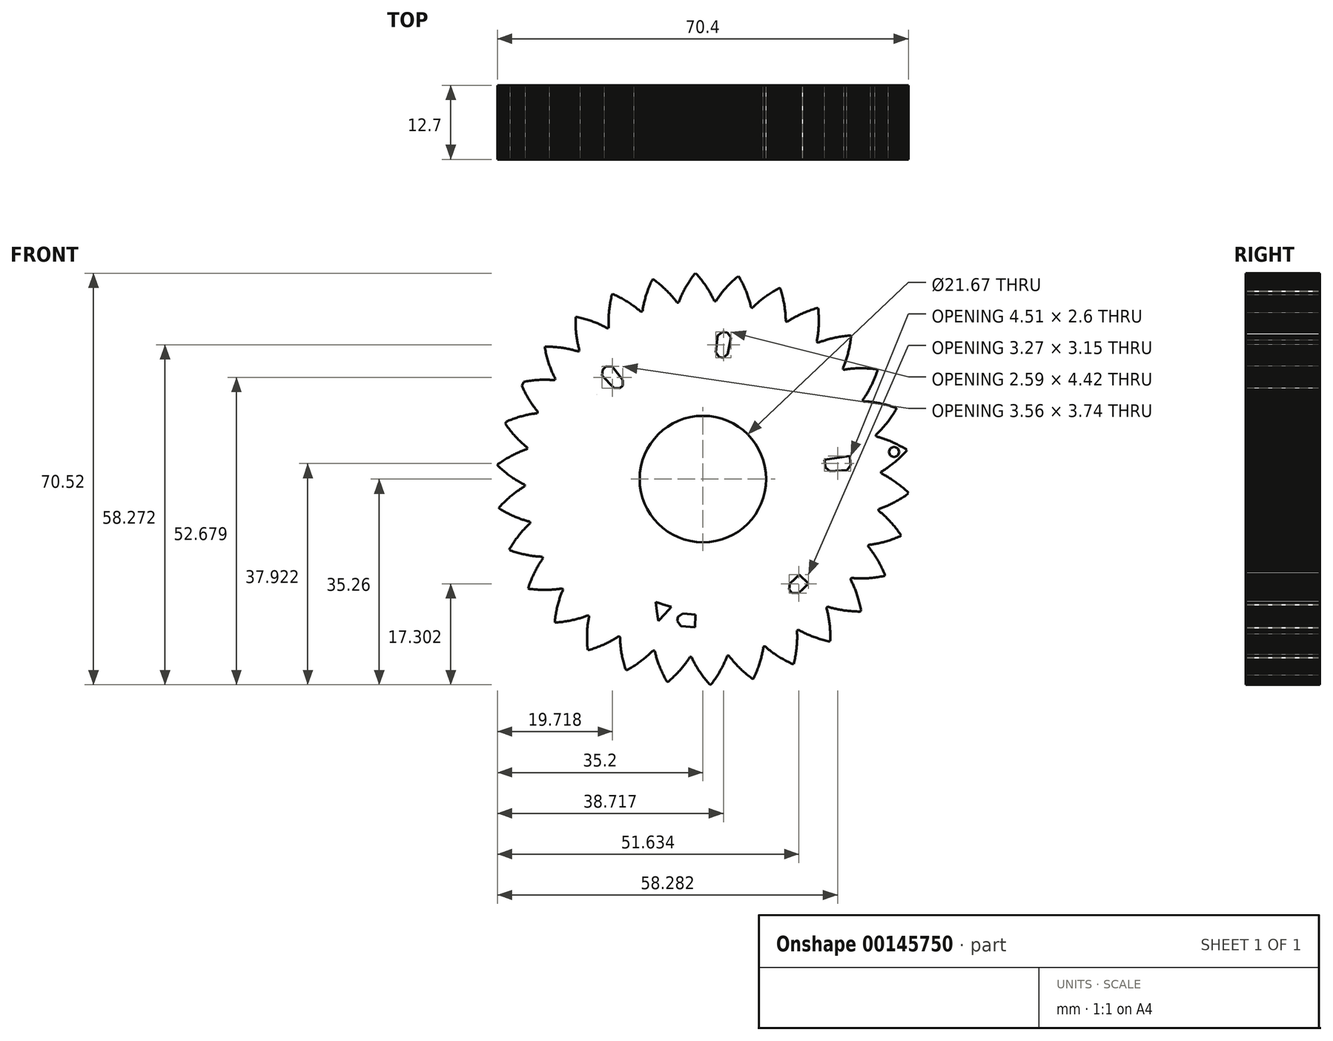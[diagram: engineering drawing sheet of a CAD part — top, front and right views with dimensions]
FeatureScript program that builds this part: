
annotation { "Feature Type Name" : "Feature", "Feature Type Description" : "" }
export const myFeature = defineFeature(function(context is Context, id is Id, definition is map)
    precondition{}
    {
        {
            var Q0;
            Q0=qCreatedBy(makeId("Front.planeOp"),FACE);
            var sketch = newSketch(context, id + "F0", { "sketchPlane" : qUnion([Q0])});
            skLineSegment(sketch, "E0", {"start": v(30.52, 1.1) * mm, "end": v(30.55, 1.26) * mm});
            skLineSegment(sketch, "E1", {"start": v(30.55, 1.26) * mm, "end": v(30.7, 1.34) * mm});
            skLineSegment(sketch, "E2", {"start": v(30.7, 1.34) * mm, "end": v(30.84, 1.43) * mm});
            skLineSegment(sketch, "E3", {"start": v(30.84, 1.43) * mm, "end": v(31, 1.52) * mm});
            skLineSegment(sketch, "E4", {"start": v(31, 1.52) * mm, "end": v(31.14, 1.62) * mm});
            skLineSegment(sketch, "E5", {"start": v(31.14, 1.62) * mm, "end": v(31.3, 1.72) * mm});
            skLineSegment(sketch, "E6", {"start": v(31.3, 1.72) * mm, "end": v(31.45, 1.82) * mm});
            skLineSegment(sketch, "E7", {"start": v(31.45, 1.82) * mm, "end": v(31.6, 1.93) * mm});
            skLineSegment(sketch, "E8", {"start": v(31.6, 1.93) * mm, "end": v(31.76, 2.04) * mm});
            skLineSegment(sketch, "E9", {"start": v(31.76, 2.04) * mm, "end": v(31.92, 2.15) * mm});
            skLineSegment(sketch, "E10", {"start": v(31.92, 2.15) * mm, "end": v(32.08, 2.27) * mm});
            skLineSegment(sketch, "E11", {"start": v(32.08, 2.27) * mm, "end": v(32.25, 2.4) * mm});
            skLineSegment(sketch, "E12", {"start": v(32.25, 2.4) * mm, "end": v(32.4, 2.52) * mm});
            skLineSegment(sketch, "E13", {"start": v(32.4, 2.52) * mm, "end": v(32.58, 2.65) * mm});
            skLineSegment(sketch, "E14", {"start": v(32.58, 2.65) * mm, "end": v(32.74, 2.79) * mm});
            skLineSegment(sketch, "E15", {"start": v(32.74, 2.79) * mm, "end": v(32.91, 2.93) * mm});
            skLineSegment(sketch, "E16", {"start": v(32.91, 2.93) * mm, "end": v(33.08, 3.07) * mm});
            skLineSegment(sketch, "E17", {"start": v(33.08, 3.07) * mm, "end": v(33.25, 3.22) * mm});
            skLineSegment(sketch, "E18", {"start": v(33.25, 3.22) * mm, "end": v(33.42, 3.37) * mm});
            skLineSegment(sketch, "E19", {"start": v(33.42, 3.37) * mm, "end": v(33.6, 3.53) * mm});
            skLineSegment(sketch, "E20", {"start": v(33.6, 3.53) * mm, "end": v(33.77, 3.69) * mm});
            skLineSegment(sketch, "E21", {"start": v(33.77, 3.69) * mm, "end": v(33.94, 3.85) * mm});
            skLineSegment(sketch, "E22", {"start": v(33.94, 3.85) * mm, "end": v(34.11, 4.02) * mm});
            skLineSegment(sketch, "E23", {"start": v(34.11, 4.02) * mm, "end": v(34.29, 4.2) * mm});
            skLineSegment(sketch, "E24", {"start": v(34.29, 4.2) * mm, "end": v(34.47, 4.38) * mm});
            skLineSegment(sketch, "E25", {"start": v(34.47, 4.38) * mm, "end": v(34.64, 4.56) * mm});
            skLineSegment(sketch, "E26", {"start": v(34.64, 4.56) * mm, "end": v(34.82, 4.75) * mm});
            skLineSegment(sketch, "E27", {"start": v(34.82, 4.75) * mm, "end": v(34.93, 4.94) * mm});
            skLineSegment(sketch, "E28", {"start": v(34.93, 4.94) * mm, "end": v(34.92, 4.98) * mm});
            skLineSegment(sketch, "E29", {"start": v(34.92, 4.98) * mm, "end": v(34.77, 5.13) * mm});
            skLineSegment(sketch, "E30", {"start": v(34.77, 5.13) * mm, "end": v(34.54, 5.26) * mm});
            skLineSegment(sketch, "E31", {"start": v(34.54, 5.26) * mm, "end": v(34.32, 5.39) * mm});
            skLineSegment(sketch, "E32", {"start": v(34.32, 5.39) * mm, "end": v(34.1, 5.51) * mm});
            skLineSegment(sketch, "E33", {"start": v(34.1, 5.51) * mm, "end": v(33.89, 5.63) * mm});
            skLineSegment(sketch, "E34", {"start": v(33.89, 5.63) * mm, "end": v(33.67, 5.74) * mm});
            skLineSegment(sketch, "E35", {"start": v(33.67, 5.74) * mm, "end": v(33.46, 5.86) * mm});
            skLineSegment(sketch, "E36", {"start": v(33.46, 5.86) * mm, "end": v(33.25, 5.96) * mm});
            skLineSegment(sketch, "E37", {"start": v(33.25, 5.96) * mm, "end": v(33.04, 6.06) * mm});
            skLineSegment(sketch, "E38", {"start": v(33.04, 6.06) * mm, "end": v(32.83, 6.16) * mm});
            skLineSegment(sketch, "E39", {"start": v(32.83, 6.16) * mm, "end": v(32.63, 6.26) * mm});
            skLineSegment(sketch, "E40", {"start": v(32.63, 6.26) * mm, "end": v(32.43, 6.35) * mm});
            skLineSegment(sketch, "E41", {"start": v(32.43, 6.35) * mm, "end": v(32.22, 6.44) * mm});
            skLineSegment(sketch, "E42", {"start": v(32.22, 6.44) * mm, "end": v(32.03, 6.52) * mm});
            skLineSegment(sketch, "E43", {"start": v(32.03, 6.52) * mm, "end": v(31.83, 6.6) * mm});
            skLineSegment(sketch, "E44", {"start": v(31.83, 6.6) * mm, "end": v(31.64, 6.68) * mm});
            skLineSegment(sketch, "E45", {"start": v(31.64, 6.68) * mm, "end": v(31.45, 6.75) * mm});
            skLineSegment(sketch, "E46", {"start": v(31.45, 6.75) * mm, "end": v(31.26, 6.82) * mm});
            skLineSegment(sketch, "E47", {"start": v(31.26, 6.82) * mm, "end": v(31.08, 6.88) * mm});
            skLineSegment(sketch, "E48", {"start": v(31.08, 6.88) * mm, "end": v(30.9, 6.95) * mm});
            skLineSegment(sketch, "E49", {"start": v(30.9, 6.95) * mm, "end": v(30.71, 7) * mm});
            skLineSegment(sketch, "E50", {"start": v(30.71, 7) * mm, "end": v(30.54, 7.06) * mm});
            skLineSegment(sketch, "E51", {"start": v(30.54, 7.06) * mm, "end": v(30.36, 7.11) * mm});
            skLineSegment(sketch, "E52", {"start": v(30.36, 7.11) * mm, "end": v(30.2, 7.16) * mm});
            skLineSegment(sketch, "E53", {"start": v(30.2, 7.16) * mm, "end": v(30.02, 7.2) * mm});
            skLineSegment(sketch, "E54", {"start": v(30.02, 7.2) * mm, "end": v(29.86, 7.25) * mm});
            skLineSegment(sketch, "E55", {"start": v(29.86, 7.25) * mm, "end": v(29.7, 7.3) * mm});
            skLineSegment(sketch, "E56", {"start": v(29.7, 7.3) * mm, "end": v(29.62, 7.43) * mm});
            skLineSegment(sketch, "E57", {"start": v(29.62, 7.43) * mm, "end": v(29.63, 7.59) * mm});
            skLineSegment(sketch, "E58", {"start": v(29.63, 7.59) * mm, "end": v(29.75, 7.7) * mm});
            skLineSegment(sketch, "E59", {"start": v(29.75, 7.7) * mm, "end": v(29.87, 7.81) * mm});
            skLineSegment(sketch, "E60", {"start": v(29.87, 7.81) * mm, "end": v(30, 7.93) * mm});
            skLineSegment(sketch, "E61", {"start": v(30, 7.93) * mm, "end": v(30.13, 8.06) * mm});
            skLineSegment(sketch, "E62", {"start": v(30.13, 8.06) * mm, "end": v(30.25, 8.19) * mm});
            skLineSegment(sketch, "E63", {"start": v(30.25, 8.19) * mm, "end": v(30.38, 8.32) * mm});
            skLineSegment(sketch, "E64", {"start": v(30.38, 8.32) * mm, "end": v(30.51, 8.46) * mm});
            skLineSegment(sketch, "E65", {"start": v(30.51, 8.46) * mm, "end": v(30.65, 8.6) * mm});
            skLineSegment(sketch, "E66", {"start": v(30.65, 8.6) * mm, "end": v(30.78, 8.74) * mm});
            skLineSegment(sketch, "E67", {"start": v(30.78, 8.74) * mm, "end": v(30.91, 8.9) * mm});
            skLineSegment(sketch, "E68", {"start": v(30.91, 8.9) * mm, "end": v(31.04, 9.05) * mm});
            skLineSegment(sketch, "E69", {"start": v(31.04, 9.05) * mm, "end": v(31.18, 9.2) * mm});
            skLineSegment(sketch, "E70", {"start": v(31.18, 9.2) * mm, "end": v(31.31, 9.37) * mm});
            skLineSegment(sketch, "E71", {"start": v(31.31, 9.37) * mm, "end": v(31.45, 9.53) * mm});
            skLineSegment(sketch, "E72", {"start": v(31.45, 9.53) * mm, "end": v(31.58, 9.7) * mm});
            skLineSegment(sketch, "E73", {"start": v(31.58, 9.7) * mm, "end": v(31.72, 9.88) * mm});
            skLineSegment(sketch, "E74", {"start": v(31.72, 9.88) * mm, "end": v(31.85, 10.06) * mm});
            skLineSegment(sketch, "E75", {"start": v(31.85, 10.06) * mm, "end": v(32, 10.24) * mm});
            skLineSegment(sketch, "E76", {"start": v(32, 10.24) * mm, "end": v(32.13, 10.43) * mm});
            skLineSegment(sketch, "E77", {"start": v(32.13, 10.43) * mm, "end": v(32.26, 10.63) * mm});
            skLineSegment(sketch, "E78", {"start": v(32.26, 10.63) * mm, "end": v(32.4, 10.83) * mm});
            skLineSegment(sketch, "E79", {"start": v(32.4, 10.83) * mm, "end": v(32.53, 11.03) * mm});
            skLineSegment(sketch, "E80", {"start": v(32.53, 11.03) * mm, "end": v(32.67, 11.24) * mm});
            skLineSegment(sketch, "E81", {"start": v(32.67, 11.24) * mm, "end": v(32.8, 11.45) * mm});
            skLineSegment(sketch, "E82", {"start": v(32.8, 11.45) * mm, "end": v(32.94, 11.67) * mm});
            skLineSegment(sketch, "E83", {"start": v(32.94, 11.67) * mm, "end": v(33.07, 11.89) * mm});
            skLineSegment(sketch, "E84", {"start": v(33.07, 11.89) * mm, "end": v(33.14, 12.1) * mm});
            skLineSegment(sketch, "E85", {"start": v(33.14, 12.1) * mm, "end": v(33.13, 12.13) * mm});
            skLineSegment(sketch, "E86", {"start": v(33.13, 12.13) * mm, "end": v(32.94, 12.24) * mm});
            skLineSegment(sketch, "E87", {"start": v(32.94, 12.24) * mm, "end": v(32.7, 12.33) * mm});
            skLineSegment(sketch, "E88", {"start": v(32.7, 12.33) * mm, "end": v(32.45, 12.4) * mm});
            skLineSegment(sketch, "E89", {"start": v(32.45, 12.4) * mm, "end": v(32.21, 12.48) * mm});
            skLineSegment(sketch, "E90", {"start": v(32.21, 12.48) * mm, "end": v(31.98, 12.55) * mm});
            skLineSegment(sketch, "E91", {"start": v(31.98, 12.55) * mm, "end": v(31.74, 12.62) * mm});
            skLineSegment(sketch, "E92", {"start": v(31.74, 12.62) * mm, "end": v(31.51, 12.68) * mm});
            skLineSegment(sketch, "E93", {"start": v(31.51, 12.68) * mm, "end": v(31.28, 12.75) * mm});
            skLineSegment(sketch, "E94", {"start": v(31.28, 12.75) * mm, "end": v(31.06, 12.8) * mm});
            skLineSegment(sketch, "E95", {"start": v(31.06, 12.8) * mm, "end": v(30.83, 12.86) * mm});
            skLineSegment(sketch, "E96", {"start": v(30.83, 12.86) * mm, "end": v(30.61, 12.9) * mm});
            skLineSegment(sketch, "E97", {"start": v(30.61, 12.9) * mm, "end": v(30.4, 12.95) * mm});
            skLineSegment(sketch, "E98", {"start": v(30.4, 12.95) * mm, "end": v(30.18, 13) * mm});
            skLineSegment(sketch, "E99", {"start": v(30.18, 13) * mm, "end": v(29.97, 13.04) * mm});
            skLineSegment(sketch, "E100", {"start": v(29.97, 13.04) * mm, "end": v(29.76, 13.07) * mm});
            skLineSegment(sketch, "E101", {"start": v(29.76, 13.07) * mm, "end": v(29.56, 13.1) * mm});
            skLineSegment(sketch, "E102", {"start": v(29.56, 13.1) * mm, "end": v(29.36, 13.14) * mm});
            skLineSegment(sketch, "E103", {"start": v(29.36, 13.14) * mm, "end": v(29.16, 13.17) * mm});
            skLineSegment(sketch, "E104", {"start": v(29.16, 13.17) * mm, "end": v(28.97, 13.2) * mm});
            skLineSegment(sketch, "E105", {"start": v(28.97, 13.2) * mm, "end": v(28.77, 13.22) * mm});
            skLineSegment(sketch, "E106", {"start": v(28.77, 13.22) * mm, "end": v(28.59, 13.24) * mm});
            skLineSegment(sketch, "E107", {"start": v(28.59, 13.24) * mm, "end": v(28.4, 13.25) * mm});
            skLineSegment(sketch, "E108", {"start": v(28.4, 13.25) * mm, "end": v(28.22, 13.27) * mm});
            skLineSegment(sketch, "E109", {"start": v(28.22, 13.27) * mm, "end": v(28.04, 13.28) * mm});
            skLineSegment(sketch, "E110", {"start": v(28.04, 13.28) * mm, "end": v(27.87, 13.3) * mm});
            skLineSegment(sketch, "E111", {"start": v(27.87, 13.3) * mm, "end": v(27.7, 13.3) * mm});
            skLineSegment(sketch, "E112", {"start": v(27.7, 13.3) * mm, "end": v(27.53, 13.3) * mm});
            skLineSegment(sketch, "E113", {"start": v(27.53, 13.3) * mm, "end": v(27.43, 13.42) * mm});
            skLineSegment(sketch, "E114", {"start": v(27.43, 13.42) * mm, "end": v(27.4, 13.58) * mm});
            skLineSegment(sketch, "E115", {"start": v(27.4, 13.58) * mm, "end": v(27.5, 13.72) * mm});
            skLineSegment(sketch, "E116", {"start": v(27.5, 13.72) * mm, "end": v(27.6, 13.85) * mm});
            skLineSegment(sketch, "E117", {"start": v(27.6, 13.85) * mm, "end": v(27.7, 14) * mm});
            skLineSegment(sketch, "E118", {"start": v(27.7, 14) * mm, "end": v(27.8, 14.15) * mm});
            skLineSegment(sketch, "E119", {"start": v(27.8, 14.15) * mm, "end": v(27.9, 14.3) * mm});
            skLineSegment(sketch, "E120", {"start": v(27.9, 14.3) * mm, "end": v(28, 14.46) * mm});
            skLineSegment(sketch, "E121", {"start": v(28, 14.46) * mm, "end": v(28.09, 14.62) * mm});
            skLineSegment(sketch, "E122", {"start": v(28.09, 14.62) * mm, "end": v(28.19, 14.78) * mm});
            skLineSegment(sketch, "E123", {"start": v(28.19, 14.78) * mm, "end": v(28.29, 14.95) * mm});
            skLineSegment(sketch, "E124", {"start": v(28.29, 14.95) * mm, "end": v(28.39, 15.13) * mm});
            skLineSegment(sketch, "E125", {"start": v(28.39, 15.13) * mm, "end": v(28.49, 15.3) * mm});
            skLineSegment(sketch, "E126", {"start": v(28.49, 15.3) * mm, "end": v(28.58, 15.49) * mm});
            skLineSegment(sketch, "E127", {"start": v(28.58, 15.49) * mm, "end": v(28.68, 15.67) * mm});
            skLineSegment(sketch, "E128", {"start": v(28.68, 15.67) * mm, "end": v(28.78, 15.86) * mm});
            skLineSegment(sketch, "E129", {"start": v(28.78, 15.86) * mm, "end": v(28.88, 16.06) * mm});
            skLineSegment(sketch, "E130", {"start": v(28.88, 16.06) * mm, "end": v(28.97, 16.26) * mm});
            skLineSegment(sketch, "E131", {"start": v(28.97, 16.26) * mm, "end": v(29.07, 16.46) * mm});
            skLineSegment(sketch, "E132", {"start": v(29.07, 16.46) * mm, "end": v(29.16, 16.67) * mm});
            skLineSegment(sketch, "E133", {"start": v(29.16, 16.67) * mm, "end": v(29.25, 16.89) * mm});
            skLineSegment(sketch, "E134", {"start": v(29.25, 16.89) * mm, "end": v(29.35, 17.1) * mm});
            skLineSegment(sketch, "E135", {"start": v(29.35, 17.1) * mm, "end": v(29.44, 17.32) * mm});
            skLineSegment(sketch, "E136", {"start": v(29.44, 17.32) * mm, "end": v(29.53, 17.55) * mm});
            skLineSegment(sketch, "E137", {"start": v(29.53, 17.55) * mm, "end": v(29.62, 17.78) * mm});
            skLineSegment(sketch, "E138", {"start": v(29.62, 17.78) * mm, "end": v(29.7, 18.02) * mm});
            skLineSegment(sketch, "E139", {"start": v(29.7, 18.02) * mm, "end": v(29.8, 18.26) * mm});
            skLineSegment(sketch, "E140", {"start": v(29.8, 18.26) * mm, "end": v(29.87, 18.5) * mm});
            skLineSegment(sketch, "E141", {"start": v(29.87, 18.5) * mm, "end": v(29.9, 18.72) * mm});
            skLineSegment(sketch, "E142", {"start": v(29.9, 18.72) * mm, "end": v(29.88, 18.75) * mm});
            skLineSegment(sketch, "E143", {"start": v(29.88, 18.75) * mm, "end": v(29.67, 18.82) * mm});
            skLineSegment(sketch, "E144", {"start": v(29.67, 18.82) * mm, "end": v(29.42, 18.85) * mm});
            skLineSegment(sketch, "E145", {"start": v(29.42, 18.85) * mm, "end": v(29.16, 18.88) * mm});
            skLineSegment(sketch, "E146", {"start": v(29.16, 18.88) * mm, "end": v(28.91, 18.9) * mm});
            skLineSegment(sketch, "E147", {"start": v(28.91, 18.9) * mm, "end": v(28.67, 18.93) * mm});
            skLineSegment(sketch, "E148", {"start": v(28.67, 18.93) * mm, "end": v(28.42, 18.94) * mm});
            skLineSegment(sketch, "E149", {"start": v(28.42, 18.94) * mm, "end": v(28.19, 18.96) * mm});
            skLineSegment(sketch, "E150", {"start": v(28.19, 18.96) * mm, "end": v(27.95, 18.97) * mm});
            skLineSegment(sketch, "E151", {"start": v(27.95, 18.97) * mm, "end": v(27.71, 18.98) * mm});
            skLineSegment(sketch, "E152", {"start": v(27.71, 18.98) * mm, "end": v(27.49, 18.99) * mm});
            skLineSegment(sketch, "E153", {"start": v(27.49, 18.99) * mm, "end": v(27.26, 18.99) * mm});
            skLineSegment(sketch, "E154", {"start": v(27.26, 18.99) * mm, "end": v(27.04, 18.99) * mm});
            skLineSegment(sketch, "E155", {"start": v(27.04, 18.99) * mm, "end": v(26.82, 18.99) * mm});
            skLineSegment(sketch, "E156", {"start": v(26.82, 18.99) * mm, "end": v(26.6, 18.98) * mm});
            skLineSegment(sketch, "E157", {"start": v(26.6, 18.98) * mm, "end": v(26.4, 18.98) * mm});
            skLineSegment(sketch, "E158", {"start": v(26.4, 18.98) * mm, "end": v(26.19, 18.97) * mm});
            skLineSegment(sketch, "E159", {"start": v(26.19, 18.97) * mm, "end": v(25.99, 18.96) * mm});
            skLineSegment(sketch, "E160", {"start": v(25.99, 18.96) * mm, "end": v(25.79, 18.94) * mm});
            skLineSegment(sketch, "E161", {"start": v(25.79, 18.94) * mm, "end": v(25.6, 18.93) * mm});
            skLineSegment(sketch, "E162", {"start": v(25.6, 18.93) * mm, "end": v(25.4, 18.9) * mm});
            skLineSegment(sketch, "E163", {"start": v(25.4, 18.9) * mm, "end": v(25.2, 18.9) * mm});
            skLineSegment(sketch, "E164", {"start": v(25.2, 18.9) * mm, "end": v(25.03, 18.87) * mm});
            skLineSegment(sketch, "E165", {"start": v(25.03, 18.87) * mm, "end": v(24.85, 18.85) * mm});
            skLineSegment(sketch, "E166", {"start": v(24.85, 18.85) * mm, "end": v(24.67, 18.82) * mm});
            skLineSegment(sketch, "E167", {"start": v(24.67, 18.82) * mm, "end": v(24.5, 18.8) * mm});
            skLineSegment(sketch, "E168", {"start": v(24.5, 18.8) * mm, "end": v(24.33, 18.77) * mm});
            skLineSegment(sketch, "E169", {"start": v(24.33, 18.77) * mm, "end": v(24.17, 18.74) * mm});
            skLineSegment(sketch, "E170", {"start": v(24.17, 18.74) * mm, "end": v(24.04, 18.83) * mm});
            skLineSegment(sketch, "E171", {"start": v(24.04, 18.83) * mm, "end": v(23.98, 18.98) * mm});
            skLineSegment(sketch, "E172", {"start": v(23.98, 18.98) * mm, "end": v(24.05, 19.13) * mm});
            skLineSegment(sketch, "E173", {"start": v(24.05, 19.13) * mm, "end": v(24.11, 19.29) * mm});
            skLineSegment(sketch, "E174", {"start": v(24.11, 19.29) * mm, "end": v(24.18, 19.45) * mm});
            skLineSegment(sketch, "E175", {"start": v(24.18, 19.45) * mm, "end": v(24.24, 19.62) * mm});
            skLineSegment(sketch, "E176", {"start": v(24.24, 19.62) * mm, "end": v(24.3, 19.79) * mm});
            skLineSegment(sketch, "E177", {"start": v(24.3, 19.79) * mm, "end": v(24.37, 19.96) * mm});
            skLineSegment(sketch, "E178", {"start": v(24.37, 19.96) * mm, "end": v(24.44, 20.14) * mm});
            skLineSegment(sketch, "E179", {"start": v(24.44, 20.14) * mm, "end": v(24.5, 20.32) * mm});
            skLineSegment(sketch, "E180", {"start": v(24.5, 20.32) * mm, "end": v(24.56, 20.5) * mm});
            skLineSegment(sketch, "E181", {"start": v(24.56, 20.5) * mm, "end": v(24.62, 20.7) * mm});
            skLineSegment(sketch, "E182", {"start": v(24.62, 20.7) * mm, "end": v(24.68, 20.9) * mm});
            skLineSegment(sketch, "E183", {"start": v(24.68, 20.9) * mm, "end": v(24.74, 21.09) * mm});
            skLineSegment(sketch, "E184", {"start": v(24.74, 21.09) * mm, "end": v(24.8, 21.3) * mm});
            skLineSegment(sketch, "E185", {"start": v(24.8, 21.3) * mm, "end": v(24.85, 21.5) * mm});
            skLineSegment(sketch, "E186", {"start": v(24.85, 21.5) * mm, "end": v(24.9, 21.71) * mm});
            skLineSegment(sketch, "E187", {"start": v(24.9, 21.71) * mm, "end": v(24.96, 21.93) * mm});
            skLineSegment(sketch, "E188", {"start": v(24.96, 21.93) * mm, "end": v(25, 22.15) * mm});
            skLineSegment(sketch, "E189", {"start": v(25, 22.15) * mm, "end": v(25.06, 22.37) * mm});
            skLineSegment(sketch, "E190", {"start": v(25.06, 22.37) * mm, "end": v(25.1, 22.6) * mm});
            skLineSegment(sketch, "E191", {"start": v(25.1, 22.6) * mm, "end": v(25.15, 22.83) * mm});
            skLineSegment(sketch, "E192", {"start": v(25.15, 22.83) * mm, "end": v(25.2, 23.07) * mm});
            skLineSegment(sketch, "E193", {"start": v(25.2, 23.07) * mm, "end": v(25.23, 23.3) * mm});
            skLineSegment(sketch, "E194", {"start": v(25.23, 23.3) * mm, "end": v(25.27, 23.55) * mm});
            skLineSegment(sketch, "E195", {"start": v(25.27, 23.55) * mm, "end": v(25.3, 23.8) * mm});
            skLineSegment(sketch, "E196", {"start": v(25.3, 23.8) * mm, "end": v(25.34, 24.05) * mm});
            skLineSegment(sketch, "E197", {"start": v(25.34, 24.05) * mm, "end": v(25.38, 24.3) * mm});
            skLineSegment(sketch, "E198", {"start": v(25.38, 24.3) * mm, "end": v(25.36, 24.53) * mm});
            skLineSegment(sketch, "E199", {"start": v(25.36, 24.53) * mm, "end": v(25.33, 24.56) * mm});
            skLineSegment(sketch, "E200", {"start": v(25.33, 24.56) * mm, "end": v(25.11, 24.58) * mm});
            skLineSegment(sketch, "E201", {"start": v(25.11, 24.58) * mm, "end": v(24.86, 24.56) * mm});
            skLineSegment(sketch, "E202", {"start": v(24.86, 24.56) * mm, "end": v(24.6, 24.53) * mm});
            skLineSegment(sketch, "E203", {"start": v(24.6, 24.53) * mm, "end": v(24.35, 24.5) * mm});
            skLineSegment(sketch, "E204", {"start": v(24.35, 24.5) * mm, "end": v(24.1, 24.47) * mm});
            skLineSegment(sketch, "E205", {"start": v(24.1, 24.47) * mm, "end": v(23.86, 24.44) * mm});
            skLineSegment(sketch, "E206", {"start": v(23.86, 24.44) * mm, "end": v(23.63, 24.4) * mm});
            skLineSegment(sketch, "E207", {"start": v(23.63, 24.4) * mm, "end": v(23.4, 24.37) * mm});
            skLineSegment(sketch, "E208", {"start": v(23.4, 24.37) * mm, "end": v(23.16, 24.33) * mm});
            skLineSegment(sketch, "E209", {"start": v(23.16, 24.33) * mm, "end": v(22.94, 24.29) * mm});
            skLineSegment(sketch, "E210", {"start": v(22.94, 24.29) * mm, "end": v(22.72, 24.24) * mm});
            skLineSegment(sketch, "E211", {"start": v(22.72, 24.24) * mm, "end": v(22.5, 24.2) * mm});
            skLineSegment(sketch, "E212", {"start": v(22.5, 24.2) * mm, "end": v(22.29, 24.15) * mm});
            skLineSegment(sketch, "E213", {"start": v(22.29, 24.15) * mm, "end": v(22.08, 24.1) * mm});
            skLineSegment(sketch, "E214", {"start": v(22.08, 24.1) * mm, "end": v(21.87, 24.05) * mm});
            skLineSegment(sketch, "E215", {"start": v(21.87, 24.05) * mm, "end": v(21.67, 24) * mm});
            skLineSegment(sketch, "E216", {"start": v(21.67, 24) * mm, "end": v(21.48, 23.94) * mm});
            skLineSegment(sketch, "E217", {"start": v(21.48, 23.94) * mm, "end": v(21.28, 23.89) * mm});
            skLineSegment(sketch, "E218", {"start": v(21.28, 23.89) * mm, "end": v(21.1, 23.83) * mm});
            skLineSegment(sketch, "E219", {"start": v(21.1, 23.83) * mm, "end": v(20.91, 23.78) * mm});
            skLineSegment(sketch, "E220", {"start": v(20.91, 23.78) * mm, "end": v(20.73, 23.72) * mm});
            skLineSegment(sketch, "E221", {"start": v(20.73, 23.72) * mm, "end": v(20.56, 23.66) * mm});
            skLineSegment(sketch, "E222", {"start": v(20.56, 23.66) * mm, "end": v(20.39, 23.6) * mm});
            skLineSegment(sketch, "E223", {"start": v(20.39, 23.6) * mm, "end": v(20.22, 23.54) * mm});
            skLineSegment(sketch, "E224", {"start": v(20.22, 23.54) * mm, "end": v(20.05, 23.48) * mm});
            skLineSegment(sketch, "E225", {"start": v(20.05, 23.48) * mm, "end": v(19.9, 23.42) * mm});
            skLineSegment(sketch, "E226", {"start": v(19.9, 23.42) * mm, "end": v(19.74, 23.36) * mm});
            skLineSegment(sketch, "E227", {"start": v(19.74, 23.36) * mm, "end": v(19.6, 23.42) * mm});
            skLineSegment(sketch, "E228", {"start": v(19.6, 23.42) * mm, "end": v(19.5, 23.55) * mm});
            skLineSegment(sketch, "E229", {"start": v(19.5, 23.55) * mm, "end": v(19.54, 23.71) * mm});
            skLineSegment(sketch, "E230", {"start": v(19.54, 23.71) * mm, "end": v(19.57, 23.88) * mm});
            skLineSegment(sketch, "E231", {"start": v(19.57, 23.88) * mm, "end": v(19.6, 24.05) * mm});
            skLineSegment(sketch, "E232", {"start": v(19.6, 24.05) * mm, "end": v(19.64, 24.23) * mm});
            skLineSegment(sketch, "E233", {"start": v(19.64, 24.23) * mm, "end": v(19.66, 24.4) * mm});
            skLineSegment(sketch, "E234", {"start": v(19.66, 24.4) * mm, "end": v(19.7, 24.6) * mm});
            skLineSegment(sketch, "E235", {"start": v(19.7, 24.6) * mm, "end": v(19.72, 24.78) * mm});
            skLineSegment(sketch, "E236", {"start": v(19.72, 24.78) * mm, "end": v(19.74, 24.97) * mm});
            skLineSegment(sketch, "E237", {"start": v(19.74, 24.97) * mm, "end": v(19.76, 25.16) * mm});
            skLineSegment(sketch, "E238", {"start": v(19.76, 25.16) * mm, "end": v(19.78, 25.36) * mm});
            skLineSegment(sketch, "E239", {"start": v(19.78, 25.36) * mm, "end": v(19.8, 25.57) * mm});
            skLineSegment(sketch, "E240", {"start": v(19.8, 25.57) * mm, "end": v(19.81, 25.77) * mm});
            skLineSegment(sketch, "E241", {"start": v(19.81, 25.77) * mm, "end": v(19.83, 25.98) * mm});
            skLineSegment(sketch, "E242", {"start": v(19.83, 25.98) * mm, "end": v(19.84, 26.2) * mm});
            skLineSegment(sketch, "E243", {"start": v(19.84, 26.2) * mm, "end": v(19.85, 26.42) * mm});
            skLineSegment(sketch, "E244", {"start": v(19.85, 26.42) * mm, "end": v(19.85, 26.64) * mm});
            skLineSegment(sketch, "E245", {"start": v(19.85, 26.64) * mm, "end": v(19.86, 26.86) * mm});
            skLineSegment(sketch, "E246", {"start": v(19.86, 26.86) * mm, "end": v(19.86, 27.1) * mm});
            skLineSegment(sketch, "E247", {"start": v(19.86, 27.1) * mm, "end": v(19.86, 27.33) * mm});
            skLineSegment(sketch, "E248", {"start": v(19.86, 27.33) * mm, "end": v(19.85, 27.56) * mm});
            skLineSegment(sketch, "E249", {"start": v(19.85, 27.56) * mm, "end": v(19.85, 27.8) * mm});
            skLineSegment(sketch, "E250", {"start": v(19.85, 27.8) * mm, "end": v(19.84, 28.04) * mm});
            skLineSegment(sketch, "E251", {"start": v(19.84, 28.04) * mm, "end": v(19.82, 28.3) * mm});
            skLineSegment(sketch, "E252", {"start": v(19.82, 28.3) * mm, "end": v(19.8, 28.54) * mm});
            skLineSegment(sketch, "E253", {"start": v(19.8, 28.54) * mm, "end": v(19.79, 28.8) * mm});
            skLineSegment(sketch, "E254", {"start": v(19.79, 28.8) * mm, "end": v(19.77, 29.05) * mm});
            skLineSegment(sketch, "E255", {"start": v(19.77, 29.05) * mm, "end": v(19.7, 29.26) * mm});
            skLineSegment(sketch, "E256", {"start": v(19.7, 29.26) * mm, "end": v(19.67, 29.29) * mm});
            skLineSegment(sketch, "E257", {"start": v(19.67, 29.29) * mm, "end": v(19.45, 29.27) * mm});
            skLineSegment(sketch, "E258", {"start": v(19.45, 29.27) * mm, "end": v(19.2, 29.19) * mm});
            skLineSegment(sketch, "E259", {"start": v(19.2, 29.19) * mm, "end": v(18.96, 29.11) * mm});
            skLineSegment(sketch, "E260", {"start": v(18.96, 29.11) * mm, "end": v(18.72, 29.03) * mm});
            skLineSegment(sketch, "E261", {"start": v(18.72, 29.03) * mm, "end": v(18.5, 28.95) * mm});
            skLineSegment(sketch, "E262", {"start": v(18.5, 28.95) * mm, "end": v(18.26, 28.87) * mm});
            skLineSegment(sketch, "E263", {"start": v(18.26, 28.87) * mm, "end": v(18.04, 28.78) * mm});
            skLineSegment(sketch, "E264", {"start": v(18.04, 28.78) * mm, "end": v(17.82, 28.7) * mm});
            skLineSegment(sketch, "E265", {"start": v(17.82, 28.7) * mm, "end": v(17.6, 28.61) * mm});
            skLineSegment(sketch, "E266", {"start": v(17.6, 28.61) * mm, "end": v(17.39, 28.52) * mm});
            skLineSegment(sketch, "E267", {"start": v(17.39, 28.52) * mm, "end": v(17.18, 28.43) * mm});
            skLineSegment(sketch, "E268", {"start": v(17.18, 28.43) * mm, "end": v(16.98, 28.34) * mm});
            skLineSegment(sketch, "E269", {"start": v(16.98, 28.34) * mm, "end": v(16.78, 28.26) * mm});
            skLineSegment(sketch, "E270", {"start": v(16.78, 28.26) * mm, "end": v(16.58, 28.16) * mm});
            skLineSegment(sketch, "E271", {"start": v(16.58, 28.16) * mm, "end": v(16.4, 28.07) * mm});
            skLineSegment(sketch, "E272", {"start": v(16.4, 28.07) * mm, "end": v(16.2, 27.98) * mm});
            skLineSegment(sketch, "E273", {"start": v(16.2, 27.98) * mm, "end": v(16.03, 27.89) * mm});
            skLineSegment(sketch, "E274", {"start": v(16.03, 27.89) * mm, "end": v(15.85, 27.8) * mm});
            skLineSegment(sketch, "E275", {"start": v(15.85, 27.8) * mm, "end": v(15.68, 27.7) * mm});
            skLineSegment(sketch, "E276", {"start": v(15.68, 27.7) * mm, "end": v(15.51, 27.6) * mm});
            skLineSegment(sketch, "E277", {"start": v(15.51, 27.6) * mm, "end": v(15.35, 27.51) * mm});
            skLineSegment(sketch, "E278", {"start": v(15.35, 27.51) * mm, "end": v(15.19, 27.42) * mm});
            skLineSegment(sketch, "E279", {"start": v(15.19, 27.42) * mm, "end": v(15.03, 27.32) * mm});
            skLineSegment(sketch, "E280", {"start": v(15.03, 27.32) * mm, "end": v(14.88, 27.23) * mm});
            skLineSegment(sketch, "E281", {"start": v(14.88, 27.23) * mm, "end": v(14.73, 27.14) * mm});
            skLineSegment(sketch, "E282", {"start": v(14.73, 27.14) * mm, "end": v(14.6, 27.04) * mm});
            skLineSegment(sketch, "E283", {"start": v(14.6, 27.04) * mm, "end": v(14.45, 26.95) * mm});
            skLineSegment(sketch, "E284", {"start": v(14.45, 26.95) * mm, "end": v(14.3, 26.98) * mm});
            skLineSegment(sketch, "E285", {"start": v(14.3, 26.98) * mm, "end": v(14.19, 27.1) * mm});
            skLineSegment(sketch, "E286", {"start": v(14.19, 27.1) * mm, "end": v(14.18, 27.26) * mm});
            skLineSegment(sketch, "E287", {"start": v(14.18, 27.26) * mm, "end": v(14.18, 27.43) * mm});
            skLineSegment(sketch, "E288", {"start": v(14.18, 27.43) * mm, "end": v(14.18, 27.6) * mm});
            skLineSegment(sketch, "E289", {"start": v(14.18, 27.6) * mm, "end": v(14.17, 27.78) * mm});
            skLineSegment(sketch, "E290", {"start": v(14.17, 27.78) * mm, "end": v(14.16, 27.96) * mm});
            skLineSegment(sketch, "E291", {"start": v(14.16, 27.96) * mm, "end": v(14.15, 28.15) * mm});
            skLineSegment(sketch, "E292", {"start": v(14.15, 28.15) * mm, "end": v(14.13, 28.34) * mm});
            skLineSegment(sketch, "E293", {"start": v(14.13, 28.34) * mm, "end": v(14.12, 28.53) * mm});
            skLineSegment(sketch, "E294", {"start": v(14.12, 28.53) * mm, "end": v(14.1, 28.72) * mm});
            skLineSegment(sketch, "E295", {"start": v(14.1, 28.72) * mm, "end": v(14.07, 28.92) * mm});
            skLineSegment(sketch, "E296", {"start": v(14.07, 28.92) * mm, "end": v(14.05, 29.12) * mm});
            skLineSegment(sketch, "E297", {"start": v(14.05, 29.12) * mm, "end": v(14.02, 29.33) * mm});
            skLineSegment(sketch, "E298", {"start": v(14.02, 29.33) * mm, "end": v(14, 29.54) * mm});
            skLineSegment(sketch, "E299", {"start": v(14, 29.54) * mm, "end": v(13.96, 29.75) * mm});
            skLineSegment(sketch, "E300", {"start": v(13.96, 29.75) * mm, "end": v(13.92, 29.96) * mm});
            skLineSegment(sketch, "E301", {"start": v(13.92, 29.96) * mm, "end": v(13.88, 30.18) * mm});
            skLineSegment(sketch, "E302", {"start": v(13.88, 30.18) * mm, "end": v(13.84, 30.4) * mm});
            skLineSegment(sketch, "E303", {"start": v(13.84, 30.4) * mm, "end": v(13.8, 30.63) * mm});
            skLineSegment(sketch, "E304", {"start": v(13.8, 30.63) * mm, "end": v(13.74, 30.86) * mm});
            skLineSegment(sketch, "E305", {"start": v(13.74, 30.86) * mm, "end": v(13.69, 31.09) * mm});
            skLineSegment(sketch, "E306", {"start": v(13.69, 31.09) * mm, "end": v(13.63, 31.32) * mm});
            skLineSegment(sketch, "E307", {"start": v(13.63, 31.32) * mm, "end": v(13.57, 31.56) * mm});
            skLineSegment(sketch, "E308", {"start": v(13.57, 31.56) * mm, "end": v(13.5, 31.8) * mm});
            skLineSegment(sketch, "E309", {"start": v(13.5, 31.8) * mm, "end": v(13.44, 32.04) * mm});
            skLineSegment(sketch, "E310", {"start": v(13.44, 32.04) * mm, "end": v(13.37, 32.28) * mm});
            skLineSegment(sketch, "E311", {"start": v(13.37, 32.28) * mm, "end": v(13.3, 32.53) * mm});
            skLineSegment(sketch, "E312", {"start": v(13.3, 32.53) * mm, "end": v(13.19, 32.72) * mm});
            skLineSegment(sketch, "E313", {"start": v(13.19, 32.72) * mm, "end": v(13.15, 32.74) * mm});
            skLineSegment(sketch, "E314", {"start": v(13.15, 32.74) * mm, "end": v(12.94, 32.67) * mm});
            skLineSegment(sketch, "E315", {"start": v(12.94, 32.67) * mm, "end": v(12.72, 32.54) * mm});
            skLineSegment(sketch, "E316", {"start": v(12.72, 32.54) * mm, "end": v(12.5, 32.42) * mm});
            skLineSegment(sketch, "E317", {"start": v(12.5, 32.42) * mm, "end": v(12.28, 32.3) * mm});
            skLineSegment(sketch, "E318", {"start": v(12.28, 32.3) * mm, "end": v(12.07, 32.16) * mm});
            skLineSegment(sketch, "E319", {"start": v(12.07, 32.16) * mm, "end": v(11.86, 32.03) * mm});
            skLineSegment(sketch, "E320", {"start": v(11.86, 32.03) * mm, "end": v(11.66, 31.9) * mm});
            skLineSegment(sketch, "E321", {"start": v(11.66, 31.9) * mm, "end": v(11.46, 31.77) * mm});
            skLineSegment(sketch, "E322", {"start": v(11.46, 31.77) * mm, "end": v(11.27, 31.65) * mm});
            skLineSegment(sketch, "E323", {"start": v(11.27, 31.65) * mm, "end": v(11.08, 31.52) * mm});
            skLineSegment(sketch, "E324", {"start": v(11.08, 31.52) * mm, "end": v(10.9, 31.38) * mm});
            skLineSegment(sketch, "E325", {"start": v(10.9, 31.38) * mm, "end": v(10.71, 31.26) * mm});
            skLineSegment(sketch, "E326", {"start": v(10.71, 31.26) * mm, "end": v(10.54, 31.13) * mm});
            skLineSegment(sketch, "E327", {"start": v(10.54, 31.13) * mm, "end": v(10.37, 31) * mm});
            skLineSegment(sketch, "E328", {"start": v(10.37, 31) * mm, "end": v(10.2, 30.87) * mm});
            skLineSegment(sketch, "E329", {"start": v(10.2, 30.87) * mm, "end": v(10.04, 30.74) * mm});
            skLineSegment(sketch, "E330", {"start": v(10.04, 30.74) * mm, "end": v(9.88, 30.6) * mm});
            skLineSegment(sketch, "E331", {"start": v(9.88, 30.6) * mm, "end": v(9.73, 30.48) * mm});
            skLineSegment(sketch, "E332", {"start": v(9.73, 30.48) * mm, "end": v(9.58, 30.35) * mm});
            skLineSegment(sketch, "E333", {"start": v(9.58, 30.35) * mm, "end": v(9.43, 30.23) * mm});
            skLineSegment(sketch, "E334", {"start": v(9.43, 30.23) * mm, "end": v(9.3, 30.1) * mm});
            skLineSegment(sketch, "E335", {"start": v(9.3, 30.1) * mm, "end": v(9.16, 29.98) * mm});
            skLineSegment(sketch, "E336", {"start": v(9.16, 29.98) * mm, "end": v(9.02, 29.85) * mm});
            skLineSegment(sketch, "E337", {"start": v(9.02, 29.85) * mm, "end": v(8.9, 29.73) * mm});
            skLineSegment(sketch, "E338", {"start": v(8.9, 29.73) * mm, "end": v(8.77, 29.6) * mm});
            skLineSegment(sketch, "E339", {"start": v(8.77, 29.6) * mm, "end": v(8.65, 29.49) * mm});
            skLineSegment(sketch, "E340", {"start": v(8.65, 29.49) * mm, "end": v(8.53, 29.37) * mm});
            skLineSegment(sketch, "E341", {"start": v(8.53, 29.37) * mm, "end": v(8.38, 29.37) * mm});
            skLineSegment(sketch, "E342", {"start": v(8.38, 29.37) * mm, "end": v(8.24, 29.45) * mm});
            skLineSegment(sketch, "E343", {"start": v(8.24, 29.45) * mm, "end": v(8.2, 29.61) * mm});
            skLineSegment(sketch, "E344", {"start": v(8.2, 29.61) * mm, "end": v(8.17, 29.78) * mm});
            skLineSegment(sketch, "E345", {"start": v(8.17, 29.78) * mm, "end": v(8.13, 29.95) * mm});
            skLineSegment(sketch, "E346", {"start": v(8.13, 29.95) * mm, "end": v(8.08, 30.12) * mm});
            skLineSegment(sketch, "E347", {"start": v(8.08, 30.12) * mm, "end": v(8.04, 30.3) * mm});
            skLineSegment(sketch, "E348", {"start": v(8.04, 30.3) * mm, "end": v(7.99, 30.47) * mm});
            skLineSegment(sketch, "E349", {"start": v(7.99, 30.47) * mm, "end": v(7.93, 30.65) * mm});
            skLineSegment(sketch, "E350", {"start": v(7.93, 30.65) * mm, "end": v(7.88, 30.84) * mm});
            skLineSegment(sketch, "E351", {"start": v(7.88, 30.84) * mm, "end": v(7.82, 31.03) * mm});
            skLineSegment(sketch, "E352", {"start": v(7.82, 31.03) * mm, "end": v(7.75, 31.22) * mm});
            skLineSegment(sketch, "E353", {"start": v(7.75, 31.22) * mm, "end": v(7.69, 31.4) * mm});
            skLineSegment(sketch, "E354", {"start": v(7.69, 31.4) * mm, "end": v(7.62, 31.6) * mm});
            skLineSegment(sketch, "E355", {"start": v(7.62, 31.6) * mm, "end": v(7.54, 31.8) * mm});
            skLineSegment(sketch, "E356", {"start": v(7.54, 31.8) * mm, "end": v(7.47, 32) * mm});
            skLineSegment(sketch, "E357", {"start": v(7.47, 32) * mm, "end": v(7.39, 32.2) * mm});
            skLineSegment(sketch, "E358", {"start": v(7.39, 32.2) * mm, "end": v(7.3, 32.4) * mm});
            skLineSegment(sketch, "E359", {"start": v(7.3, 32.4) * mm, "end": v(7.22, 32.62) * mm});
            skLineSegment(sketch, "E360", {"start": v(7.22, 32.62) * mm, "end": v(7.12, 32.83) * mm});
            skLineSegment(sketch, "E361", {"start": v(7.12, 32.83) * mm, "end": v(7.03, 33.04) * mm});
            skLineSegment(sketch, "E362", {"start": v(7.03, 33.04) * mm, "end": v(6.93, 33.25) * mm});
            skLineSegment(sketch, "E363", {"start": v(6.93, 33.25) * mm, "end": v(6.82, 33.47) * mm});
            skLineSegment(sketch, "E364", {"start": v(6.82, 33.47) * mm, "end": v(6.72, 33.69) * mm});
            skLineSegment(sketch, "E365", {"start": v(6.72, 33.69) * mm, "end": v(6.6, 33.9) * mm});
            skLineSegment(sketch, "E366", {"start": v(6.6, 33.9) * mm, "end": v(6.49, 34.13) * mm});
            skLineSegment(sketch, "E367", {"start": v(6.49, 34.13) * mm, "end": v(6.37, 34.36) * mm});
            skLineSegment(sketch, "E368", {"start": v(6.37, 34.36) * mm, "end": v(6.24, 34.58) * mm});
            skLineSegment(sketch, "E369", {"start": v(6.24, 34.58) * mm, "end": v(6.1, 34.75) * mm});
            skLineSegment(sketch, "E370", {"start": v(6.1, 34.75) * mm, "end": v(6.06, 34.75) * mm});
            skLineSegment(sketch, "E371", {"start": v(6.06, 34.75) * mm, "end": v(5.87, 34.65) * mm});
            skLineSegment(sketch, "E372", {"start": v(5.87, 34.65) * mm, "end": v(5.67, 34.48) * mm});
            skLineSegment(sketch, "E373", {"start": v(5.67, 34.48) * mm, "end": v(5.48, 34.3) * mm});
            skLineSegment(sketch, "E374", {"start": v(5.48, 34.3) * mm, "end": v(5.3, 34.14) * mm});
            skLineSegment(sketch, "E375", {"start": v(5.3, 34.14) * mm, "end": v(5.12, 33.97) * mm});
            skLineSegment(sketch, "E376", {"start": v(5.12, 33.97) * mm, "end": v(4.94, 33.8) * mm});
            skLineSegment(sketch, "E377", {"start": v(4.94, 33.8) * mm, "end": v(4.77, 33.63) * mm});
            skLineSegment(sketch, "E378", {"start": v(4.77, 33.63) * mm, "end": v(4.6, 33.46) * mm});
            skLineSegment(sketch, "E379", {"start": v(4.6, 33.46) * mm, "end": v(4.44, 33.3) * mm});
            skLineSegment(sketch, "E380", {"start": v(4.44, 33.3) * mm, "end": v(4.28, 33.13) * mm});
            skLineSegment(sketch, "E381", {"start": v(4.28, 33.13) * mm, "end": v(4.13, 32.96) * mm});
            skLineSegment(sketch, "E382", {"start": v(4.13, 32.96) * mm, "end": v(3.98, 32.8) * mm});
            skLineSegment(sketch, "E383", {"start": v(3.98, 32.8) * mm, "end": v(3.84, 32.64) * mm});
            skLineSegment(sketch, "E384", {"start": v(3.84, 32.64) * mm, "end": v(3.7, 32.47) * mm});
            skLineSegment(sketch, "E385", {"start": v(3.7, 32.47) * mm, "end": v(3.56, 32.31) * mm});
            skLineSegment(sketch, "E386", {"start": v(3.56, 32.31) * mm, "end": v(3.43, 32.15) * mm});
            skLineSegment(sketch, "E387", {"start": v(3.43, 32.15) * mm, "end": v(3.3, 32) * mm});
            skLineSegment(sketch, "E388", {"start": v(3.3, 32) * mm, "end": v(3.18, 31.84) * mm});
            skLineSegment(sketch, "E389", {"start": v(3.18, 31.84) * mm, "end": v(3.06, 31.68) * mm});
            skLineSegment(sketch, "E390", {"start": v(3.06, 31.68) * mm, "end": v(2.94, 31.53) * mm});
            skLineSegment(sketch, "E391", {"start": v(2.94, 31.53) * mm, "end": v(2.83, 31.38) * mm});
            skLineSegment(sketch, "E392", {"start": v(2.83, 31.38) * mm, "end": v(2.72, 31.23) * mm});
            skLineSegment(sketch, "E393", {"start": v(2.72, 31.23) * mm, "end": v(2.62, 31.08) * mm});
            skLineSegment(sketch, "E394", {"start": v(2.62, 31.08) * mm, "end": v(2.52, 30.93) * mm});
            skLineSegment(sketch, "E395", {"start": v(2.52, 30.93) * mm, "end": v(2.42, 30.78) * mm});
            skLineSegment(sketch, "E396", {"start": v(2.42, 30.78) * mm, "end": v(2.33, 30.64) * mm});
            skLineSegment(sketch, "E397", {"start": v(2.33, 30.64) * mm, "end": v(2.24, 30.5) * mm});
            skLineSegment(sketch, "E398", {"start": v(2.24, 30.5) * mm, "end": v(2.09, 30.47) * mm});
            skLineSegment(sketch, "E399", {"start": v(2.09, 30.47) * mm, "end": v(1.94, 30.52) * mm});
            skLineSegment(sketch, "E400", {"start": v(1.94, 30.52) * mm, "end": v(1.87, 30.67) * mm});
            skLineSegment(sketch, "E401", {"start": v(1.87, 30.67) * mm, "end": v(1.8, 30.83) * mm});
            skLineSegment(sketch, "E402", {"start": v(1.8, 30.83) * mm, "end": v(1.72, 30.98) * mm});
            skLineSegment(sketch, "E403", {"start": v(1.72, 30.98) * mm, "end": v(1.64, 31.14) * mm});
            skLineSegment(sketch, "E404", {"start": v(1.64, 31.14) * mm, "end": v(1.56, 31.3) * mm});
            skLineSegment(sketch, "E405", {"start": v(1.56, 31.3) * mm, "end": v(1.48, 31.47) * mm});
            skLineSegment(sketch, "E406", {"start": v(1.48, 31.47) * mm, "end": v(1.39, 31.63) * mm});
            skLineSegment(sketch, "E407", {"start": v(1.39, 31.63) * mm, "end": v(1.3, 31.8) * mm});
            skLineSegment(sketch, "E408", {"start": v(1.3, 31.8) * mm, "end": v(1.2, 31.97) * mm});
            skLineSegment(sketch, "E409", {"start": v(1.2, 31.97) * mm, "end": v(1.1, 32.15) * mm});
            skLineSegment(sketch, "E410", {"start": v(1.1, 32.15) * mm, "end": v(0.99, 32.32) * mm});
            skLineSegment(sketch, "E411", {"start": v(0.99, 32.32) * mm, "end": v(0.88, 32.5) * mm});
            skLineSegment(sketch, "E412", {"start": v(0.88, 32.5) * mm, "end": v(0.77, 32.67) * mm});
            skLineSegment(sketch, "E413", {"start": v(0.77, 32.67) * mm, "end": v(0.65, 32.86) * mm});
            skLineSegment(sketch, "E414", {"start": v(0.65, 32.86) * mm, "end": v(0.53, 33.04) * mm});
            skLineSegment(sketch, "E415", {"start": v(0.53, 33.04) * mm, "end": v(0.4, 33.22) * mm});
            skLineSegment(sketch, "E416", {"start": v(0.4, 33.22) * mm, "end": v(0.28, 33.4) * mm});
            skLineSegment(sketch, "E417", {"start": v(0.28, 33.4) * mm, "end": v(0.14, 33.6) * mm});
            skLineSegment(sketch, "E418", {"start": v(0.14, 33.6) * mm, "end": v(0, 33.78) * mm});
            skLineSegment(sketch, "E419", {"start": v(0, 33.78) * mm, "end": v(-0.14, 33.97) * mm});
            skLineSegment(sketch, "E420", {"start": v(-0.14, 33.97) * mm, "end": v(-0.29, 34.16) * mm});
            skLineSegment(sketch, "E421", {"start": v(-0.29, 34.16) * mm, "end": v(-0.44, 34.35) * mm});
            skLineSegment(sketch, "E422", {"start": v(-0.44, 34.35) * mm, "end": v(-0.6, 34.54) * mm});
            skLineSegment(sketch, "E423", {"start": v(-0.6, 34.54) * mm, "end": v(-0.75, 34.73) * mm});
            skLineSegment(sketch, "E424", {"start": v(-0.75, 34.73) * mm, "end": v(-0.92, 34.93) * mm});
            skLineSegment(sketch, "E425", {"start": v(-0.92, 34.93) * mm, "end": v(-1.09, 35.12) * mm});
            skLineSegment(sketch, "E426", {"start": v(-1.09, 35.12) * mm, "end": v(-1.26, 35.26) * mm});
            skLineSegment(sketch, "E427", {"start": v(-1.26, 35.26) * mm, "end": v(-1.3, 35.25) * mm});
            skLineSegment(sketch, "E428", {"start": v(-1.3, 35.25) * mm, "end": v(-1.46, 35.1) * mm});
            skLineSegment(sketch, "E429", {"start": v(-1.46, 35.1) * mm, "end": v(-1.62, 34.9) * mm});
            skLineSegment(sketch, "E430", {"start": v(-1.62, 34.9) * mm, "end": v(-1.77, 34.7) * mm});
            skLineSegment(sketch, "E431", {"start": v(-1.77, 34.7) * mm, "end": v(-1.92, 34.5) * mm});
            skLineSegment(sketch, "E432", {"start": v(-1.92, 34.5) * mm, "end": v(-2.06, 34.29) * mm});
            skLineSegment(sketch, "E433", {"start": v(-2.06, 34.29) * mm, "end": v(-2.2, 34.09) * mm});
            skLineSegment(sketch, "E434", {"start": v(-2.2, 34.09) * mm, "end": v(-2.33, 33.89) * mm});
            skLineSegment(sketch, "E435", {"start": v(-2.33, 33.89) * mm, "end": v(-2.45, 33.69) * mm});
            skLineSegment(sketch, "E436", {"start": v(-2.45, 33.69) * mm, "end": v(-2.58, 33.5) * mm});
            skLineSegment(sketch, "E437", {"start": v(-2.58, 33.5) * mm, "end": v(-2.7, 33.3) * mm});
            skLineSegment(sketch, "E438", {"start": v(-2.7, 33.3) * mm, "end": v(-2.81, 33.1) * mm});
            skLineSegment(sketch, "E439", {"start": v(-2.81, 33.1) * mm, "end": v(-2.93, 32.91) * mm});
            skLineSegment(sketch, "E440", {"start": v(-2.93, 32.91) * mm, "end": v(-3.03, 32.72) * mm});
            skLineSegment(sketch, "E441", {"start": v(-3.03, 32.72) * mm, "end": v(-3.14, 32.53) * mm});
            skLineSegment(sketch, "E442", {"start": v(-3.14, 32.53) * mm, "end": v(-3.24, 32.35) * mm});
            skLineSegment(sketch, "E443", {"start": v(-3.24, 32.35) * mm, "end": v(-3.33, 32.16) * mm});
            skLineSegment(sketch, "E444", {"start": v(-3.33, 32.16) * mm, "end": v(-3.42, 31.98) * mm});
            skLineSegment(sketch, "E445", {"start": v(-3.42, 31.98) * mm, "end": v(-3.51, 31.8) * mm});
            skLineSegment(sketch, "E446", {"start": v(-3.51, 31.8) * mm, "end": v(-3.6, 31.62) * mm});
            skLineSegment(sketch, "E447", {"start": v(-3.6, 31.62) * mm, "end": v(-3.68, 31.45) * mm});
            skLineSegment(sketch, "E448", {"start": v(-3.68, 31.45) * mm, "end": v(-3.76, 31.28) * mm});
            skLineSegment(sketch, "E449", {"start": v(-3.76, 31.28) * mm, "end": v(-3.83, 31.1) * mm});
            skLineSegment(sketch, "E450", {"start": v(-3.83, 31.1) * mm, "end": v(-3.9, 30.94) * mm});
            skLineSegment(sketch, "E451", {"start": v(-3.9, 30.94) * mm, "end": v(-3.97, 30.78) * mm});
            skLineSegment(sketch, "E452", {"start": v(-3.97, 30.78) * mm, "end": v(-4.03, 30.61) * mm});
            skLineSegment(sketch, "E453", {"start": v(-4.03, 30.61) * mm, "end": v(-4.1, 30.45) * mm});
            skLineSegment(sketch, "E454", {"start": v(-4.1, 30.45) * mm, "end": v(-4.15, 30.3) * mm});
            skLineSegment(sketch, "E455", {"start": v(-4.15, 30.3) * mm, "end": v(-4.3, 30.23) * mm});
            skLineSegment(sketch, "E456", {"start": v(-4.3, 30.23) * mm, "end": v(-4.45, 30.26) * mm});
            skLineSegment(sketch, "E457", {"start": v(-4.45, 30.26) * mm, "end": v(-4.55, 30.39) * mm});
            skLineSegment(sketch, "E458", {"start": v(-4.55, 30.39) * mm, "end": v(-4.65, 30.53) * mm});
            skLineSegment(sketch, "E459", {"start": v(-4.65, 30.53) * mm, "end": v(-4.76, 30.66) * mm});
            skLineSegment(sketch, "E460", {"start": v(-4.76, 30.66) * mm, "end": v(-4.87, 30.8) * mm});
            skLineSegment(sketch, "E461", {"start": v(-4.87, 30.8) * mm, "end": v(-4.98, 30.95) * mm});
            skLineSegment(sketch, "E462", {"start": v(-4.98, 30.95) * mm, "end": v(-5.1, 31.09) * mm});
            skLineSegment(sketch, "E463", {"start": v(-5.1, 31.09) * mm, "end": v(-5.22, 31.23) * mm});
            skLineSegment(sketch, "E464", {"start": v(-5.22, 31.23) * mm, "end": v(-5.35, 31.38) * mm});
            skLineSegment(sketch, "E465", {"start": v(-5.35, 31.38) * mm, "end": v(-5.48, 31.52) * mm});
            skLineSegment(sketch, "E466", {"start": v(-5.48, 31.52) * mm, "end": v(-5.61, 31.67) * mm});
            skLineSegment(sketch, "E467", {"start": v(-5.61, 31.67) * mm, "end": v(-5.75, 31.82) * mm});
            skLineSegment(sketch, "E468", {"start": v(-5.75, 31.82) * mm, "end": v(-5.9, 31.97) * mm});
            skLineSegment(sketch, "E469", {"start": v(-5.9, 31.97) * mm, "end": v(-6.04, 32.12) * mm});
            skLineSegment(sketch, "E470", {"start": v(-6.04, 32.12) * mm, "end": v(-6.2, 32.27) * mm});
            skLineSegment(sketch, "E471", {"start": v(-6.2, 32.27) * mm, "end": v(-6.35, 32.43) * mm});
            skLineSegment(sketch, "E472", {"start": v(-6.35, 32.43) * mm, "end": v(-6.5, 32.58) * mm});
            skLineSegment(sketch, "E473", {"start": v(-6.5, 32.58) * mm, "end": v(-6.68, 32.73) * mm});
            skLineSegment(sketch, "E474", {"start": v(-6.68, 32.73) * mm, "end": v(-6.84, 32.89) * mm});
            skLineSegment(sketch, "E475", {"start": v(-6.84, 32.89) * mm, "end": v(-7.02, 33.04) * mm});
            skLineSegment(sketch, "E476", {"start": v(-7.02, 33.04) * mm, "end": v(-7.2, 33.2) * mm});
            skLineSegment(sketch, "E477", {"start": v(-7.2, 33.2) * mm, "end": v(-7.38, 33.35) * mm});
            skLineSegment(sketch, "E478", {"start": v(-7.38, 33.35) * mm, "end": v(-7.57, 33.5) * mm});
            skLineSegment(sketch, "E479", {"start": v(-7.57, 33.5) * mm, "end": v(-7.76, 33.66) * mm});
            skLineSegment(sketch, "E480", {"start": v(-7.76, 33.66) * mm, "end": v(-7.96, 33.82) * mm});
            skLineSegment(sketch, "E481", {"start": v(-7.96, 33.82) * mm, "end": v(-8.16, 33.98) * mm});
            skLineSegment(sketch, "E482", {"start": v(-8.16, 33.98) * mm, "end": v(-8.37, 34.13) * mm});
            skLineSegment(sketch, "E483", {"start": v(-8.37, 34.13) * mm, "end": v(-8.56, 34.22) * mm});
            skLineSegment(sketch, "E484", {"start": v(-8.56, 34.22) * mm, "end": v(-8.6, 34.21) * mm});
            skLineSegment(sketch, "E485", {"start": v(-8.6, 34.21) * mm, "end": v(-8.73, 34.04) * mm});
            skLineSegment(sketch, "E486", {"start": v(-8.73, 34.04) * mm, "end": v(-8.84, 33.8) * mm});
            skLineSegment(sketch, "E487", {"start": v(-8.84, 33.8) * mm, "end": v(-8.95, 33.57) * mm});
            skLineSegment(sketch, "E488", {"start": v(-8.95, 33.57) * mm, "end": v(-9.05, 33.34) * mm});
            skLineSegment(sketch, "E489", {"start": v(-9.05, 33.34) * mm, "end": v(-9.14, 33.11) * mm});
            skLineSegment(sketch, "E490", {"start": v(-9.14, 33.11) * mm, "end": v(-9.23, 32.89) * mm});
            skLineSegment(sketch, "E491", {"start": v(-9.23, 32.89) * mm, "end": v(-9.32, 32.66) * mm});
            skLineSegment(sketch, "E492", {"start": v(-9.32, 32.66) * mm, "end": v(-9.4, 32.44) * mm});
            skLineSegment(sketch, "E493", {"start": v(-9.4, 32.44) * mm, "end": v(-9.49, 32.22) * mm});
            skLineSegment(sketch, "E494", {"start": v(-9.49, 32.22) * mm, "end": v(-9.56, 32) * mm});
            skLineSegment(sketch, "E495", {"start": v(-9.56, 32) * mm, "end": v(-9.64, 31.8) * mm});
            skLineSegment(sketch, "E496", {"start": v(-9.64, 31.8) * mm, "end": v(-9.7, 31.58) * mm});
            skLineSegment(sketch, "E497", {"start": v(-9.7, 31.58) * mm, "end": v(-9.77, 31.38) * mm});
            skLineSegment(sketch, "E498", {"start": v(-9.77, 31.38) * mm, "end": v(-9.83, 31.17) * mm});
            skLineSegment(sketch, "E499", {"start": v(-9.83, 31.17) * mm, "end": v(-9.9, 30.97) * mm});
            skLineSegment(sketch, "E500", {"start": v(-9.9, 30.97) * mm, "end": v(-9.95, 30.77) * mm});
            skLineSegment(sketch, "E501", {"start": v(-9.95, 30.77) * mm, "end": v(-10, 30.57) * mm});
            skLineSegment(sketch, "E502", {"start": v(-10, 30.57) * mm, "end": v(-10.05, 30.38) * mm});
            skLineSegment(sketch, "E503", {"start": v(-10.05, 30.38) * mm, "end": v(-10.1, 30.19) * mm});
            skLineSegment(sketch, "E504", {"start": v(-10.1, 30.19) * mm, "end": v(-10.14, 30) * mm});
            skLineSegment(sketch, "E505", {"start": v(-10.14, 30) * mm, "end": v(-10.18, 29.81) * mm});
            skLineSegment(sketch, "E506", {"start": v(-10.18, 29.81) * mm, "end": v(-10.21, 29.63) * mm});
            skLineSegment(sketch, "E507", {"start": v(-10.21, 29.63) * mm, "end": v(-10.25, 29.45) * mm});
            skLineSegment(sketch, "E508", {"start": v(-10.25, 29.45) * mm, "end": v(-10.28, 29.28) * mm});
            skLineSegment(sketch, "E509", {"start": v(-10.28, 29.28) * mm, "end": v(-10.3, 29.1) * mm});
            skLineSegment(sketch, "E510", {"start": v(-10.3, 29.1) * mm, "end": v(-10.33, 28.94) * mm});
            skLineSegment(sketch, "E511", {"start": v(-10.33, 28.94) * mm, "end": v(-10.36, 28.77) * mm});
            skLineSegment(sketch, "E512", {"start": v(-10.36, 28.77) * mm, "end": v(-10.48, 28.68) * mm});
            skLineSegment(sketch, "E513", {"start": v(-10.48, 28.68) * mm, "end": v(-10.64, 28.67) * mm});
            skLineSegment(sketch, "E514", {"start": v(-10.64, 28.67) * mm, "end": v(-10.77, 28.78) * mm});
            skLineSegment(sketch, "E515", {"start": v(-10.77, 28.78) * mm, "end": v(-10.9, 28.9) * mm});
            skLineSegment(sketch, "E516", {"start": v(-10.9, 28.9) * mm, "end": v(-11.03, 29) * mm});
            skLineSegment(sketch, "E517", {"start": v(-11.03, 29) * mm, "end": v(-11.16, 29.12) * mm});
            skLineSegment(sketch, "E518", {"start": v(-11.16, 29.12) * mm, "end": v(-11.3, 29.23) * mm});
            skLineSegment(sketch, "E519", {"start": v(-11.3, 29.23) * mm, "end": v(-11.45, 29.35) * mm});
            skLineSegment(sketch, "E520", {"start": v(-11.45, 29.35) * mm, "end": v(-11.6, 29.46) * mm});
            skLineSegment(sketch, "E521", {"start": v(-11.6, 29.46) * mm, "end": v(-11.75, 29.58) * mm});
            skLineSegment(sketch, "E522", {"start": v(-11.75, 29.58) * mm, "end": v(-11.91, 29.7) * mm});
            skLineSegment(sketch, "E523", {"start": v(-11.91, 29.7) * mm, "end": v(-12.07, 29.81) * mm});
            skLineSegment(sketch, "E524", {"start": v(-12.07, 29.81) * mm, "end": v(-12.24, 29.93) * mm});
            skLineSegment(sketch, "E525", {"start": v(-12.24, 29.93) * mm, "end": v(-12.41, 30.05) * mm});
            skLineSegment(sketch, "E526", {"start": v(-12.41, 30.05) * mm, "end": v(-12.59, 30.16) * mm});
            skLineSegment(sketch, "E527", {"start": v(-12.59, 30.16) * mm, "end": v(-12.77, 30.28) * mm});
            skLineSegment(sketch, "E528", {"start": v(-12.77, 30.28) * mm, "end": v(-12.95, 30.4) * mm});
            skLineSegment(sketch, "E529", {"start": v(-12.95, 30.4) * mm, "end": v(-13.14, 30.51) * mm});
            skLineSegment(sketch, "E530", {"start": v(-13.14, 30.51) * mm, "end": v(-13.34, 30.63) * mm});
            skLineSegment(sketch, "E531", {"start": v(-13.34, 30.63) * mm, "end": v(-13.53, 30.74) * mm});
            skLineSegment(sketch, "E532", {"start": v(-13.53, 30.74) * mm, "end": v(-13.74, 30.86) * mm});
            skLineSegment(sketch, "E533", {"start": v(-13.74, 30.86) * mm, "end": v(-13.94, 30.97) * mm});
            skLineSegment(sketch, "E534", {"start": v(-13.94, 30.97) * mm, "end": v(-14.15, 31.09) * mm});
            skLineSegment(sketch, "E535", {"start": v(-14.15, 31.09) * mm, "end": v(-14.37, 31.2) * mm});
            skLineSegment(sketch, "E536", {"start": v(-14.37, 31.2) * mm, "end": v(-14.59, 31.31) * mm});
            skLineSegment(sketch, "E537", {"start": v(-14.59, 31.31) * mm, "end": v(-14.82, 31.43) * mm});
            skLineSegment(sketch, "E538", {"start": v(-14.82, 31.43) * mm, "end": v(-15.05, 31.54) * mm});
            skLineSegment(sketch, "E539", {"start": v(-15.05, 31.54) * mm, "end": v(-15.28, 31.65) * mm});
            skLineSegment(sketch, "E540", {"start": v(-15.28, 31.65) * mm, "end": v(-15.49, 31.7) * mm});
            skLineSegment(sketch, "E541", {"start": v(-15.49, 31.7) * mm, "end": v(-15.53, 31.68) * mm});
            skLineSegment(sketch, "E542", {"start": v(-15.53, 31.68) * mm, "end": v(-15.62, 31.48) * mm});
            skLineSegment(sketch, "E543", {"start": v(-15.62, 31.48) * mm, "end": v(-15.68, 31.23) * mm});
            skLineSegment(sketch, "E544", {"start": v(-15.68, 31.23) * mm, "end": v(-15.73, 30.98) * mm});
            skLineSegment(sketch, "E545", {"start": v(-15.73, 30.98) * mm, "end": v(-15.78, 30.73) * mm});
            skLineSegment(sketch, "E546", {"start": v(-15.78, 30.73) * mm, "end": v(-15.83, 30.49) * mm});
            skLineSegment(sketch, "E547", {"start": v(-15.83, 30.49) * mm, "end": v(-15.87, 30.25) * mm});
            skLineSegment(sketch, "E548", {"start": v(-15.87, 30.25) * mm, "end": v(-15.9, 30.01) * mm});
            skLineSegment(sketch, "E549", {"start": v(-15.9, 30.01) * mm, "end": v(-15.95, 29.78) * mm});
            skLineSegment(sketch, "E550", {"start": v(-15.95, 29.78) * mm, "end": v(-15.98, 29.55) * mm});
            skLineSegment(sketch, "E551", {"start": v(-15.98, 29.55) * mm, "end": v(-16, 29.32) * mm});
            skLineSegment(sketch, "E552", {"start": v(-16, 29.32) * mm, "end": v(-16.03, 29.1) * mm});
            skLineSegment(sketch, "E553", {"start": v(-16.03, 29.1) * mm, "end": v(-16.06, 28.88) * mm});
            skLineSegment(sketch, "E554", {"start": v(-16.06, 28.88) * mm, "end": v(-16.08, 28.66) * mm});
            skLineSegment(sketch, "E555", {"start": v(-16.08, 28.66) * mm, "end": v(-16.1, 28.44) * mm});
            skLineSegment(sketch, "E556", {"start": v(-16.1, 28.44) * mm, "end": v(-16.11, 28.23) * mm});
            skLineSegment(sketch, "E557", {"start": v(-16.11, 28.23) * mm, "end": v(-16.13, 28.03) * mm});
            skLineSegment(sketch, "E558", {"start": v(-16.13, 28.03) * mm, "end": v(-16.14, 27.82) * mm});
            skLineSegment(sketch, "E559", {"start": v(-16.14, 27.82) * mm, "end": v(-16.14, 27.62) * mm});
            skLineSegment(sketch, "E560", {"start": v(-16.14, 27.62) * mm, "end": v(-16.15, 27.43) * mm});
            skLineSegment(sketch, "E561", {"start": v(-16.15, 27.43) * mm, "end": v(-16.15, 27.24) * mm});
            skLineSegment(sketch, "E562", {"start": v(-16.15, 27.24) * mm, "end": v(-16.15, 27.05) * mm});
            skLineSegment(sketch, "E563", {"start": v(-16.15, 27.05) * mm, "end": v(-16.15, 26.86) * mm});
            skLineSegment(sketch, "E564", {"start": v(-16.15, 26.86) * mm, "end": v(-16.15, 26.68) * mm});
            skLineSegment(sketch, "E565", {"start": v(-16.15, 26.68) * mm, "end": v(-16.14, 26.5) * mm});
            skLineSegment(sketch, "E566", {"start": v(-16.14, 26.5) * mm, "end": v(-16.13, 26.33) * mm});
            skLineSegment(sketch, "E567", {"start": v(-16.13, 26.33) * mm, "end": v(-16.12, 26.16) * mm});
            skLineSegment(sketch, "E568", {"start": v(-16.12, 26.16) * mm, "end": v(-16.11, 26) * mm});
            skLineSegment(sketch, "E569", {"start": v(-16.11, 26) * mm, "end": v(-16.22, 25.87) * mm});
            skLineSegment(sketch, "E570", {"start": v(-16.22, 25.87) * mm, "end": v(-16.37, 25.83) * mm});
            skLineSegment(sketch, "E571", {"start": v(-16.37, 25.83) * mm, "end": v(-16.51, 25.91) * mm});
            skLineSegment(sketch, "E572", {"start": v(-16.51, 25.91) * mm, "end": v(-16.66, 26) * mm});
            skLineSegment(sketch, "E573", {"start": v(-16.66, 26) * mm, "end": v(-16.82, 26.08) * mm});
            skLineSegment(sketch, "E574", {"start": v(-16.82, 26.08) * mm, "end": v(-16.97, 26.16) * mm});
            skLineSegment(sketch, "E575", {"start": v(-16.97, 26.16) * mm, "end": v(-17.14, 26.24) * mm});
            skLineSegment(sketch, "E576", {"start": v(-17.14, 26.24) * mm, "end": v(-17.3, 26.33) * mm});
            skLineSegment(sketch, "E577", {"start": v(-17.3, 26.33) * mm, "end": v(-17.47, 26.4) * mm});
            skLineSegment(sketch, "E578", {"start": v(-17.47, 26.4) * mm, "end": v(-17.65, 26.49) * mm});
            skLineSegment(sketch, "E579", {"start": v(-17.65, 26.49) * mm, "end": v(-17.83, 26.57) * mm});
            skLineSegment(sketch, "E580", {"start": v(-17.83, 26.57) * mm, "end": v(-18, 26.65) * mm});
            skLineSegment(sketch, "E581", {"start": v(-18, 26.65) * mm, "end": v(-18.2, 26.73) * mm});
            skLineSegment(sketch, "E582", {"start": v(-18.2, 26.73) * mm, "end": v(-18.39, 26.8) * mm});
            skLineSegment(sketch, "E583", {"start": v(-18.39, 26.8) * mm, "end": v(-18.58, 26.89) * mm});
            skLineSegment(sketch, "E584", {"start": v(-18.58, 26.89) * mm, "end": v(-18.78, 26.96) * mm});
            skLineSegment(sketch, "E585", {"start": v(-18.78, 26.96) * mm, "end": v(-18.99, 27.04) * mm});
            skLineSegment(sketch, "E586", {"start": v(-18.99, 27.04) * mm, "end": v(-19.2, 27.11) * mm});
            skLineSegment(sketch, "E587", {"start": v(-19.2, 27.11) * mm, "end": v(-19.41, 27.19) * mm});
            skLineSegment(sketch, "E588", {"start": v(-19.41, 27.19) * mm, "end": v(-19.63, 27.26) * mm});
            skLineSegment(sketch, "E589", {"start": v(-19.63, 27.26) * mm, "end": v(-19.85, 27.33) * mm});
            skLineSegment(sketch, "E590", {"start": v(-19.85, 27.33) * mm, "end": v(-20.08, 27.4) * mm});
            skLineSegment(sketch, "E591", {"start": v(-20.08, 27.4) * mm, "end": v(-20.3, 27.47) * mm});
            skLineSegment(sketch, "E592", {"start": v(-20.3, 27.47) * mm, "end": v(-20.54, 27.53) * mm});
            skLineSegment(sketch, "E593", {"start": v(-20.54, 27.53) * mm, "end": v(-20.78, 27.6) * mm});
            skLineSegment(sketch, "E594", {"start": v(-20.78, 27.6) * mm, "end": v(-21.02, 27.66) * mm});
            skLineSegment(sketch, "E595", {"start": v(-21.02, 27.66) * mm, "end": v(-21.27, 27.72) * mm});
            skLineSegment(sketch, "E596", {"start": v(-21.27, 27.72) * mm, "end": v(-21.53, 27.78) * mm});
            skLineSegment(sketch, "E597", {"start": v(-21.53, 27.78) * mm, "end": v(-21.74, 27.78) * mm});
            skLineSegment(sketch, "E598", {"start": v(-21.74, 27.78) * mm, "end": v(-21.77, 27.76) * mm});
            skLineSegment(sketch, "E599", {"start": v(-21.77, 27.76) * mm, "end": v(-21.82, 27.54) * mm});
            skLineSegment(sketch, "E600", {"start": v(-21.82, 27.54) * mm, "end": v(-21.83, 27.29) * mm});
            skLineSegment(sketch, "E601", {"start": v(-21.83, 27.29) * mm, "end": v(-21.83, 27.03) * mm});
            skLineSegment(sketch, "E602", {"start": v(-21.83, 27.03) * mm, "end": v(-21.82, 26.78) * mm});
            skLineSegment(sketch, "E603", {"start": v(-21.82, 26.78) * mm, "end": v(-21.82, 26.53) * mm});
            skLineSegment(sketch, "E604", {"start": v(-21.82, 26.53) * mm, "end": v(-21.81, 26.29) * mm});
            skLineSegment(sketch, "E605", {"start": v(-21.81, 26.29) * mm, "end": v(-21.8, 26.05) * mm});
            skLineSegment(sketch, "E606", {"start": v(-21.8, 26.05) * mm, "end": v(-21.79, 25.81) * mm});
            skLineSegment(sketch, "E607", {"start": v(-21.79, 25.81) * mm, "end": v(-21.77, 25.58) * mm});
            skLineSegment(sketch, "E608", {"start": v(-21.77, 25.58) * mm, "end": v(-21.75, 25.35) * mm});
            skLineSegment(sketch, "E609", {"start": v(-21.75, 25.35) * mm, "end": v(-21.73, 25.13) * mm});
            skLineSegment(sketch, "E610", {"start": v(-21.73, 25.13) * mm, "end": v(-21.71, 24.9) * mm});
            skLineSegment(sketch, "E611", {"start": v(-21.71, 24.9) * mm, "end": v(-21.69, 24.69) * mm});
            skLineSegment(sketch, "E612", {"start": v(-21.69, 24.69) * mm, "end": v(-21.66, 24.48) * mm});
            skLineSegment(sketch, "E613", {"start": v(-21.66, 24.48) * mm, "end": v(-21.63, 24.27) * mm});
            skLineSegment(sketch, "E614", {"start": v(-21.63, 24.27) * mm, "end": v(-21.6, 24.06) * mm});
            skLineSegment(sketch, "E615", {"start": v(-21.6, 24.06) * mm, "end": v(-21.57, 23.86) * mm});
            skLineSegment(sketch, "E616", {"start": v(-21.57, 23.86) * mm, "end": v(-21.53, 23.66) * mm});
            skLineSegment(sketch, "E617", {"start": v(-21.53, 23.66) * mm, "end": v(-21.5, 23.47) * mm});
            skLineSegment(sketch, "E618", {"start": v(-21.5, 23.47) * mm, "end": v(-21.46, 23.28) * mm});
            skLineSegment(sketch, "E619", {"start": v(-21.46, 23.28) * mm, "end": v(-21.42, 23.1) * mm});
            skLineSegment(sketch, "E620", {"start": v(-21.42, 23.1) * mm, "end": v(-21.38, 22.92) * mm});
            skLineSegment(sketch, "E621", {"start": v(-21.38, 22.92) * mm, "end": v(-21.34, 22.74) * mm});
            skLineSegment(sketch, "E622", {"start": v(-21.34, 22.74) * mm, "end": v(-21.3, 22.57) * mm});
            skLineSegment(sketch, "E623", {"start": v(-21.3, 22.57) * mm, "end": v(-21.25, 22.4) * mm});
            skLineSegment(sketch, "E624", {"start": v(-21.25, 22.4) * mm, "end": v(-21.21, 22.23) * mm});
            skLineSegment(sketch, "E625", {"start": v(-21.21, 22.23) * mm, "end": v(-21.17, 22.07) * mm});
            skLineSegment(sketch, "E626", {"start": v(-21.17, 22.07) * mm, "end": v(-21.24, 21.94) * mm});
            skLineSegment(sketch, "E627", {"start": v(-21.24, 21.94) * mm, "end": v(-21.38, 21.86) * mm});
            skLineSegment(sketch, "E628", {"start": v(-21.38, 21.86) * mm, "end": v(-21.54, 21.91) * mm});
            skLineSegment(sketch, "E629", {"start": v(-21.54, 21.91) * mm, "end": v(-21.7, 21.96) * mm});
            skLineSegment(sketch, "E630", {"start": v(-21.7, 21.96) * mm, "end": v(-21.87, 22.01) * mm});
            skLineSegment(sketch, "E631", {"start": v(-21.87, 22.01) * mm, "end": v(-22.04, 22.06) * mm});
            skLineSegment(sketch, "E632", {"start": v(-22.04, 22.06) * mm, "end": v(-22.22, 22.1) * mm});
            skLineSegment(sketch, "E633", {"start": v(-22.22, 22.1) * mm, "end": v(-22.4, 22.15) * mm});
            skLineSegment(sketch, "E634", {"start": v(-22.4, 22.15) * mm, "end": v(-22.58, 22.2) * mm});
            skLineSegment(sketch, "E635", {"start": v(-22.58, 22.2) * mm, "end": v(-22.77, 22.24) * mm});
            skLineSegment(sketch, "E636", {"start": v(-22.77, 22.24) * mm, "end": v(-22.96, 22.28) * mm});
            skLineSegment(sketch, "E637", {"start": v(-22.96, 22.28) * mm, "end": v(-23.16, 22.32) * mm});
            skLineSegment(sketch, "E638", {"start": v(-23.16, 22.32) * mm, "end": v(-23.36, 22.36) * mm});
            skLineSegment(sketch, "E639", {"start": v(-23.36, 22.36) * mm, "end": v(-23.56, 22.4) * mm});
            skLineSegment(sketch, "E640", {"start": v(-23.56, 22.4) * mm, "end": v(-23.77, 22.43) * mm});
            skLineSegment(sketch, "E641", {"start": v(-23.77, 22.43) * mm, "end": v(-23.98, 22.47) * mm});
            skLineSegment(sketch, "E642", {"start": v(-23.98, 22.47) * mm, "end": v(-24.2, 22.5) * mm});
            skLineSegment(sketch, "E643", {"start": v(-24.2, 22.5) * mm, "end": v(-24.42, 22.53) * mm});
            skLineSegment(sketch, "E644", {"start": v(-24.42, 22.53) * mm, "end": v(-24.64, 22.56) * mm});
            skLineSegment(sketch, "E645", {"start": v(-24.64, 22.56) * mm, "end": v(-24.87, 22.58) * mm});
            skLineSegment(sketch, "E646", {"start": v(-24.87, 22.58) * mm, "end": v(-25.1, 22.6) * mm});
            skLineSegment(sketch, "E647", {"start": v(-25.1, 22.6) * mm, "end": v(-25.34, 22.63) * mm});
            skLineSegment(sketch, "E648", {"start": v(-25.34, 22.63) * mm, "end": v(-25.58, 22.64) * mm});
            skLineSegment(sketch, "E649", {"start": v(-25.58, 22.64) * mm, "end": v(-25.82, 22.66) * mm});
            skLineSegment(sketch, "E650", {"start": v(-25.82, 22.66) * mm, "end": v(-26.07, 22.67) * mm});
            skLineSegment(sketch, "E651", {"start": v(-26.07, 22.67) * mm, "end": v(-26.32, 22.68) * mm});
            skLineSegment(sketch, "E652", {"start": v(-26.32, 22.68) * mm, "end": v(-26.57, 22.7) * mm});
            skLineSegment(sketch, "E653", {"start": v(-26.57, 22.7) * mm, "end": v(-26.83, 22.7) * mm});
            skLineSegment(sketch, "E654", {"start": v(-26.83, 22.7) * mm, "end": v(-27.04, 22.65) * mm});
            skLineSegment(sketch, "E655", {"start": v(-27.04, 22.65) * mm, "end": v(-27.07, 22.62) * mm});
            skLineSegment(sketch, "E656", {"start": v(-27.07, 22.62) * mm, "end": v(-27.07, 22.4) * mm});
            skLineSegment(sketch, "E657", {"start": v(-27.07, 22.4) * mm, "end": v(-27.02, 22.15) * mm});
            skLineSegment(sketch, "E658", {"start": v(-27.02, 22.15) * mm, "end": v(-26.97, 21.9) * mm});
            skLineSegment(sketch, "E659", {"start": v(-26.97, 21.9) * mm, "end": v(-26.91, 21.66) * mm});
            skLineSegment(sketch, "E660", {"start": v(-26.91, 21.66) * mm, "end": v(-26.86, 21.42) * mm});
            skLineSegment(sketch, "E661", {"start": v(-26.86, 21.42) * mm, "end": v(-26.8, 21.18) * mm});
            skLineSegment(sketch, "E662", {"start": v(-26.8, 21.18) * mm, "end": v(-26.74, 20.95) * mm});
            skLineSegment(sketch, "E663", {"start": v(-26.74, 20.95) * mm, "end": v(-26.68, 20.72) * mm});
            skLineSegment(sketch, "E664", {"start": v(-26.68, 20.72) * mm, "end": v(-26.61, 20.5) * mm});
            skLineSegment(sketch, "E665", {"start": v(-26.61, 20.5) * mm, "end": v(-26.55, 20.27) * mm});
            skLineSegment(sketch, "E666", {"start": v(-26.55, 20.27) * mm, "end": v(-26.48, 20.06) * mm});
            skLineSegment(sketch, "E667", {"start": v(-26.48, 20.06) * mm, "end": v(-26.42, 19.85) * mm});
            skLineSegment(sketch, "E668", {"start": v(-26.42, 19.85) * mm, "end": v(-26.35, 19.64) * mm});
            skLineSegment(sketch, "E669", {"start": v(-26.35, 19.64) * mm, "end": v(-26.28, 19.44) * mm});
            skLineSegment(sketch, "E670", {"start": v(-26.28, 19.44) * mm, "end": v(-26.2, 19.24) * mm});
            skLineSegment(sketch, "E671", {"start": v(-26.2, 19.24) * mm, "end": v(-26.13, 19.05) * mm});
            skLineSegment(sketch, "E672", {"start": v(-26.13, 19.05) * mm, "end": v(-26.06, 18.86) * mm});
            skLineSegment(sketch, "E673", {"start": v(-26.06, 18.86) * mm, "end": v(-25.98, 18.67) * mm});
            skLineSegment(sketch, "E674", {"start": v(-25.98, 18.67) * mm, "end": v(-25.9, 18.49) * mm});
            skLineSegment(sketch, "E675", {"start": v(-25.9, 18.49) * mm, "end": v(-25.83, 18.31) * mm});
            skLineSegment(sketch, "E676", {"start": v(-25.83, 18.31) * mm, "end": v(-25.76, 18.14) * mm});
            skLineSegment(sketch, "E677", {"start": v(-25.76, 18.14) * mm, "end": v(-25.68, 17.97) * mm});
            skLineSegment(sketch, "E678", {"start": v(-25.68, 17.97) * mm, "end": v(-25.6, 17.8) * mm});
            skLineSegment(sketch, "E679", {"start": v(-25.6, 17.8) * mm, "end": v(-25.53, 17.65) * mm});
            skLineSegment(sketch, "E680", {"start": v(-25.53, 17.65) * mm, "end": v(-25.45, 17.5) * mm});
            skLineSegment(sketch, "E681", {"start": v(-25.45, 17.5) * mm, "end": v(-25.37, 17.34) * mm});
            skLineSegment(sketch, "E682", {"start": v(-25.37, 17.34) * mm, "end": v(-25.3, 17.2) * mm});
            skLineSegment(sketch, "E683", {"start": v(-25.3, 17.2) * mm, "end": v(-25.34, 17.04) * mm});
            skLineSegment(sketch, "E684", {"start": v(-25.34, 17.04) * mm, "end": v(-25.46, 16.94) * mm});
            skLineSegment(sketch, "E685", {"start": v(-25.46, 16.94) * mm, "end": v(-25.63, 16.96) * mm});
            skLineSegment(sketch, "E686", {"start": v(-25.63, 16.96) * mm, "end": v(-25.8, 16.97) * mm});
            skLineSegment(sketch, "E687", {"start": v(-25.8, 16.97) * mm, "end": v(-25.97, 16.98) * mm});
            skLineSegment(sketch, "E688", {"start": v(-25.97, 16.98) * mm, "end": v(-26.15, 17) * mm});
            skLineSegment(sketch, "E689", {"start": v(-26.15, 17) * mm, "end": v(-26.33, 17) * mm});
            skLineSegment(sketch, "E690", {"start": v(-26.33, 17) * mm, "end": v(-26.51, 17.01) * mm});
            skLineSegment(sketch, "E691", {"start": v(-26.51, 17.01) * mm, "end": v(-26.7, 17.02) * mm});
            skLineSegment(sketch, "E692", {"start": v(-26.7, 17.02) * mm, "end": v(-26.9, 17.02) * mm});
            skLineSegment(sketch, "E693", {"start": v(-26.9, 17.02) * mm, "end": v(-27.1, 17.02) * mm});
            skLineSegment(sketch, "E694", {"start": v(-27.1, 17.02) * mm, "end": v(-27.3, 17.02) * mm});
            skLineSegment(sketch, "E695", {"start": v(-27.3, 17.02) * mm, "end": v(-27.5, 17.02) * mm});
            skLineSegment(sketch, "E696", {"start": v(-27.5, 17.02) * mm, "end": v(-27.7, 17.01) * mm});
            skLineSegment(sketch, "E697", {"start": v(-27.7, 17.01) * mm, "end": v(-27.91, 17) * mm});
            skLineSegment(sketch, "E698", {"start": v(-27.91, 17) * mm, "end": v(-28.13, 17) * mm});
            skLineSegment(sketch, "E699", {"start": v(-28.13, 17) * mm, "end": v(-28.35, 16.98) * mm});
            skLineSegment(sketch, "E700", {"start": v(-28.35, 16.98) * mm, "end": v(-28.57, 16.96) * mm});
            skLineSegment(sketch, "E701", {"start": v(-28.57, 16.96) * mm, "end": v(-28.8, 16.94) * mm});
            skLineSegment(sketch, "E702", {"start": v(-28.8, 16.94) * mm, "end": v(-29.02, 16.92) * mm});
            skLineSegment(sketch, "E703", {"start": v(-29.02, 16.92) * mm, "end": v(-29.25, 16.9) * mm});
            skLineSegment(sketch, "E704", {"start": v(-29.25, 16.9) * mm, "end": v(-29.49, 16.86) * mm});
            skLineSegment(sketch, "E705", {"start": v(-29.49, 16.86) * mm, "end": v(-29.72, 16.83) * mm});
            skLineSegment(sketch, "E706", {"start": v(-29.72, 16.83) * mm, "end": v(-29.97, 16.8) * mm});
            skLineSegment(sketch, "E707", {"start": v(-29.97, 16.8) * mm, "end": v(-30.2, 16.76) * mm});
            skLineSegment(sketch, "E708", {"start": v(-30.2, 16.76) * mm, "end": v(-30.46, 16.72) * mm});
            skLineSegment(sketch, "E709", {"start": v(-30.46, 16.72) * mm, "end": v(-30.7, 16.67) * mm});
            skLineSegment(sketch, "E710", {"start": v(-30.7, 16.67) * mm, "end": v(-30.96, 16.62) * mm});
            skLineSegment(sketch, "E711", {"start": v(-30.96, 16.62) * mm, "end": v(-31.16, 16.54) * mm});
            skLineSegment(sketch, "E712", {"start": v(-31.16, 16.54) * mm, "end": v(-31.18, 16.5) * mm});
            skLineSegment(sketch, "E713", {"start": v(-31.18, 16.5) * mm, "end": v(-31.14, 16.29) * mm});
            skLineSegment(sketch, "E714", {"start": v(-31.14, 16.29) * mm, "end": v(-31.04, 16.05) * mm});
            skLineSegment(sketch, "E715", {"start": v(-31.04, 16.05) * mm, "end": v(-30.93, 15.82) * mm});
            skLineSegment(sketch, "E716", {"start": v(-30.93, 15.82) * mm, "end": v(-30.83, 15.59) * mm});
            skLineSegment(sketch, "E717", {"start": v(-30.83, 15.59) * mm, "end": v(-30.72, 15.36) * mm});
            skLineSegment(sketch, "E718", {"start": v(-30.72, 15.36) * mm, "end": v(-30.62, 15.14) * mm});
            skLineSegment(sketch, "E719", {"start": v(-30.62, 15.14) * mm, "end": v(-30.51, 14.93) * mm});
            skLineSegment(sketch, "E720", {"start": v(-30.51, 14.93) * mm, "end": v(-30.4, 14.72) * mm});
            skLineSegment(sketch, "E721", {"start": v(-30.4, 14.72) * mm, "end": v(-30.3, 14.51) * mm});
            skLineSegment(sketch, "E722", {"start": v(-30.3, 14.51) * mm, "end": v(-30.18, 14.31) * mm});
            skLineSegment(sketch, "E723", {"start": v(-30.18, 14.31) * mm, "end": v(-30.07, 14.11) * mm});
            skLineSegment(sketch, "E724", {"start": v(-30.07, 14.11) * mm, "end": v(-29.96, 13.92) * mm});
            skLineSegment(sketch, "E725", {"start": v(-29.96, 13.92) * mm, "end": v(-29.85, 13.73) * mm});
            skLineSegment(sketch, "E726", {"start": v(-29.85, 13.73) * mm, "end": v(-29.74, 13.55) * mm});
            skLineSegment(sketch, "E727", {"start": v(-29.74, 13.55) * mm, "end": v(-29.63, 13.37) * mm});
            skLineSegment(sketch, "E728", {"start": v(-29.63, 13.37) * mm, "end": v(-29.52, 13.2) * mm});
            skLineSegment(sketch, "E729", {"start": v(-29.52, 13.2) * mm, "end": v(-29.4, 13.03) * mm});
            skLineSegment(sketch, "E730", {"start": v(-29.4, 13.03) * mm, "end": v(-29.3, 12.86) * mm});
            skLineSegment(sketch, "E731", {"start": v(-29.3, 12.86) * mm, "end": v(-29.19, 12.7) * mm});
            skLineSegment(sketch, "E732", {"start": v(-29.19, 12.7) * mm, "end": v(-29.08, 12.54) * mm});
            skLineSegment(sketch, "E733", {"start": v(-29.08, 12.54) * mm, "end": v(-28.97, 12.39) * mm});
            skLineSegment(sketch, "E734", {"start": v(-28.97, 12.39) * mm, "end": v(-28.85, 12.24) * mm});
            skLineSegment(sketch, "E735", {"start": v(-28.85, 12.24) * mm, "end": v(-28.74, 12.1) * mm});
            skLineSegment(sketch, "E736", {"start": v(-28.74, 12.1) * mm, "end": v(-28.64, 11.95) * mm});
            skLineSegment(sketch, "E737", {"start": v(-28.64, 11.95) * mm, "end": v(-28.53, 11.82) * mm});
            skLineSegment(sketch, "E738", {"start": v(-28.53, 11.82) * mm, "end": v(-28.42, 11.68) * mm});
            skLineSegment(sketch, "E739", {"start": v(-28.42, 11.68) * mm, "end": v(-28.31, 11.56) * mm});
            skLineSegment(sketch, "E740", {"start": v(-28.31, 11.56) * mm, "end": v(-28.33, 11.4) * mm});
            skLineSegment(sketch, "E741", {"start": v(-28.33, 11.4) * mm, "end": v(-28.43, 11.28) * mm});
            skLineSegment(sketch, "E742", {"start": v(-28.43, 11.28) * mm, "end": v(-28.6, 11.26) * mm});
            skLineSegment(sketch, "E743", {"start": v(-28.6, 11.26) * mm, "end": v(-28.76, 11.24) * mm});
            skLineSegment(sketch, "E744", {"start": v(-28.76, 11.24) * mm, "end": v(-28.93, 11.21) * mm});
            skLineSegment(sketch, "E745", {"start": v(-28.93, 11.21) * mm, "end": v(-29.1, 11.19) * mm});
            skLineSegment(sketch, "E746", {"start": v(-29.1, 11.19) * mm, "end": v(-29.29, 11.16) * mm});
            skLineSegment(sketch, "E747", {"start": v(-29.29, 11.16) * mm, "end": v(-29.47, 11.13) * mm});
            skLineSegment(sketch, "E748", {"start": v(-29.47, 11.13) * mm, "end": v(-29.66, 11.1) * mm});
            skLineSegment(sketch, "E749", {"start": v(-29.66, 11.1) * mm, "end": v(-29.85, 11.06) * mm});
            skLineSegment(sketch, "E750", {"start": v(-29.85, 11.06) * mm, "end": v(-30.04, 11.02) * mm});
            skLineSegment(sketch, "E751", {"start": v(-30.04, 11.02) * mm, "end": v(-30.23, 10.97) * mm});
            skLineSegment(sketch, "E752", {"start": v(-30.23, 10.97) * mm, "end": v(-30.43, 10.93) * mm});
            skLineSegment(sketch, "E753", {"start": v(-30.43, 10.93) * mm, "end": v(-30.63, 10.88) * mm});
            skLineSegment(sketch, "E754", {"start": v(-30.63, 10.88) * mm, "end": v(-30.84, 10.83) * mm});
            skLineSegment(sketch, "E755", {"start": v(-30.84, 10.83) * mm, "end": v(-31.05, 10.77) * mm});
            skLineSegment(sketch, "E756", {"start": v(-31.05, 10.77) * mm, "end": v(-31.26, 10.71) * mm});
            skLineSegment(sketch, "E757", {"start": v(-31.26, 10.71) * mm, "end": v(-31.47, 10.65) * mm});
            skLineSegment(sketch, "E758", {"start": v(-31.47, 10.65) * mm, "end": v(-31.68, 10.58) * mm});
            skLineSegment(sketch, "E759", {"start": v(-31.68, 10.58) * mm, "end": v(-31.9, 10.52) * mm});
            skLineSegment(sketch, "E760", {"start": v(-31.9, 10.52) * mm, "end": v(-32.12, 10.44) * mm});
            skLineSegment(sketch, "E761", {"start": v(-32.12, 10.44) * mm, "end": v(-32.35, 10.37) * mm});
            skLineSegment(sketch, "E762", {"start": v(-32.35, 10.37) * mm, "end": v(-32.57, 10.28) * mm});
            skLineSegment(sketch, "E763", {"start": v(-32.57, 10.28) * mm, "end": v(-32.8, 10.2) * mm});
            skLineSegment(sketch, "E764", {"start": v(-32.8, 10.2) * mm, "end": v(-33.03, 10.11) * mm});
            skLineSegment(sketch, "E765", {"start": v(-33.03, 10.11) * mm, "end": v(-33.27, 10.02) * mm});
            skLineSegment(sketch, "E766", {"start": v(-33.27, 10.02) * mm, "end": v(-33.5, 9.92) * mm});
            skLineSegment(sketch, "E767", {"start": v(-33.5, 9.92) * mm, "end": v(-33.74, 9.82) * mm});
            skLineSegment(sketch, "E768", {"start": v(-33.74, 9.82) * mm, "end": v(-33.92, 9.7) * mm});
            skLineSegment(sketch, "E769", {"start": v(-33.92, 9.7) * mm, "end": v(-33.93, 9.66) * mm});
            skLineSegment(sketch, "E770", {"start": v(-33.93, 9.66) * mm, "end": v(-33.84, 9.46) * mm});
            skLineSegment(sketch, "E771", {"start": v(-33.84, 9.46) * mm, "end": v(-33.7, 9.25) * mm});
            skLineSegment(sketch, "E772", {"start": v(-33.7, 9.25) * mm, "end": v(-33.55, 9.04) * mm});
            skLineSegment(sketch, "E773", {"start": v(-33.55, 9.04) * mm, "end": v(-33.4, 8.84) * mm});
            skLineSegment(sketch, "E774", {"start": v(-33.4, 8.84) * mm, "end": v(-33.25, 8.64) * mm});
            skLineSegment(sketch, "E775", {"start": v(-33.25, 8.64) * mm, "end": v(-33.1, 8.45) * mm});
            skLineSegment(sketch, "E776", {"start": v(-33.1, 8.45) * mm, "end": v(-32.95, 8.26) * mm});
            skLineSegment(sketch, "E777", {"start": v(-32.95, 8.26) * mm, "end": v(-32.8, 8.08) * mm});
            skLineSegment(sketch, "E778", {"start": v(-32.8, 8.08) * mm, "end": v(-32.65, 7.9) * mm});
            skLineSegment(sketch, "E779", {"start": v(-32.65, 7.9) * mm, "end": v(-32.5, 7.72) * mm});
            skLineSegment(sketch, "E780", {"start": v(-32.5, 7.72) * mm, "end": v(-32.35, 7.55) * mm});
            skLineSegment(sketch, "E781", {"start": v(-32.35, 7.55) * mm, "end": v(-32.2, 7.39) * mm});
            skLineSegment(sketch, "E782", {"start": v(-32.2, 7.39) * mm, "end": v(-32.06, 7.23) * mm});
            skLineSegment(sketch, "E783", {"start": v(-32.06, 7.23) * mm, "end": v(-31.9, 7.07) * mm});
            skLineSegment(sketch, "E784", {"start": v(-31.9, 7.07) * mm, "end": v(-31.76, 6.92) * mm});
            skLineSegment(sketch, "E785", {"start": v(-31.76, 6.92) * mm, "end": v(-31.62, 6.77) * mm});
            skLineSegment(sketch, "E786", {"start": v(-31.62, 6.77) * mm, "end": v(-31.47, 6.63) * mm});
            skLineSegment(sketch, "E787", {"start": v(-31.47, 6.63) * mm, "end": v(-31.33, 6.49) * mm});
            skLineSegment(sketch, "E788", {"start": v(-31.33, 6.49) * mm, "end": v(-31.19, 6.35) * mm});
            skLineSegment(sketch, "E789", {"start": v(-31.19, 6.35) * mm, "end": v(-31.05, 6.22) * mm});
            skLineSegment(sketch, "E790", {"start": v(-31.05, 6.22) * mm, "end": v(-30.9, 6.1) * mm});
            skLineSegment(sketch, "E791", {"start": v(-30.9, 6.1) * mm, "end": v(-30.77, 5.97) * mm});
            skLineSegment(sketch, "E792", {"start": v(-30.77, 5.97) * mm, "end": v(-30.63, 5.85) * mm});
            skLineSegment(sketch, "E793", {"start": v(-30.63, 5.85) * mm, "end": v(-30.5, 5.74) * mm});
            skLineSegment(sketch, "E794", {"start": v(-30.5, 5.74) * mm, "end": v(-30.36, 5.63) * mm});
            skLineSegment(sketch, "E795", {"start": v(-30.36, 5.63) * mm, "end": v(-30.23, 5.52) * mm});
            skLineSegment(sketch, "E796", {"start": v(-30.23, 5.52) * mm, "end": v(-30.1, 5.42) * mm});
            skLineSegment(sketch, "E797", {"start": v(-30.1, 5.42) * mm, "end": v(-30.08, 5.26) * mm});
            skLineSegment(sketch, "E798", {"start": v(-30.08, 5.26) * mm, "end": v(-30.15, 5.12) * mm});
            skLineSegment(sketch, "E799", {"start": v(-30.15, 5.12) * mm, "end": v(-30.3, 5.07) * mm});
            skLineSegment(sketch, "E800", {"start": v(-30.3, 5.07) * mm, "end": v(-30.47, 5.01) * mm});
            skLineSegment(sketch, "E801", {"start": v(-30.47, 5.01) * mm, "end": v(-30.63, 4.95) * mm});
            skLineSegment(sketch, "E802", {"start": v(-30.63, 4.95) * mm, "end": v(-30.8, 4.9) * mm});
            skLineSegment(sketch, "E803", {"start": v(-30.8, 4.9) * mm, "end": v(-30.97, 4.83) * mm});
            skLineSegment(sketch, "E804", {"start": v(-30.97, 4.83) * mm, "end": v(-31.14, 4.76) * mm});
            skLineSegment(sketch, "E805", {"start": v(-31.14, 4.76) * mm, "end": v(-31.32, 4.69) * mm});
            skLineSegment(sketch, "E806", {"start": v(-31.32, 4.69) * mm, "end": v(-31.5, 4.6) * mm});
            skLineSegment(sketch, "E807", {"start": v(-31.5, 4.6) * mm, "end": v(-31.67, 4.53) * mm});
            skLineSegment(sketch, "E808", {"start": v(-31.67, 4.53) * mm, "end": v(-31.85, 4.45) * mm});
            skLineSegment(sketch, "E809", {"start": v(-31.85, 4.45) * mm, "end": v(-32.04, 4.36) * mm});
            skLineSegment(sketch, "E810", {"start": v(-32.04, 4.36) * mm, "end": v(-32.23, 4.27) * mm});
            skLineSegment(sketch, "E811", {"start": v(-32.23, 4.27) * mm, "end": v(-32.42, 4.18) * mm});
            skLineSegment(sketch, "E812", {"start": v(-32.42, 4.18) * mm, "end": v(-32.6, 4.08) * mm});
            skLineSegment(sketch, "E813", {"start": v(-32.6, 4.08) * mm, "end": v(-32.8, 3.98) * mm});
            skLineSegment(sketch, "E814", {"start": v(-32.8, 3.98) * mm, "end": v(-33, 3.87) * mm});
            skLineSegment(sketch, "E815", {"start": v(-33, 3.87) * mm, "end": v(-33.2, 3.77) * mm});
            skLineSegment(sketch, "E816", {"start": v(-33.2, 3.77) * mm, "end": v(-33.4, 3.65) * mm});
            skLineSegment(sketch, "E817", {"start": v(-33.4, 3.65) * mm, "end": v(-33.6, 3.53) * mm});
            skLineSegment(sketch, "E818", {"start": v(-33.6, 3.53) * mm, "end": v(-33.8, 3.41) * mm});
            skLineSegment(sketch, "E819", {"start": v(-33.8, 3.41) * mm, "end": v(-34, 3.29) * mm});
            skLineSegment(sketch, "E820", {"start": v(-34, 3.29) * mm, "end": v(-34.2, 3.16) * mm});
            skLineSegment(sketch, "E821", {"start": v(-34.2, 3.16) * mm, "end": v(-34.41, 3.02) * mm});
            skLineSegment(sketch, "E822", {"start": v(-34.41, 3.02) * mm, "end": v(-34.62, 2.88) * mm});
            skLineSegment(sketch, "E823", {"start": v(-34.62, 2.88) * mm, "end": v(-34.83, 2.74) * mm});
            skLineSegment(sketch, "E824", {"start": v(-34.83, 2.74) * mm, "end": v(-35.05, 2.6) * mm});
            skLineSegment(sketch, "E825", {"start": v(-35.05, 2.6) * mm, "end": v(-35.2, 2.43) * mm});
            skLineSegment(sketch, "E826", {"start": v(-35.2, 2.43) * mm, "end": v(-35.2, 2.4) * mm});
            skLineSegment(sketch, "E827", {"start": v(-35.2, 2.4) * mm, "end": v(-35.07, 2.21) * mm});
            skLineSegment(sketch, "E828", {"start": v(-35.07, 2.21) * mm, "end": v(-34.88, 2.04) * mm});
            skLineSegment(sketch, "E829", {"start": v(-34.88, 2.04) * mm, "end": v(-34.7, 1.87) * mm});
            skLineSegment(sketch, "E830", {"start": v(-34.7, 1.87) * mm, "end": v(-34.5, 1.7) * mm});
            skLineSegment(sketch, "E831", {"start": v(-34.5, 1.7) * mm, "end": v(-34.32, 1.54) * mm});
            skLineSegment(sketch, "E832", {"start": v(-34.32, 1.54) * mm, "end": v(-34.13, 1.38) * mm});
            skLineSegment(sketch, "E833", {"start": v(-34.13, 1.38) * mm, "end": v(-33.95, 1.23) * mm});
            skLineSegment(sketch, "E834", {"start": v(-33.95, 1.23) * mm, "end": v(-33.76, 1.08) * mm});
            skLineSegment(sketch, "E835", {"start": v(-33.76, 1.08) * mm, "end": v(-33.58, 0.94) * mm});
            skLineSegment(sketch, "E836", {"start": v(-33.58, 0.94) * mm, "end": v(-33.4, 0.8) * mm});
            skLineSegment(sketch, "E837", {"start": v(-33.4, 0.8) * mm, "end": v(-33.22, 0.66) * mm});
            skLineSegment(sketch, "E838", {"start": v(-33.22, 0.66) * mm, "end": v(-33.04, 0.53) * mm});
            skLineSegment(sketch, "E839", {"start": v(-33.04, 0.53) * mm, "end": v(-32.86, 0.4) * mm});
            skLineSegment(sketch, "E840", {"start": v(-32.86, 0.4) * mm, "end": v(-32.68, 0.28) * mm});
            skLineSegment(sketch, "E841", {"start": v(-32.68, 0.28) * mm, "end": v(-32.5, 0.16) * mm});
            skLineSegment(sketch, "E842", {"start": v(-32.5, 0.16) * mm, "end": v(-32.34, 0.05) * mm});
            skLineSegment(sketch, "E843", {"start": v(-32.34, 0.05) * mm, "end": v(-32.16, -0.06) * mm});
            skLineSegment(sketch, "E844", {"start": v(-32.16, -0.06) * mm, "end": v(-32, -0.17) * mm});
            skLineSegment(sketch, "E845", {"start": v(-32, -0.17) * mm, "end": v(-31.83, -0.27) * mm});
            skLineSegment(sketch, "E846", {"start": v(-31.83, -0.27) * mm, "end": v(-31.66, -0.37) * mm});
            skLineSegment(sketch, "E847", {"start": v(-31.66, -0.37) * mm, "end": v(-31.5, -0.46) * mm});
            skLineSegment(sketch, "E848", {"start": v(-31.5, -0.46) * mm, "end": v(-31.34, -0.56) * mm});
            skLineSegment(sketch, "E849", {"start": v(-31.34, -0.56) * mm, "end": v(-31.18, -0.64) * mm});
            skLineSegment(sketch, "E850", {"start": v(-31.18, -0.64) * mm, "end": v(-31.02, -0.73) * mm});
            skLineSegment(sketch, "E851", {"start": v(-31.02, -0.73) * mm, "end": v(-30.87, -0.8) * mm});
            skLineSegment(sketch, "E852", {"start": v(-30.87, -0.8) * mm, "end": v(-30.72, -0.88) * mm});
            skLineSegment(sketch, "E853", {"start": v(-30.72, -0.88) * mm, "end": v(-30.57, -0.96) * mm});
            skLineSegment(sketch, "E854", {"start": v(-30.57, -0.96) * mm, "end": v(-30.52, -1.1) * mm});
            skLineSegment(sketch, "E855", {"start": v(-30.52, -1.1) * mm, "end": v(-30.56, -1.26) * mm});
            skLineSegment(sketch, "E856", {"start": v(-30.56, -1.26) * mm, "end": v(-30.7, -1.35) * mm});
            skLineSegment(sketch, "E857", {"start": v(-30.7, -1.35) * mm, "end": v(-30.84, -1.43) * mm});
            skLineSegment(sketch, "E858", {"start": v(-30.84, -1.43) * mm, "end": v(-31, -1.52) * mm});
            skLineSegment(sketch, "E859", {"start": v(-31, -1.52) * mm, "end": v(-31.14, -1.62) * mm});
            skLineSegment(sketch, "E860", {"start": v(-31.14, -1.62) * mm, "end": v(-31.3, -1.72) * mm});
            skLineSegment(sketch, "E861", {"start": v(-31.3, -1.72) * mm, "end": v(-31.45, -1.82) * mm});
            skLineSegment(sketch, "E862", {"start": v(-31.45, -1.82) * mm, "end": v(-31.6, -1.93) * mm});
            skLineSegment(sketch, "E863", {"start": v(-31.6, -1.93) * mm, "end": v(-31.76, -2.04) * mm});
            skLineSegment(sketch, "E864", {"start": v(-31.76, -2.04) * mm, "end": v(-31.92, -2.15) * mm});
            skLineSegment(sketch, "E865", {"start": v(-31.92, -2.15) * mm, "end": v(-32.08, -2.27) * mm});
            skLineSegment(sketch, "E866", {"start": v(-32.08, -2.27) * mm, "end": v(-32.25, -2.4) * mm});
            skLineSegment(sketch, "E867", {"start": v(-32.25, -2.4) * mm, "end": v(-32.41, -2.52) * mm});
            skLineSegment(sketch, "E868", {"start": v(-32.41, -2.52) * mm, "end": v(-32.58, -2.65) * mm});
            skLineSegment(sketch, "E869", {"start": v(-32.58, -2.65) * mm, "end": v(-32.74, -2.79) * mm});
            skLineSegment(sketch, "E870", {"start": v(-32.74, -2.79) * mm, "end": v(-32.91, -2.93) * mm});
            skLineSegment(sketch, "E871", {"start": v(-32.91, -2.93) * mm, "end": v(-33.08, -3.07) * mm});
            skLineSegment(sketch, "E872", {"start": v(-33.08, -3.07) * mm, "end": v(-33.25, -3.22) * mm});
            skLineSegment(sketch, "E873", {"start": v(-33.25, -3.22) * mm, "end": v(-33.42, -3.37) * mm});
            skLineSegment(sketch, "E874", {"start": v(-33.42, -3.37) * mm, "end": v(-33.6, -3.53) * mm});
            skLineSegment(sketch, "E875", {"start": v(-33.6, -3.53) * mm, "end": v(-33.77, -3.69) * mm});
            skLineSegment(sketch, "E876", {"start": v(-33.77, -3.69) * mm, "end": v(-33.94, -3.85) * mm});
            skLineSegment(sketch, "E877", {"start": v(-33.94, -3.85) * mm, "end": v(-34.11, -4.02) * mm});
            skLineSegment(sketch, "E878", {"start": v(-34.11, -4.02) * mm, "end": v(-34.29, -4.2) * mm});
            skLineSegment(sketch, "E879", {"start": v(-34.29, -4.2) * mm, "end": v(-34.47, -4.38) * mm});
            skLineSegment(sketch, "E880", {"start": v(-34.47, -4.38) * mm, "end": v(-34.64, -4.56) * mm});
            skLineSegment(sketch, "E881", {"start": v(-34.64, -4.56) * mm, "end": v(-34.82, -4.75) * mm});
            skLineSegment(sketch, "E882", {"start": v(-34.82, -4.75) * mm, "end": v(-34.93, -4.94) * mm});
            skLineSegment(sketch, "E883", {"start": v(-34.93, -4.94) * mm, "end": v(-34.93, -4.98) * mm});
            skLineSegment(sketch, "E884", {"start": v(-34.93, -4.98) * mm, "end": v(-34.77, -5.13) * mm});
            skLineSegment(sketch, "E885", {"start": v(-34.77, -5.13) * mm, "end": v(-34.54, -5.26) * mm});
            skLineSegment(sketch, "E886", {"start": v(-34.54, -5.26) * mm, "end": v(-34.32, -5.39) * mm});
            skLineSegment(sketch, "E887", {"start": v(-34.32, -5.39) * mm, "end": v(-34.1, -5.51) * mm});
            skLineSegment(sketch, "E888", {"start": v(-34.1, -5.51) * mm, "end": v(-33.89, -5.63) * mm});
            skLineSegment(sketch, "E889", {"start": v(-33.89, -5.63) * mm, "end": v(-33.67, -5.75) * mm});
            skLineSegment(sketch, "E890", {"start": v(-33.67, -5.75) * mm, "end": v(-33.46, -5.86) * mm});
            skLineSegment(sketch, "E891", {"start": v(-33.46, -5.86) * mm, "end": v(-33.25, -5.96) * mm});
            skLineSegment(sketch, "E892", {"start": v(-33.25, -5.96) * mm, "end": v(-33.04, -6.06) * mm});
            skLineSegment(sketch, "E893", {"start": v(-33.04, -6.06) * mm, "end": v(-32.83, -6.16) * mm});
            skLineSegment(sketch, "E894", {"start": v(-32.83, -6.16) * mm, "end": v(-32.63, -6.26) * mm});
            skLineSegment(sketch, "E895", {"start": v(-32.63, -6.26) * mm, "end": v(-32.43, -6.35) * mm});
            skLineSegment(sketch, "E896", {"start": v(-32.43, -6.35) * mm, "end": v(-32.22, -6.44) * mm});
            skLineSegment(sketch, "E897", {"start": v(-32.22, -6.44) * mm, "end": v(-32.03, -6.52) * mm});
            skLineSegment(sketch, "E898", {"start": v(-32.03, -6.52) * mm, "end": v(-31.83, -6.6) * mm});
            skLineSegment(sketch, "E899", {"start": v(-31.83, -6.6) * mm, "end": v(-31.64, -6.68) * mm});
            skLineSegment(sketch, "E900", {"start": v(-31.64, -6.68) * mm, "end": v(-31.45, -6.75) * mm});
            skLineSegment(sketch, "E901", {"start": v(-31.45, -6.75) * mm, "end": v(-31.26, -6.82) * mm});
            skLineSegment(sketch, "E902", {"start": v(-31.26, -6.82) * mm, "end": v(-31.08, -6.88) * mm});
            skLineSegment(sketch, "E903", {"start": v(-31.08, -6.88) * mm, "end": v(-30.9, -6.95) * mm});
            skLineSegment(sketch, "E904", {"start": v(-30.9, -6.95) * mm, "end": v(-30.71, -7) * mm});
            skLineSegment(sketch, "E905", {"start": v(-30.71, -7) * mm, "end": v(-30.54, -7.06) * mm});
            skLineSegment(sketch, "E906", {"start": v(-30.54, -7.06) * mm, "end": v(-30.36, -7.11) * mm});
            skLineSegment(sketch, "E907", {"start": v(-30.36, -7.11) * mm, "end": v(-30.2, -7.16) * mm});
            skLineSegment(sketch, "E908", {"start": v(-30.2, -7.16) * mm, "end": v(-30.02, -7.2) * mm});
            skLineSegment(sketch, "E909", {"start": v(-30.02, -7.2) * mm, "end": v(-29.86, -7.25) * mm});
            skLineSegment(sketch, "E910", {"start": v(-29.86, -7.25) * mm, "end": v(-29.7, -7.3) * mm});
            skLineSegment(sketch, "E911", {"start": v(-29.7, -7.3) * mm, "end": v(-29.62, -7.43) * mm});
            skLineSegment(sketch, "E912", {"start": v(-29.62, -7.43) * mm, "end": v(-29.63, -7.59) * mm});
            skLineSegment(sketch, "E913", {"start": v(-29.63, -7.59) * mm, "end": v(-29.75, -7.7) * mm});
            skLineSegment(sketch, "E914", {"start": v(-29.75, -7.7) * mm, "end": v(-29.87, -7.81) * mm});
            skLineSegment(sketch, "E915", {"start": v(-29.87, -7.81) * mm, "end": v(-30, -7.93) * mm});
            skLineSegment(sketch, "E916", {"start": v(-30, -7.93) * mm, "end": v(-30.13, -8.06) * mm});
            skLineSegment(sketch, "E917", {"start": v(-30.13, -8.06) * mm, "end": v(-30.25, -8.19) * mm});
            skLineSegment(sketch, "E918", {"start": v(-30.25, -8.19) * mm, "end": v(-30.38, -8.32) * mm});
            skLineSegment(sketch, "E919", {"start": v(-30.38, -8.32) * mm, "end": v(-30.51, -8.46) * mm});
            skLineSegment(sketch, "E920", {"start": v(-30.51, -8.46) * mm, "end": v(-30.65, -8.6) * mm});
            skLineSegment(sketch, "E921", {"start": v(-30.65, -8.6) * mm, "end": v(-30.78, -8.74) * mm});
            skLineSegment(sketch, "E922", {"start": v(-30.78, -8.74) * mm, "end": v(-30.91, -8.9) * mm});
            skLineSegment(sketch, "E923", {"start": v(-30.91, -8.9) * mm, "end": v(-31.04, -9.05) * mm});
            skLineSegment(sketch, "E924", {"start": v(-31.04, -9.05) * mm, "end": v(-31.18, -9.2) * mm});
            skLineSegment(sketch, "E925", {"start": v(-31.18, -9.2) * mm, "end": v(-31.31, -9.37) * mm});
            skLineSegment(sketch, "E926", {"start": v(-31.31, -9.37) * mm, "end": v(-31.45, -9.53) * mm});
            skLineSegment(sketch, "E927", {"start": v(-31.45, -9.53) * mm, "end": v(-31.58, -9.7) * mm});
            skLineSegment(sketch, "E928", {"start": v(-31.58, -9.7) * mm, "end": v(-31.72, -9.88) * mm});
            skLineSegment(sketch, "E929", {"start": v(-31.72, -9.88) * mm, "end": v(-31.85, -10.06) * mm});
            skLineSegment(sketch, "E930", {"start": v(-31.85, -10.06) * mm, "end": v(-32, -10.24) * mm});
            skLineSegment(sketch, "E931", {"start": v(-32, -10.24) * mm, "end": v(-32.13, -10.43) * mm});
            skLineSegment(sketch, "E932", {"start": v(-32.13, -10.43) * mm, "end": v(-32.26, -10.63) * mm});
            skLineSegment(sketch, "E933", {"start": v(-32.26, -10.63) * mm, "end": v(-32.4, -10.83) * mm});
            skLineSegment(sketch, "E934", {"start": v(-32.4, -10.83) * mm, "end": v(-32.53, -11.03) * mm});
            skLineSegment(sketch, "E935", {"start": v(-32.53, -11.03) * mm, "end": v(-32.67, -11.24) * mm});
            skLineSegment(sketch, "E936", {"start": v(-32.67, -11.24) * mm, "end": v(-32.8, -11.45) * mm});
            skLineSegment(sketch, "E937", {"start": v(-32.8, -11.45) * mm, "end": v(-32.94, -11.67) * mm});
            skLineSegment(sketch, "E938", {"start": v(-32.94, -11.67) * mm, "end": v(-33.07, -11.89) * mm});
            skLineSegment(sketch, "E939", {"start": v(-33.07, -11.89) * mm, "end": v(-33.14, -12.1) * mm});
            skLineSegment(sketch, "E940", {"start": v(-33.14, -12.1) * mm, "end": v(-33.13, -12.13) * mm});
            skLineSegment(sketch, "E941", {"start": v(-33.13, -12.13) * mm, "end": v(-32.94, -12.24) * mm});
            skLineSegment(sketch, "E942", {"start": v(-32.94, -12.24) * mm, "end": v(-32.7, -12.33) * mm});
            skLineSegment(sketch, "E943", {"start": v(-32.7, -12.33) * mm, "end": v(-32.45, -12.4) * mm});
            skLineSegment(sketch, "E944", {"start": v(-32.45, -12.4) * mm, "end": v(-32.21, -12.48) * mm});
            skLineSegment(sketch, "E945", {"start": v(-32.21, -12.48) * mm, "end": v(-31.98, -12.55) * mm});
            skLineSegment(sketch, "E946", {"start": v(-31.98, -12.55) * mm, "end": v(-31.74, -12.62) * mm});
            skLineSegment(sketch, "E947", {"start": v(-31.74, -12.62) * mm, "end": v(-31.51, -12.68) * mm});
            skLineSegment(sketch, "E948", {"start": v(-31.51, -12.68) * mm, "end": v(-31.28, -12.75) * mm});
            skLineSegment(sketch, "E949", {"start": v(-31.28, -12.75) * mm, "end": v(-31.06, -12.8) * mm});
            skLineSegment(sketch, "E950", {"start": v(-31.06, -12.8) * mm, "end": v(-30.83, -12.86) * mm});
            skLineSegment(sketch, "E951", {"start": v(-30.83, -12.86) * mm, "end": v(-30.61, -12.9) * mm});
            skLineSegment(sketch, "E952", {"start": v(-30.61, -12.9) * mm, "end": v(-30.4, -12.95) * mm});
            skLineSegment(sketch, "E953", {"start": v(-30.4, -12.95) * mm, "end": v(-30.18, -13) * mm});
            skLineSegment(sketch, "E954", {"start": v(-30.18, -13) * mm, "end": v(-29.97, -13.04) * mm});
            skLineSegment(sketch, "E955", {"start": v(-29.97, -13.04) * mm, "end": v(-29.76, -13.07) * mm});
            skLineSegment(sketch, "E956", {"start": v(-29.76, -13.07) * mm, "end": v(-29.56, -13.1) * mm});
            skLineSegment(sketch, "E957", {"start": v(-29.56, -13.1) * mm, "end": v(-29.36, -13.14) * mm});
            skLineSegment(sketch, "E958", {"start": v(-29.36, -13.14) * mm, "end": v(-29.16, -13.17) * mm});
            skLineSegment(sketch, "E959", {"start": v(-29.16, -13.17) * mm, "end": v(-28.97, -13.2) * mm});
            skLineSegment(sketch, "E960", {"start": v(-28.97, -13.2) * mm, "end": v(-28.77, -13.22) * mm});
            skLineSegment(sketch, "E961", {"start": v(-28.77, -13.22) * mm, "end": v(-28.59, -13.24) * mm});
            skLineSegment(sketch, "E962", {"start": v(-28.59, -13.24) * mm, "end": v(-28.4, -13.25) * mm});
            skLineSegment(sketch, "E963", {"start": v(-28.4, -13.25) * mm, "end": v(-28.22, -13.27) * mm});
            skLineSegment(sketch, "E964", {"start": v(-28.22, -13.27) * mm, "end": v(-28.04, -13.28) * mm});
            skLineSegment(sketch, "E965", {"start": v(-28.04, -13.28) * mm, "end": v(-27.87, -13.3) * mm});
            skLineSegment(sketch, "E966", {"start": v(-27.87, -13.3) * mm, "end": v(-27.7, -13.3) * mm});
            skLineSegment(sketch, "E967", {"start": v(-27.7, -13.3) * mm, "end": v(-27.53, -13.3) * mm});
            skLineSegment(sketch, "E968", {"start": v(-27.53, -13.3) * mm, "end": v(-27.43, -13.42) * mm});
            skLineSegment(sketch, "E969", {"start": v(-27.43, -13.42) * mm, "end": v(-27.4, -13.58) * mm});
            skLineSegment(sketch, "E970", {"start": v(-27.4, -13.58) * mm, "end": v(-27.5, -13.72) * mm});
            skLineSegment(sketch, "E971", {"start": v(-27.5, -13.72) * mm, "end": v(-27.6, -13.85) * mm});
            skLineSegment(sketch, "E972", {"start": v(-27.6, -13.85) * mm, "end": v(-27.7, -14) * mm});
            skLineSegment(sketch, "E973", {"start": v(-27.7, -14) * mm, "end": v(-27.8, -14.15) * mm});
            skLineSegment(sketch, "E974", {"start": v(-27.8, -14.15) * mm, "end": v(-27.9, -14.3) * mm});
            skLineSegment(sketch, "E975", {"start": v(-27.9, -14.3) * mm, "end": v(-28, -14.46) * mm});
            skLineSegment(sketch, "E976", {"start": v(-28, -14.46) * mm, "end": v(-28.1, -14.62) * mm});
            skLineSegment(sketch, "E977", {"start": v(-28.1, -14.62) * mm, "end": v(-28.19, -14.78) * mm});
            skLineSegment(sketch, "E978", {"start": v(-28.19, -14.78) * mm, "end": v(-28.29, -14.95) * mm});
            skLineSegment(sketch, "E979", {"start": v(-28.29, -14.95) * mm, "end": v(-28.39, -15.13) * mm});
            skLineSegment(sketch, "E980", {"start": v(-28.39, -15.13) * mm, "end": v(-28.49, -15.3) * mm});
            skLineSegment(sketch, "E981", {"start": v(-28.49, -15.3) * mm, "end": v(-28.58, -15.49) * mm});
            skLineSegment(sketch, "E982", {"start": v(-28.58, -15.49) * mm, "end": v(-28.68, -15.67) * mm});
            skLineSegment(sketch, "E983", {"start": v(-28.68, -15.67) * mm, "end": v(-28.78, -15.86) * mm});
            skLineSegment(sketch, "E984", {"start": v(-28.78, -15.86) * mm, "end": v(-28.88, -16.06) * mm});
            skLineSegment(sketch, "E985", {"start": v(-28.88, -16.06) * mm, "end": v(-28.97, -16.26) * mm});
            skLineSegment(sketch, "E986", {"start": v(-28.97, -16.26) * mm, "end": v(-29.07, -16.46) * mm});
            skLineSegment(sketch, "E987", {"start": v(-29.07, -16.46) * mm, "end": v(-29.16, -16.67) * mm});
            skLineSegment(sketch, "E988", {"start": v(-29.16, -16.67) * mm, "end": v(-29.25, -16.89) * mm});
            skLineSegment(sketch, "E989", {"start": v(-29.25, -16.89) * mm, "end": v(-29.35, -17.1) * mm});
            skLineSegment(sketch, "E990", {"start": v(-29.35, -17.1) * mm, "end": v(-29.44, -17.32) * mm});
            skLineSegment(sketch, "E991", {"start": v(-29.44, -17.32) * mm, "end": v(-29.53, -17.55) * mm});
            skLineSegment(sketch, "E992", {"start": v(-29.53, -17.55) * mm, "end": v(-29.62, -17.78) * mm});
            skLineSegment(sketch, "E993", {"start": v(-29.62, -17.78) * mm, "end": v(-29.7, -18.02) * mm});
            skLineSegment(sketch, "E994", {"start": v(-29.7, -18.02) * mm, "end": v(-29.8, -18.26) * mm});
            skLineSegment(sketch, "E995", {"start": v(-29.8, -18.26) * mm, "end": v(-29.87, -18.5) * mm});
            skLineSegment(sketch, "E996", {"start": v(-29.87, -18.5) * mm, "end": v(-29.9, -18.72) * mm});
            skLineSegment(sketch, "E997", {"start": v(-29.9, -18.72) * mm, "end": v(-29.88, -18.75) * mm});
            skLineSegment(sketch, "E998", {"start": v(-29.88, -18.75) * mm, "end": v(-29.67, -18.82) * mm});
            skLineSegment(sketch, "E999", {"start": v(-29.67, -18.82) * mm, "end": v(-29.42, -18.85) * mm});
            skLineSegment(sketch, "E1000", {"start": v(-29.42, -18.85) * mm, "end": v(-29.16, -18.88) * mm});
            skLineSegment(sketch, "E1001", {"start": v(-29.16, -18.88) * mm, "end": v(-28.91, -18.9) * mm});
            skLineSegment(sketch, "E1002", {"start": v(-28.91, -18.9) * mm, "end": v(-28.67, -18.93) * mm});
            skLineSegment(sketch, "E1003", {"start": v(-28.67, -18.93) * mm, "end": v(-28.42, -18.94) * mm});
            skLineSegment(sketch, "E1004", {"start": v(-28.42, -18.94) * mm, "end": v(-28.19, -18.96) * mm});
            skLineSegment(sketch, "E1005", {"start": v(-28.19, -18.96) * mm, "end": v(-27.95, -18.97) * mm});
            skLineSegment(sketch, "E1006", {"start": v(-27.95, -18.97) * mm, "end": v(-27.72, -18.98) * mm});
            skLineSegment(sketch, "E1007", {"start": v(-27.72, -18.98) * mm, "end": v(-27.49, -18.99) * mm});
            skLineSegment(sketch, "E1008", {"start": v(-27.49, -18.99) * mm, "end": v(-27.26, -18.99) * mm});
            skLineSegment(sketch, "E1009", {"start": v(-27.26, -18.99) * mm, "end": v(-27.04, -18.99) * mm});
            skLineSegment(sketch, "E1010", {"start": v(-27.04, -18.99) * mm, "end": v(-26.82, -18.99) * mm});
            skLineSegment(sketch, "E1011", {"start": v(-26.82, -18.99) * mm, "end": v(-26.6, -18.98) * mm});
            skLineSegment(sketch, "E1012", {"start": v(-26.6, -18.98) * mm, "end": v(-26.4, -18.98) * mm});
            skLineSegment(sketch, "E1013", {"start": v(-26.4, -18.98) * mm, "end": v(-26.19, -18.97) * mm});
            skLineSegment(sketch, "E1014", {"start": v(-26.19, -18.97) * mm, "end": v(-25.99, -18.96) * mm});
            skLineSegment(sketch, "E1015", {"start": v(-25.99, -18.96) * mm, "end": v(-25.79, -18.94) * mm});
            skLineSegment(sketch, "E1016", {"start": v(-25.79, -18.94) * mm, "end": v(-25.6, -18.93) * mm});
            skLineSegment(sketch, "E1017", {"start": v(-25.6, -18.93) * mm, "end": v(-25.4, -18.9) * mm});
            skLineSegment(sketch, "E1018", {"start": v(-25.4, -18.9) * mm, "end": v(-25.2, -18.9) * mm});
            skLineSegment(sketch, "E1019", {"start": v(-25.2, -18.9) * mm, "end": v(-25.03, -18.87) * mm});
            skLineSegment(sketch, "E1020", {"start": v(-25.03, -18.87) * mm, "end": v(-24.85, -18.85) * mm});
            skLineSegment(sketch, "E1021", {"start": v(-24.85, -18.85) * mm, "end": v(-24.67, -18.82) * mm});
            skLineSegment(sketch, "E1022", {"start": v(-24.67, -18.82) * mm, "end": v(-24.5, -18.8) * mm});
            skLineSegment(sketch, "E1023", {"start": v(-24.5, -18.8) * mm, "end": v(-24.33, -18.77) * mm});
            skLineSegment(sketch, "E1024", {"start": v(-24.33, -18.77) * mm, "end": v(-24.17, -18.74) * mm});
            skLineSegment(sketch, "E1025", {"start": v(-24.17, -18.74) * mm, "end": v(-24.04, -18.83) * mm});
            skLineSegment(sketch, "E1026", {"start": v(-24.04, -18.83) * mm, "end": v(-23.98, -18.98) * mm});
            skLineSegment(sketch, "E1027", {"start": v(-23.98, -18.98) * mm, "end": v(-24.05, -19.13) * mm});
            skLineSegment(sketch, "E1028", {"start": v(-24.05, -19.13) * mm, "end": v(-24.11, -19.29) * mm});
            skLineSegment(sketch, "E1029", {"start": v(-24.11, -19.29) * mm, "end": v(-24.18, -19.45) * mm});
            skLineSegment(sketch, "E1030", {"start": v(-24.18, -19.45) * mm, "end": v(-24.24, -19.62) * mm});
            skLineSegment(sketch, "E1031", {"start": v(-24.24, -19.62) * mm, "end": v(-24.3, -19.79) * mm});
            skLineSegment(sketch, "E1032", {"start": v(-24.3, -19.79) * mm, "end": v(-24.37, -19.96) * mm});
            skLineSegment(sketch, "E1033", {"start": v(-24.37, -19.96) * mm, "end": v(-24.44, -20.14) * mm});
            skLineSegment(sketch, "E1034", {"start": v(-24.44, -20.14) * mm, "end": v(-24.5, -20.32) * mm});
            skLineSegment(sketch, "E1035", {"start": v(-24.5, -20.32) * mm, "end": v(-24.56, -20.5) * mm});
            skLineSegment(sketch, "E1036", {"start": v(-24.56, -20.5) * mm, "end": v(-24.62, -20.7) * mm});
            skLineSegment(sketch, "E1037", {"start": v(-24.62, -20.7) * mm, "end": v(-24.68, -20.9) * mm});
            skLineSegment(sketch, "E1038", {"start": v(-24.68, -20.9) * mm, "end": v(-24.74, -21.09) * mm});
            skLineSegment(sketch, "E1039", {"start": v(-24.74, -21.09) * mm, "end": v(-24.8, -21.3) * mm});
            skLineSegment(sketch, "E1040", {"start": v(-24.8, -21.3) * mm, "end": v(-24.85, -21.5) * mm});
            skLineSegment(sketch, "E1041", {"start": v(-24.85, -21.5) * mm, "end": v(-24.9, -21.71) * mm});
            skLineSegment(sketch, "E1042", {"start": v(-24.9, -21.71) * mm, "end": v(-24.96, -21.93) * mm});
            skLineSegment(sketch, "E1043", {"start": v(-24.96, -21.93) * mm, "end": v(-25, -22.15) * mm});
            skLineSegment(sketch, "E1044", {"start": v(-25, -22.15) * mm, "end": v(-25.06, -22.37) * mm});
            skLineSegment(sketch, "E1045", {"start": v(-25.06, -22.37) * mm, "end": v(-25.1, -22.6) * mm});
            skLineSegment(sketch, "E1046", {"start": v(-25.1, -22.6) * mm, "end": v(-25.15, -22.83) * mm});
            skLineSegment(sketch, "E1047", {"start": v(-25.15, -22.83) * mm, "end": v(-25.2, -23.07) * mm});
            skLineSegment(sketch, "E1048", {"start": v(-25.2, -23.07) * mm, "end": v(-25.23, -23.3) * mm});
            skLineSegment(sketch, "E1049", {"start": v(-25.23, -23.3) * mm, "end": v(-25.27, -23.55) * mm});
            skLineSegment(sketch, "E1050", {"start": v(-25.27, -23.55) * mm, "end": v(-25.3, -23.8) * mm});
            skLineSegment(sketch, "E1051", {"start": v(-25.3, -23.8) * mm, "end": v(-25.34, -24.05) * mm});
            skLineSegment(sketch, "E1052", {"start": v(-25.34, -24.05) * mm, "end": v(-25.38, -24.31) * mm});
            skLineSegment(sketch, "E1053", {"start": v(-25.38, -24.31) * mm, "end": v(-25.36, -24.53) * mm});
            skLineSegment(sketch, "E1054", {"start": v(-25.36, -24.53) * mm, "end": v(-25.33, -24.56) * mm});
            skLineSegment(sketch, "E1055", {"start": v(-25.33, -24.56) * mm, "end": v(-25.11, -24.58) * mm});
            skLineSegment(sketch, "E1056", {"start": v(-25.11, -24.58) * mm, "end": v(-24.86, -24.56) * mm});
            skLineSegment(sketch, "E1057", {"start": v(-24.86, -24.56) * mm, "end": v(-24.6, -24.53) * mm});
            skLineSegment(sketch, "E1058", {"start": v(-24.6, -24.53) * mm, "end": v(-24.35, -24.5) * mm});
            skLineSegment(sketch, "E1059", {"start": v(-24.35, -24.5) * mm, "end": v(-24.1, -24.47) * mm});
            skLineSegment(sketch, "E1060", {"start": v(-24.1, -24.47) * mm, "end": v(-23.86, -24.44) * mm});
            skLineSegment(sketch, "E1061", {"start": v(-23.86, -24.44) * mm, "end": v(-23.63, -24.4) * mm});
            skLineSegment(sketch, "E1062", {"start": v(-23.63, -24.4) * mm, "end": v(-23.4, -24.37) * mm});
            skLineSegment(sketch, "E1063", {"start": v(-23.4, -24.37) * mm, "end": v(-23.16, -24.33) * mm});
            skLineSegment(sketch, "E1064", {"start": v(-23.16, -24.33) * mm, "end": v(-22.94, -24.29) * mm});
            skLineSegment(sketch, "E1065", {"start": v(-22.94, -24.29) * mm, "end": v(-22.72, -24.24) * mm});
            skLineSegment(sketch, "E1066", {"start": v(-22.72, -24.24) * mm, "end": v(-22.5, -24.2) * mm});
            skLineSegment(sketch, "E1067", {"start": v(-22.5, -24.2) * mm, "end": v(-22.29, -24.15) * mm});
            skLineSegment(sketch, "E1068", {"start": v(-22.29, -24.15) * mm, "end": v(-22.08, -24.1) * mm});
            skLineSegment(sketch, "E1069", {"start": v(-22.08, -24.1) * mm, "end": v(-21.87, -24.05) * mm});
            skLineSegment(sketch, "E1070", {"start": v(-21.87, -24.05) * mm, "end": v(-21.67, -24) * mm});
            skLineSegment(sketch, "E1071", {"start": v(-21.67, -24) * mm, "end": v(-21.48, -23.94) * mm});
            skLineSegment(sketch, "E1072", {"start": v(-21.48, -23.94) * mm, "end": v(-21.28, -23.89) * mm});
            skLineSegment(sketch, "E1073", {"start": v(-21.28, -23.89) * mm, "end": v(-21.1, -23.83) * mm});
            skLineSegment(sketch, "E1074", {"start": v(-21.1, -23.83) * mm, "end": v(-20.91, -23.78) * mm});
            skLineSegment(sketch, "E1075", {"start": v(-20.91, -23.78) * mm, "end": v(-20.73, -23.72) * mm});
            skLineSegment(sketch, "E1076", {"start": v(-20.73, -23.72) * mm, "end": v(-20.56, -23.66) * mm});
            skLineSegment(sketch, "E1077", {"start": v(-20.56, -23.66) * mm, "end": v(-20.39, -23.6) * mm});
            skLineSegment(sketch, "E1078", {"start": v(-20.39, -23.6) * mm, "end": v(-20.22, -23.54) * mm});
            skLineSegment(sketch, "E1079", {"start": v(-20.22, -23.54) * mm, "end": v(-20.05, -23.48) * mm});
            skLineSegment(sketch, "E1080", {"start": v(-20.05, -23.48) * mm, "end": v(-19.9, -23.42) * mm});
            skLineSegment(sketch, "E1081", {"start": v(-19.9, -23.42) * mm, "end": v(-19.74, -23.36) * mm});
            skLineSegment(sketch, "E1082", {"start": v(-19.74, -23.36) * mm, "end": v(-19.6, -23.42) * mm});
            skLineSegment(sketch, "E1083", {"start": v(-19.6, -23.42) * mm, "end": v(-19.5, -23.55) * mm});
            skLineSegment(sketch, "E1084", {"start": v(-19.5, -23.55) * mm, "end": v(-19.54, -23.71) * mm});
            skLineSegment(sketch, "E1085", {"start": v(-19.54, -23.71) * mm, "end": v(-19.57, -23.88) * mm});
            skLineSegment(sketch, "E1086", {"start": v(-19.57, -23.88) * mm, "end": v(-19.6, -24.05) * mm});
            skLineSegment(sketch, "E1087", {"start": v(-19.6, -24.05) * mm, "end": v(-19.64, -24.23) * mm});
            skLineSegment(sketch, "E1088", {"start": v(-19.64, -24.23) * mm, "end": v(-19.66, -24.4) * mm});
            skLineSegment(sketch, "E1089", {"start": v(-19.66, -24.4) * mm, "end": v(-19.7, -24.6) * mm});
            skLineSegment(sketch, "E1090", {"start": v(-19.7, -24.6) * mm, "end": v(-19.72, -24.78) * mm});
            skLineSegment(sketch, "E1091", {"start": v(-19.72, -24.78) * mm, "end": v(-19.74, -24.97) * mm});
            skLineSegment(sketch, "E1092", {"start": v(-19.74, -24.97) * mm, "end": v(-19.76, -25.16) * mm});
            skLineSegment(sketch, "E1093", {"start": v(-19.76, -25.16) * mm, "end": v(-19.78, -25.36) * mm});
            skLineSegment(sketch, "E1094", {"start": v(-19.78, -25.36) * mm, "end": v(-19.8, -25.57) * mm});
            skLineSegment(sketch, "E1095", {"start": v(-19.8, -25.57) * mm, "end": v(-19.81, -25.77) * mm});
            skLineSegment(sketch, "E1096", {"start": v(-19.81, -25.77) * mm, "end": v(-19.83, -25.98) * mm});
            skLineSegment(sketch, "E1097", {"start": v(-19.83, -25.98) * mm, "end": v(-19.84, -26.2) * mm});
            skLineSegment(sketch, "E1098", {"start": v(-19.84, -26.2) * mm, "end": v(-19.85, -26.42) * mm});
            skLineSegment(sketch, "E1099", {"start": v(-19.85, -26.42) * mm, "end": v(-19.85, -26.64) * mm});
            skLineSegment(sketch, "E1100", {"start": v(-19.85, -26.64) * mm, "end": v(-19.86, -26.86) * mm});
            skLineSegment(sketch, "E1101", {"start": v(-19.86, -26.86) * mm, "end": v(-19.86, -27.1) * mm});
            skLineSegment(sketch, "E1102", {"start": v(-19.86, -27.1) * mm, "end": v(-19.86, -27.33) * mm});
            skLineSegment(sketch, "E1103", {"start": v(-19.86, -27.33) * mm, "end": v(-19.85, -27.56) * mm});
            skLineSegment(sketch, "E1104", {"start": v(-19.85, -27.56) * mm, "end": v(-19.85, -27.8) * mm});
            skLineSegment(sketch, "E1105", {"start": v(-19.85, -27.8) * mm, "end": v(-19.84, -28.04) * mm});
            skLineSegment(sketch, "E1106", {"start": v(-19.84, -28.04) * mm, "end": v(-19.82, -28.3) * mm});
            skLineSegment(sketch, "E1107", {"start": v(-19.82, -28.3) * mm, "end": v(-19.8, -28.54) * mm});
            skLineSegment(sketch, "E1108", {"start": v(-19.8, -28.54) * mm, "end": v(-19.79, -28.8) * mm});
            skLineSegment(sketch, "E1109", {"start": v(-19.79, -28.8) * mm, "end": v(-19.77, -29.05) * mm});
            skLineSegment(sketch, "E1110", {"start": v(-19.77, -29.05) * mm, "end": v(-19.7, -29.26) * mm});
            skLineSegment(sketch, "E1111", {"start": v(-19.7, -29.26) * mm, "end": v(-19.67, -29.29) * mm});
            skLineSegment(sketch, "E1112", {"start": v(-19.67, -29.29) * mm, "end": v(-19.45, -29.27) * mm});
            skLineSegment(sketch, "E1113", {"start": v(-19.45, -29.27) * mm, "end": v(-19.2, -29.19) * mm});
            skLineSegment(sketch, "E1114", {"start": v(-19.2, -29.19) * mm, "end": v(-18.96, -29.11) * mm});
            skLineSegment(sketch, "E1115", {"start": v(-18.96, -29.11) * mm, "end": v(-18.72, -29.03) * mm});
            skLineSegment(sketch, "E1116", {"start": v(-18.72, -29.03) * mm, "end": v(-18.5, -28.95) * mm});
            skLineSegment(sketch, "E1117", {"start": v(-18.5, -28.95) * mm, "end": v(-18.26, -28.87) * mm});
            skLineSegment(sketch, "E1118", {"start": v(-18.26, -28.87) * mm, "end": v(-18.04, -28.78) * mm});
            skLineSegment(sketch, "E1119", {"start": v(-18.04, -28.78) * mm, "end": v(-17.82, -28.7) * mm});
            skLineSegment(sketch, "E1120", {"start": v(-17.82, -28.7) * mm, "end": v(-17.6, -28.61) * mm});
            skLineSegment(sketch, "E1121", {"start": v(-17.6, -28.61) * mm, "end": v(-17.39, -28.52) * mm});
            skLineSegment(sketch, "E1122", {"start": v(-17.39, -28.52) * mm, "end": v(-17.18, -28.43) * mm});
            skLineSegment(sketch, "E1123", {"start": v(-17.18, -28.43) * mm, "end": v(-16.98, -28.34) * mm});
            skLineSegment(sketch, "E1124", {"start": v(-16.98, -28.34) * mm, "end": v(-16.78, -28.26) * mm});
            skLineSegment(sketch, "E1125", {"start": v(-16.78, -28.26) * mm, "end": v(-16.58, -28.16) * mm});
            skLineSegment(sketch, "E1126", {"start": v(-16.58, -28.16) * mm, "end": v(-16.4, -28.07) * mm});
            skLineSegment(sketch, "E1127", {"start": v(-16.4, -28.07) * mm, "end": v(-16.2, -27.98) * mm});
            skLineSegment(sketch, "E1128", {"start": v(-16.2, -27.98) * mm, "end": v(-16.03, -27.89) * mm});
            skLineSegment(sketch, "E1129", {"start": v(-16.03, -27.89) * mm, "end": v(-15.85, -27.8) * mm});
            skLineSegment(sketch, "E1130", {"start": v(-15.85, -27.8) * mm, "end": v(-15.68, -27.7) * mm});
            skLineSegment(sketch, "E1131", {"start": v(-15.68, -27.7) * mm, "end": v(-15.51, -27.6) * mm});
            skLineSegment(sketch, "E1132", {"start": v(-15.51, -27.6) * mm, "end": v(-15.35, -27.51) * mm});
            skLineSegment(sketch, "E1133", {"start": v(-15.35, -27.51) * mm, "end": v(-15.19, -27.42) * mm});
            skLineSegment(sketch, "E1134", {"start": v(-15.19, -27.42) * mm, "end": v(-15.03, -27.32) * mm});
            skLineSegment(sketch, "E1135", {"start": v(-15.03, -27.32) * mm, "end": v(-14.88, -27.23) * mm});
            skLineSegment(sketch, "E1136", {"start": v(-14.88, -27.23) * mm, "end": v(-14.73, -27.14) * mm});
            skLineSegment(sketch, "E1137", {"start": v(-14.73, -27.14) * mm, "end": v(-14.6, -27.04) * mm});
            skLineSegment(sketch, "E1138", {"start": v(-14.6, -27.04) * mm, "end": v(-14.45, -26.95) * mm});
            skLineSegment(sketch, "E1139", {"start": v(-14.45, -26.95) * mm, "end": v(-14.3, -26.98) * mm});
            skLineSegment(sketch, "E1140", {"start": v(-14.3, -26.98) * mm, "end": v(-14.19, -27.1) * mm});
            skLineSegment(sketch, "E1141", {"start": v(-14.19, -27.1) * mm, "end": v(-14.18, -27.26) * mm});
            skLineSegment(sketch, "E1142", {"start": v(-14.18, -27.26) * mm, "end": v(-14.18, -27.43) * mm});
            skLineSegment(sketch, "E1143", {"start": v(-14.18, -27.43) * mm, "end": v(-14.18, -27.6) * mm});
            skLineSegment(sketch, "E1144", {"start": v(-14.18, -27.6) * mm, "end": v(-14.17, -27.78) * mm});
            skLineSegment(sketch, "E1145", {"start": v(-14.17, -27.78) * mm, "end": v(-14.16, -27.96) * mm});
            skLineSegment(sketch, "E1146", {"start": v(-14.16, -27.96) * mm, "end": v(-14.15, -28.15) * mm});
            skLineSegment(sketch, "E1147", {"start": v(-14.15, -28.15) * mm, "end": v(-14.13, -28.34) * mm});
            skLineSegment(sketch, "E1148", {"start": v(-14.13, -28.34) * mm, "end": v(-14.12, -28.53) * mm});
            skLineSegment(sketch, "E1149", {"start": v(-14.12, -28.53) * mm, "end": v(-14.1, -28.72) * mm});
            skLineSegment(sketch, "E1150", {"start": v(-14.1, -28.72) * mm, "end": v(-14.08, -28.92) * mm});
            skLineSegment(sketch, "E1151", {"start": v(-14.08, -28.92) * mm, "end": v(-14.05, -29.12) * mm});
            skLineSegment(sketch, "E1152", {"start": v(-14.05, -29.12) * mm, "end": v(-14.02, -29.33) * mm});
            skLineSegment(sketch, "E1153", {"start": v(-14.02, -29.33) * mm, "end": v(-14, -29.54) * mm});
            skLineSegment(sketch, "E1154", {"start": v(-14, -29.54) * mm, "end": v(-13.96, -29.75) * mm});
            skLineSegment(sketch, "E1155", {"start": v(-13.96, -29.75) * mm, "end": v(-13.92, -29.96) * mm});
            skLineSegment(sketch, "E1156", {"start": v(-13.92, -29.96) * mm, "end": v(-13.88, -30.18) * mm});
            skLineSegment(sketch, "E1157", {"start": v(-13.88, -30.18) * mm, "end": v(-13.84, -30.4) * mm});
            skLineSegment(sketch, "E1158", {"start": v(-13.84, -30.4) * mm, "end": v(-13.8, -30.63) * mm});
            skLineSegment(sketch, "E1159", {"start": v(-13.8, -30.63) * mm, "end": v(-13.74, -30.86) * mm});
            skLineSegment(sketch, "E1160", {"start": v(-13.74, -30.86) * mm, "end": v(-13.69, -31.09) * mm});
            skLineSegment(sketch, "E1161", {"start": v(-13.69, -31.09) * mm, "end": v(-13.63, -31.32) * mm});
            skLineSegment(sketch, "E1162", {"start": v(-13.63, -31.32) * mm, "end": v(-13.57, -31.56) * mm});
            skLineSegment(sketch, "E1163", {"start": v(-13.57, -31.56) * mm, "end": v(-13.5, -31.8) * mm});
            skLineSegment(sketch, "E1164", {"start": v(-13.5, -31.8) * mm, "end": v(-13.44, -32.04) * mm});
            skLineSegment(sketch, "E1165", {"start": v(-13.44, -32.04) * mm, "end": v(-13.37, -32.28) * mm});
            skLineSegment(sketch, "E1166", {"start": v(-13.37, -32.28) * mm, "end": v(-13.3, -32.53) * mm});
            skLineSegment(sketch, "E1167", {"start": v(-13.3, -32.53) * mm, "end": v(-13.19, -32.72) * mm});
            skLineSegment(sketch, "E1168", {"start": v(-13.19, -32.72) * mm, "end": v(-13.15, -32.74) * mm});
            skLineSegment(sketch, "E1169", {"start": v(-13.15, -32.74) * mm, "end": v(-12.94, -32.67) * mm});
            skLineSegment(sketch, "E1170", {"start": v(-12.94, -32.67) * mm, "end": v(-12.72, -32.54) * mm});
            skLineSegment(sketch, "E1171", {"start": v(-12.72, -32.54) * mm, "end": v(-12.5, -32.42) * mm});
            skLineSegment(sketch, "E1172", {"start": v(-12.5, -32.42) * mm, "end": v(-12.28, -32.3) * mm});
            skLineSegment(sketch, "E1173", {"start": v(-12.28, -32.3) * mm, "end": v(-12.07, -32.16) * mm});
            skLineSegment(sketch, "E1174", {"start": v(-12.07, -32.16) * mm, "end": v(-11.86, -32.03) * mm});
            skLineSegment(sketch, "E1175", {"start": v(-11.86, -32.03) * mm, "end": v(-11.66, -31.9) * mm});
            skLineSegment(sketch, "E1176", {"start": v(-11.66, -31.9) * mm, "end": v(-11.46, -31.77) * mm});
            skLineSegment(sketch, "E1177", {"start": v(-11.46, -31.77) * mm, "end": v(-11.27, -31.65) * mm});
            skLineSegment(sketch, "E1178", {"start": v(-11.27, -31.65) * mm, "end": v(-11.08, -31.52) * mm});
            skLineSegment(sketch, "E1179", {"start": v(-11.08, -31.52) * mm, "end": v(-10.9, -31.38) * mm});
            skLineSegment(sketch, "E1180", {"start": v(-10.9, -31.38) * mm, "end": v(-10.71, -31.26) * mm});
            skLineSegment(sketch, "E1181", {"start": v(-10.71, -31.26) * mm, "end": v(-10.54, -31.13) * mm});
            skLineSegment(sketch, "E1182", {"start": v(-10.54, -31.13) * mm, "end": v(-10.37, -31) * mm});
            skLineSegment(sketch, "E1183", {"start": v(-10.37, -31) * mm, "end": v(-10.2, -30.87) * mm});
            skLineSegment(sketch, "E1184", {"start": v(-10.2, -30.87) * mm, "end": v(-10.04, -30.74) * mm});
            skLineSegment(sketch, "E1185", {"start": v(-10.04, -30.74) * mm, "end": v(-9.88, -30.6) * mm});
            skLineSegment(sketch, "E1186", {"start": v(-9.88, -30.6) * mm, "end": v(-9.73, -30.48) * mm});
            skLineSegment(sketch, "E1187", {"start": v(-9.73, -30.48) * mm, "end": v(-9.58, -30.35) * mm});
            skLineSegment(sketch, "E1188", {"start": v(-9.58, -30.35) * mm, "end": v(-9.43, -30.23) * mm});
            skLineSegment(sketch, "E1189", {"start": v(-9.43, -30.23) * mm, "end": v(-9.3, -30.1) * mm});
            skLineSegment(sketch, "E1190", {"start": v(-9.3, -30.1) * mm, "end": v(-9.16, -29.98) * mm});
            skLineSegment(sketch, "E1191", {"start": v(-9.16, -29.98) * mm, "end": v(-9.02, -29.85) * mm});
            skLineSegment(sketch, "E1192", {"start": v(-9.02, -29.85) * mm, "end": v(-8.9, -29.73) * mm});
            skLineSegment(sketch, "E1193", {"start": v(-8.9, -29.73) * mm, "end": v(-8.77, -29.6) * mm});
            skLineSegment(sketch, "E1194", {"start": v(-8.77, -29.6) * mm, "end": v(-8.65, -29.49) * mm});
            skLineSegment(sketch, "E1195", {"start": v(-8.65, -29.49) * mm, "end": v(-8.53, -29.37) * mm});
            skLineSegment(sketch, "E1196", {"start": v(-8.53, -29.37) * mm, "end": v(-8.38, -29.37) * mm});
            skLineSegment(sketch, "E1197", {"start": v(-8.38, -29.37) * mm, "end": v(-8.24, -29.45) * mm});
            skLineSegment(sketch, "E1198", {"start": v(-8.24, -29.45) * mm, "end": v(-8.2, -29.61) * mm});
            skLineSegment(sketch, "E1199", {"start": v(-8.2, -29.61) * mm, "end": v(-8.17, -29.78) * mm});
            skLineSegment(sketch, "E1200", {"start": v(-8.17, -29.78) * mm, "end": v(-8.13, -29.95) * mm});
            skLineSegment(sketch, "E1201", {"start": v(-8.13, -29.95) * mm, "end": v(-8.08, -30.12) * mm});
            skLineSegment(sketch, "E1202", {"start": v(-8.08, -30.12) * mm, "end": v(-8.04, -30.3) * mm});
            skLineSegment(sketch, "E1203", {"start": v(-8.04, -30.3) * mm, "end": v(-7.99, -30.47) * mm});
            skLineSegment(sketch, "E1204", {"start": v(-7.99, -30.47) * mm, "end": v(-7.93, -30.65) * mm});
            skLineSegment(sketch, "E1205", {"start": v(-7.93, -30.65) * mm, "end": v(-7.88, -30.84) * mm});
            skLineSegment(sketch, "E1206", {"start": v(-7.88, -30.84) * mm, "end": v(-7.82, -31.03) * mm});
            skLineSegment(sketch, "E1207", {"start": v(-7.82, -31.03) * mm, "end": v(-7.75, -31.22) * mm});
            skLineSegment(sketch, "E1208", {"start": v(-7.75, -31.22) * mm, "end": v(-7.69, -31.4) * mm});
            skLineSegment(sketch, "E1209", {"start": v(-7.69, -31.4) * mm, "end": v(-7.62, -31.6) * mm});
            skLineSegment(sketch, "E1210", {"start": v(-7.62, -31.6) * mm, "end": v(-7.54, -31.8) * mm});
            skLineSegment(sketch, "E1211", {"start": v(-7.54, -31.8) * mm, "end": v(-7.47, -32) * mm});
            skLineSegment(sketch, "E1212", {"start": v(-7.47, -32) * mm, "end": v(-7.39, -32.2) * mm});
            skLineSegment(sketch, "E1213", {"start": v(-7.39, -32.2) * mm, "end": v(-7.3, -32.41) * mm});
            skLineSegment(sketch, "E1214", {"start": v(-7.3, -32.41) * mm, "end": v(-7.22, -32.62) * mm});
            skLineSegment(sketch, "E1215", {"start": v(-7.22, -32.62) * mm, "end": v(-7.12, -32.83) * mm});
            skLineSegment(sketch, "E1216", {"start": v(-7.12, -32.83) * mm, "end": v(-7.03, -33.04) * mm});
            skLineSegment(sketch, "E1217", {"start": v(-7.03, -33.04) * mm, "end": v(-6.93, -33.25) * mm});
            skLineSegment(sketch, "E1218", {"start": v(-6.93, -33.25) * mm, "end": v(-6.82, -33.47) * mm});
            skLineSegment(sketch, "E1219", {"start": v(-6.82, -33.47) * mm, "end": v(-6.72, -33.69) * mm});
            skLineSegment(sketch, "E1220", {"start": v(-6.72, -33.69) * mm, "end": v(-6.6, -33.9) * mm});
            skLineSegment(sketch, "E1221", {"start": v(-6.6, -33.9) * mm, "end": v(-6.49, -34.13) * mm});
            skLineSegment(sketch, "E1222", {"start": v(-6.49, -34.13) * mm, "end": v(-6.37, -34.36) * mm});
            skLineSegment(sketch, "E1223", {"start": v(-6.37, -34.36) * mm, "end": v(-6.24, -34.58) * mm});
            skLineSegment(sketch, "E1224", {"start": v(-6.24, -34.58) * mm, "end": v(-6.1, -34.75) * mm});
            skLineSegment(sketch, "E1225", {"start": v(-6.1, -34.75) * mm, "end": v(-6.06, -34.75) * mm});
            skLineSegment(sketch, "E1226", {"start": v(-6.06, -34.75) * mm, "end": v(-5.87, -34.65) * mm});
            skLineSegment(sketch, "E1227", {"start": v(-5.87, -34.65) * mm, "end": v(-5.67, -34.48) * mm});
            skLineSegment(sketch, "E1228", {"start": v(-5.67, -34.48) * mm, "end": v(-5.48, -34.3) * mm});
            skLineSegment(sketch, "E1229", {"start": v(-5.48, -34.3) * mm, "end": v(-5.3, -34.14) * mm});
            skLineSegment(sketch, "E1230", {"start": v(-5.3, -34.14) * mm, "end": v(-5.12, -33.97) * mm});
            skLineSegment(sketch, "E1231", {"start": v(-5.12, -33.97) * mm, "end": v(-4.94, -33.8) * mm});
            skLineSegment(sketch, "E1232", {"start": v(-4.94, -33.8) * mm, "end": v(-4.77, -33.63) * mm});
            skLineSegment(sketch, "E1233", {"start": v(-4.77, -33.63) * mm, "end": v(-4.6, -33.46) * mm});
            skLineSegment(sketch, "E1234", {"start": v(-4.6, -33.46) * mm, "end": v(-4.44, -33.3) * mm});
            skLineSegment(sketch, "E1235", {"start": v(-4.44, -33.3) * mm, "end": v(-4.28, -33.13) * mm});
            skLineSegment(sketch, "E1236", {"start": v(-4.28, -33.13) * mm, "end": v(-4.13, -32.96) * mm});
            skLineSegment(sketch, "E1237", {"start": v(-4.13, -32.96) * mm, "end": v(-3.98, -32.8) * mm});
            skLineSegment(sketch, "E1238", {"start": v(-3.98, -32.8) * mm, "end": v(-3.84, -32.64) * mm});
            skLineSegment(sketch, "E1239", {"start": v(-3.84, -32.64) * mm, "end": v(-3.7, -32.47) * mm});
            skLineSegment(sketch, "E1240", {"start": v(-3.7, -32.47) * mm, "end": v(-3.56, -32.31) * mm});
            skLineSegment(sketch, "E1241", {"start": v(-3.56, -32.31) * mm, "end": v(-3.43, -32.15) * mm});
            skLineSegment(sketch, "E1242", {"start": v(-3.43, -32.15) * mm, "end": v(-3.3, -32) * mm});
            skLineSegment(sketch, "E1243", {"start": v(-3.3, -32) * mm, "end": v(-3.18, -31.84) * mm});
            skLineSegment(sketch, "E1244", {"start": v(-3.18, -31.84) * mm, "end": v(-3.06, -31.68) * mm});
            skLineSegment(sketch, "E1245", {"start": v(-3.06, -31.68) * mm, "end": v(-2.94, -31.53) * mm});
            skLineSegment(sketch, "E1246", {"start": v(-2.94, -31.53) * mm, "end": v(-2.83, -31.38) * mm});
            skLineSegment(sketch, "E1247", {"start": v(-2.83, -31.38) * mm, "end": v(-2.72, -31.23) * mm});
            skLineSegment(sketch, "E1248", {"start": v(-2.72, -31.23) * mm, "end": v(-2.62, -31.08) * mm});
            skLineSegment(sketch, "E1249", {"start": v(-2.62, -31.08) * mm, "end": v(-2.52, -30.93) * mm});
            skLineSegment(sketch, "E1250", {"start": v(-2.52, -30.93) * mm, "end": v(-2.42, -30.78) * mm});
            skLineSegment(sketch, "E1251", {"start": v(-2.42, -30.78) * mm, "end": v(-2.33, -30.64) * mm});
            skLineSegment(sketch, "E1252", {"start": v(-2.33, -30.64) * mm, "end": v(-2.24, -30.5) * mm});
            skLineSegment(sketch, "E1253", {"start": v(-2.24, -30.5) * mm, "end": v(-2.09, -30.47) * mm});
            skLineSegment(sketch, "E1254", {"start": v(-2.09, -30.47) * mm, "end": v(-1.94, -30.52) * mm});
            skLineSegment(sketch, "E1255", {"start": v(-1.94, -30.52) * mm, "end": v(-1.87, -30.67) * mm});
            skLineSegment(sketch, "E1256", {"start": v(-1.87, -30.67) * mm, "end": v(-1.8, -30.83) * mm});
            skLineSegment(sketch, "E1257", {"start": v(-1.8, -30.83) * mm, "end": v(-1.72, -30.98) * mm});
            skLineSegment(sketch, "E1258", {"start": v(-1.72, -30.98) * mm, "end": v(-1.64, -31.14) * mm});
            skLineSegment(sketch, "E1259", {"start": v(-1.64, -31.14) * mm, "end": v(-1.56, -31.3) * mm});
            skLineSegment(sketch, "E1260", {"start": v(-1.56, -31.3) * mm, "end": v(-1.48, -31.47) * mm});
            skLineSegment(sketch, "E1261", {"start": v(-1.48, -31.47) * mm, "end": v(-1.39, -31.63) * mm});
            skLineSegment(sketch, "E1262", {"start": v(-1.39, -31.63) * mm, "end": v(-1.3, -31.8) * mm});
            skLineSegment(sketch, "E1263", {"start": v(-1.3, -31.8) * mm, "end": v(-1.2, -31.97) * mm});
            skLineSegment(sketch, "E1264", {"start": v(-1.2, -31.97) * mm, "end": v(-1.1, -32.15) * mm});
            skLineSegment(sketch, "E1265", {"start": v(-1.1, -32.15) * mm, "end": v(-0.99, -32.32) * mm});
            skLineSegment(sketch, "E1266", {"start": v(-0.99, -32.32) * mm, "end": v(-0.88, -32.5) * mm});
            skLineSegment(sketch, "E1267", {"start": v(-0.88, -32.5) * mm, "end": v(-0.77, -32.67) * mm});
            skLineSegment(sketch, "E1268", {"start": v(-0.77, -32.67) * mm, "end": v(-0.65, -32.86) * mm});
            skLineSegment(sketch, "E1269", {"start": v(-0.65, -32.86) * mm, "end": v(-0.53, -33.04) * mm});
            skLineSegment(sketch, "E1270", {"start": v(-0.53, -33.04) * mm, "end": v(-0.4, -33.22) * mm});
            skLineSegment(sketch, "E1271", {"start": v(-0.4, -33.22) * mm, "end": v(-0.28, -33.4) * mm});
            skLineSegment(sketch, "E1272", {"start": v(-0.28, -33.4) * mm, "end": v(-0.14, -33.6) * mm});
            skLineSegment(sketch, "E1273", {"start": v(-0.14, -33.6) * mm, "end": v(0, -33.78) * mm});
            skLineSegment(sketch, "E1274", {"start": v(0, -33.78) * mm, "end": v(0.14, -33.97) * mm});
            skLineSegment(sketch, "E1275", {"start": v(0.14, -33.97) * mm, "end": v(0.29, -34.16) * mm});
            skLineSegment(sketch, "E1276", {"start": v(0.29, -34.16) * mm, "end": v(0.44, -34.35) * mm});
            skLineSegment(sketch, "E1277", {"start": v(0.44, -34.35) * mm, "end": v(0.6, -34.54) * mm});
            skLineSegment(sketch, "E1278", {"start": v(0.6, -34.54) * mm, "end": v(0.75, -34.73) * mm});
            skLineSegment(sketch, "E1279", {"start": v(0.75, -34.73) * mm, "end": v(0.92, -34.93) * mm});
            skLineSegment(sketch, "E1280", {"start": v(0.92, -34.93) * mm, "end": v(1.09, -35.12) * mm});
            skLineSegment(sketch, "E1281", {"start": v(1.09, -35.12) * mm, "end": v(1.26, -35.26) * mm});
            skLineSegment(sketch, "E1282", {"start": v(1.26, -35.26) * mm, "end": v(1.3, -35.25) * mm});
            skLineSegment(sketch, "E1283", {"start": v(1.3, -35.25) * mm, "end": v(1.46, -35.1) * mm});
            skLineSegment(sketch, "E1284", {"start": v(1.46, -35.1) * mm, "end": v(1.62, -34.9) * mm});
            skLineSegment(sketch, "E1285", {"start": v(1.62, -34.9) * mm, "end": v(1.77, -34.7) * mm});
            skLineSegment(sketch, "E1286", {"start": v(1.77, -34.7) * mm, "end": v(1.92, -34.5) * mm});
            skLineSegment(sketch, "E1287", {"start": v(1.92, -34.5) * mm, "end": v(2.06, -34.29) * mm});
            skLineSegment(sketch, "E1288", {"start": v(2.06, -34.29) * mm, "end": v(2.2, -34.09) * mm});
            skLineSegment(sketch, "E1289", {"start": v(2.2, -34.09) * mm, "end": v(2.33, -33.89) * mm});
            skLineSegment(sketch, "E1290", {"start": v(2.33, -33.89) * mm, "end": v(2.45, -33.69) * mm});
            skLineSegment(sketch, "E1291", {"start": v(2.45, -33.69) * mm, "end": v(2.58, -33.5) * mm});
            skLineSegment(sketch, "E1292", {"start": v(2.58, -33.5) * mm, "end": v(2.7, -33.3) * mm});
            skLineSegment(sketch, "E1293", {"start": v(2.7, -33.3) * mm, "end": v(2.81, -33.1) * mm});
            skLineSegment(sketch, "E1294", {"start": v(2.81, -33.1) * mm, "end": v(2.93, -32.91) * mm});
            skLineSegment(sketch, "E1295", {"start": v(2.93, -32.91) * mm, "end": v(3.03, -32.72) * mm});
            skLineSegment(sketch, "E1296", {"start": v(3.03, -32.72) * mm, "end": v(3.14, -32.53) * mm});
            skLineSegment(sketch, "E1297", {"start": v(3.14, -32.53) * mm, "end": v(3.24, -32.35) * mm});
            skLineSegment(sketch, "E1298", {"start": v(3.24, -32.35) * mm, "end": v(3.33, -32.16) * mm});
            skLineSegment(sketch, "E1299", {"start": v(3.33, -32.16) * mm, "end": v(3.42, -31.98) * mm});
            skLineSegment(sketch, "E1300", {"start": v(3.42, -31.98) * mm, "end": v(3.51, -31.8) * mm});
            skLineSegment(sketch, "E1301", {"start": v(3.51, -31.8) * mm, "end": v(3.6, -31.62) * mm});
            skLineSegment(sketch, "E1302", {"start": v(3.6, -31.62) * mm, "end": v(3.68, -31.45) * mm});
            skLineSegment(sketch, "E1303", {"start": v(3.68, -31.45) * mm, "end": v(3.76, -31.28) * mm});
            skLineSegment(sketch, "E1304", {"start": v(3.76, -31.28) * mm, "end": v(3.83, -31.1) * mm});
            skLineSegment(sketch, "E1305", {"start": v(3.83, -31.1) * mm, "end": v(3.9, -30.94) * mm});
            skLineSegment(sketch, "E1306", {"start": v(3.9, -30.94) * mm, "end": v(3.97, -30.78) * mm});
            skLineSegment(sketch, "E1307", {"start": v(3.97, -30.78) * mm, "end": v(4.03, -30.61) * mm});
            skLineSegment(sketch, "E1308", {"start": v(4.03, -30.61) * mm, "end": v(4.1, -30.45) * mm});
            skLineSegment(sketch, "E1309", {"start": v(4.1, -30.45) * mm, "end": v(4.15, -30.3) * mm});
            skLineSegment(sketch, "E1310", {"start": v(4.15, -30.3) * mm, "end": v(4.3, -30.23) * mm});
            skLineSegment(sketch, "E1311", {"start": v(4.3, -30.23) * mm, "end": v(4.45, -30.26) * mm});
            skLineSegment(sketch, "E1312", {"start": v(4.45, -30.26) * mm, "end": v(4.55, -30.39) * mm});
            skLineSegment(sketch, "E1313", {"start": v(4.55, -30.39) * mm, "end": v(4.65, -30.53) * mm});
            skLineSegment(sketch, "E1314", {"start": v(4.65, -30.53) * mm, "end": v(4.76, -30.66) * mm});
            skLineSegment(sketch, "E1315", {"start": v(4.76, -30.66) * mm, "end": v(4.87, -30.8) * mm});
            skLineSegment(sketch, "E1316", {"start": v(4.87, -30.8) * mm, "end": v(4.98, -30.95) * mm});
            skLineSegment(sketch, "E1317", {"start": v(4.98, -30.95) * mm, "end": v(5.1, -31.09) * mm});
            skLineSegment(sketch, "E1318", {"start": v(5.1, -31.09) * mm, "end": v(5.22, -31.23) * mm});
            skLineSegment(sketch, "E1319", {"start": v(5.22, -31.23) * mm, "end": v(5.35, -31.38) * mm});
            skLineSegment(sketch, "E1320", {"start": v(5.35, -31.38) * mm, "end": v(5.48, -31.52) * mm});
            skLineSegment(sketch, "E1321", {"start": v(5.48, -31.52) * mm, "end": v(5.61, -31.67) * mm});
            skLineSegment(sketch, "E1322", {"start": v(5.61, -31.67) * mm, "end": v(5.75, -31.82) * mm});
            skLineSegment(sketch, "E1323", {"start": v(5.75, -31.82) * mm, "end": v(5.9, -31.97) * mm});
            skLineSegment(sketch, "E1324", {"start": v(5.9, -31.97) * mm, "end": v(6.04, -32.12) * mm});
            skLineSegment(sketch, "E1325", {"start": v(6.04, -32.12) * mm, "end": v(6.2, -32.27) * mm});
            skLineSegment(sketch, "E1326", {"start": v(6.2, -32.27) * mm, "end": v(6.35, -32.43) * mm});
            skLineSegment(sketch, "E1327", {"start": v(6.35, -32.43) * mm, "end": v(6.5, -32.58) * mm});
            skLineSegment(sketch, "E1328", {"start": v(6.5, -32.58) * mm, "end": v(6.68, -32.73) * mm});
            skLineSegment(sketch, "E1329", {"start": v(6.68, -32.73) * mm, "end": v(6.84, -32.89) * mm});
            skLineSegment(sketch, "E1330", {"start": v(6.84, -32.89) * mm, "end": v(7.02, -33.04) * mm});
            skLineSegment(sketch, "E1331", {"start": v(7.02, -33.04) * mm, "end": v(7.2, -33.2) * mm});
            skLineSegment(sketch, "E1332", {"start": v(7.2, -33.2) * mm, "end": v(7.38, -33.35) * mm});
            skLineSegment(sketch, "E1333", {"start": v(7.38, -33.35) * mm, "end": v(7.57, -33.5) * mm});
            skLineSegment(sketch, "E1334", {"start": v(7.57, -33.5) * mm, "end": v(7.76, -33.66) * mm});
            skLineSegment(sketch, "E1335", {"start": v(7.76, -33.66) * mm, "end": v(7.96, -33.82) * mm});
            skLineSegment(sketch, "E1336", {"start": v(7.96, -33.82) * mm, "end": v(8.16, -33.98) * mm});
            skLineSegment(sketch, "E1337", {"start": v(8.16, -33.98) * mm, "end": v(8.37, -34.13) * mm});
            skLineSegment(sketch, "E1338", {"start": v(8.37, -34.13) * mm, "end": v(8.56, -34.22) * mm});
            skLineSegment(sketch, "E1339", {"start": v(8.56, -34.22) * mm, "end": v(8.6, -34.21) * mm});
            skLineSegment(sketch, "E1340", {"start": v(8.6, -34.21) * mm, "end": v(8.73, -34.04) * mm});
            skLineSegment(sketch, "E1341", {"start": v(8.73, -34.04) * mm, "end": v(8.84, -33.8) * mm});
            skLineSegment(sketch, "E1342", {"start": v(8.84, -33.8) * mm, "end": v(8.94, -33.57) * mm});
            skLineSegment(sketch, "E1343", {"start": v(8.94, -33.57) * mm, "end": v(9.05, -33.34) * mm});
            skLineSegment(sketch, "E1344", {"start": v(9.05, -33.34) * mm, "end": v(9.14, -33.11) * mm});
            skLineSegment(sketch, "E1345", {"start": v(9.14, -33.11) * mm, "end": v(9.23, -32.89) * mm});
            skLineSegment(sketch, "E1346", {"start": v(9.23, -32.89) * mm, "end": v(9.32, -32.66) * mm});
            skLineSegment(sketch, "E1347", {"start": v(9.32, -32.66) * mm, "end": v(9.4, -32.44) * mm});
            skLineSegment(sketch, "E1348", {"start": v(9.4, -32.44) * mm, "end": v(9.48, -32.22) * mm});
            skLineSegment(sketch, "E1349", {"start": v(9.48, -32.22) * mm, "end": v(9.56, -32) * mm});
            skLineSegment(sketch, "E1350", {"start": v(9.56, -32) * mm, "end": v(9.64, -31.8) * mm});
            skLineSegment(sketch, "E1351", {"start": v(9.64, -31.8) * mm, "end": v(9.7, -31.58) * mm});
            skLineSegment(sketch, "E1352", {"start": v(9.7, -31.58) * mm, "end": v(9.77, -31.38) * mm});
            skLineSegment(sketch, "E1353", {"start": v(9.77, -31.38) * mm, "end": v(9.83, -31.17) * mm});
            skLineSegment(sketch, "E1354", {"start": v(9.83, -31.17) * mm, "end": v(9.9, -30.97) * mm});
            skLineSegment(sketch, "E1355", {"start": v(9.9, -30.97) * mm, "end": v(9.95, -30.77) * mm});
            skLineSegment(sketch, "E1356", {"start": v(9.95, -30.77) * mm, "end": v(10, -30.57) * mm});
            skLineSegment(sketch, "E1357", {"start": v(10, -30.57) * mm, "end": v(10.05, -30.38) * mm});
            skLineSegment(sketch, "E1358", {"start": v(10.05, -30.38) * mm, "end": v(10.1, -30.19) * mm});
            skLineSegment(sketch, "E1359", {"start": v(10.1, -30.19) * mm, "end": v(10.14, -30) * mm});
            skLineSegment(sketch, "E1360", {"start": v(10.14, -30) * mm, "end": v(10.18, -29.81) * mm});
            skLineSegment(sketch, "E1361", {"start": v(10.18, -29.81) * mm, "end": v(10.21, -29.63) * mm});
            skLineSegment(sketch, "E1362", {"start": v(10.21, -29.63) * mm, "end": v(10.25, -29.45) * mm});
            skLineSegment(sketch, "E1363", {"start": v(10.25, -29.45) * mm, "end": v(10.28, -29.28) * mm});
            skLineSegment(sketch, "E1364", {"start": v(10.28, -29.28) * mm, "end": v(10.3, -29.1) * mm});
            skLineSegment(sketch, "E1365", {"start": v(10.3, -29.1) * mm, "end": v(10.33, -28.94) * mm});
            skLineSegment(sketch, "E1366", {"start": v(10.33, -28.94) * mm, "end": v(10.36, -28.77) * mm});
            skLineSegment(sketch, "E1367", {"start": v(10.36, -28.77) * mm, "end": v(10.48, -28.68) * mm});
            skLineSegment(sketch, "E1368", {"start": v(10.48, -28.68) * mm, "end": v(10.64, -28.67) * mm});
            skLineSegment(sketch, "E1369", {"start": v(10.64, -28.67) * mm, "end": v(10.77, -28.78) * mm});
            skLineSegment(sketch, "E1370", {"start": v(10.77, -28.78) * mm, "end": v(10.9, -28.9) * mm});
            skLineSegment(sketch, "E1371", {"start": v(10.9, -28.9) * mm, "end": v(11.03, -29) * mm});
            skLineSegment(sketch, "E1372", {"start": v(11.03, -29) * mm, "end": v(11.16, -29.12) * mm});
            skLineSegment(sketch, "E1373", {"start": v(11.16, -29.12) * mm, "end": v(11.3, -29.23) * mm});
            skLineSegment(sketch, "E1374", {"start": v(11.3, -29.23) * mm, "end": v(11.45, -29.35) * mm});
            skLineSegment(sketch, "E1375", {"start": v(11.45, -29.35) * mm, "end": v(11.6, -29.46) * mm});
            skLineSegment(sketch, "E1376", {"start": v(11.6, -29.46) * mm, "end": v(11.75, -29.58) * mm});
            skLineSegment(sketch, "E1377", {"start": v(11.75, -29.58) * mm, "end": v(11.91, -29.7) * mm});
            skLineSegment(sketch, "E1378", {"start": v(11.91, -29.7) * mm, "end": v(12.07, -29.81) * mm});
            skLineSegment(sketch, "E1379", {"start": v(12.07, -29.81) * mm, "end": v(12.24, -29.93) * mm});
            skLineSegment(sketch, "E1380", {"start": v(12.24, -29.93) * mm, "end": v(12.41, -30.05) * mm});
            skLineSegment(sketch, "E1381", {"start": v(12.41, -30.05) * mm, "end": v(12.59, -30.16) * mm});
            skLineSegment(sketch, "E1382", {"start": v(12.59, -30.16) * mm, "end": v(12.77, -30.28) * mm});
            skLineSegment(sketch, "E1383", {"start": v(12.77, -30.28) * mm, "end": v(12.95, -30.4) * mm});
            skLineSegment(sketch, "E1384", {"start": v(12.95, -30.4) * mm, "end": v(13.14, -30.51) * mm});
            skLineSegment(sketch, "E1385", {"start": v(13.14, -30.51) * mm, "end": v(13.34, -30.63) * mm});
            skLineSegment(sketch, "E1386", {"start": v(13.34, -30.63) * mm, "end": v(13.53, -30.74) * mm});
            skLineSegment(sketch, "E1387", {"start": v(13.53, -30.74) * mm, "end": v(13.73, -30.86) * mm});
            skLineSegment(sketch, "E1388", {"start": v(13.73, -30.86) * mm, "end": v(13.94, -30.97) * mm});
            skLineSegment(sketch, "E1389", {"start": v(13.94, -30.97) * mm, "end": v(14.15, -31.09) * mm});
            skLineSegment(sketch, "E1390", {"start": v(14.15, -31.09) * mm, "end": v(14.37, -31.2) * mm});
            skLineSegment(sketch, "E1391", {"start": v(14.37, -31.2) * mm, "end": v(14.59, -31.31) * mm});
            skLineSegment(sketch, "E1392", {"start": v(14.59, -31.31) * mm, "end": v(14.82, -31.43) * mm});
            skLineSegment(sketch, "E1393", {"start": v(14.82, -31.43) * mm, "end": v(15.05, -31.54) * mm});
            skLineSegment(sketch, "E1394", {"start": v(15.05, -31.54) * mm, "end": v(15.28, -31.65) * mm});
            skLineSegment(sketch, "E1395", {"start": v(15.28, -31.65) * mm, "end": v(15.49, -31.7) * mm});
            skLineSegment(sketch, "E1396", {"start": v(15.49, -31.7) * mm, "end": v(15.53, -31.68) * mm});
            skLineSegment(sketch, "E1397", {"start": v(15.53, -31.68) * mm, "end": v(15.62, -31.48) * mm});
            skLineSegment(sketch, "E1398", {"start": v(15.62, -31.48) * mm, "end": v(15.68, -31.23) * mm});
            skLineSegment(sketch, "E1399", {"start": v(15.68, -31.23) * mm, "end": v(15.73, -30.98) * mm});
            skLineSegment(sketch, "E1400", {"start": v(15.73, -30.98) * mm, "end": v(15.78, -30.73) * mm});
            skLineSegment(sketch, "E1401", {"start": v(15.78, -30.73) * mm, "end": v(15.83, -30.49) * mm});
            skLineSegment(sketch, "E1402", {"start": v(15.83, -30.49) * mm, "end": v(15.87, -30.25) * mm});
            skLineSegment(sketch, "E1403", {"start": v(15.87, -30.25) * mm, "end": v(15.9, -30.01) * mm});
            skLineSegment(sketch, "E1404", {"start": v(15.9, -30.01) * mm, "end": v(15.95, -29.78) * mm});
            skLineSegment(sketch, "E1405", {"start": v(15.95, -29.78) * mm, "end": v(15.98, -29.55) * mm});
            skLineSegment(sketch, "E1406", {"start": v(15.98, -29.55) * mm, "end": v(16, -29.32) * mm});
            skLineSegment(sketch, "E1407", {"start": v(16, -29.32) * mm, "end": v(16.03, -29.1) * mm});
            skLineSegment(sketch, "E1408", {"start": v(16.03, -29.1) * mm, "end": v(16.06, -28.88) * mm});
            skLineSegment(sketch, "E1409", {"start": v(16.06, -28.88) * mm, "end": v(16.08, -28.66) * mm});
            skLineSegment(sketch, "E1410", {"start": v(16.08, -28.66) * mm, "end": v(16.1, -28.44) * mm});
            skLineSegment(sketch, "E1411", {"start": v(16.1, -28.44) * mm, "end": v(16.11, -28.23) * mm});
            skLineSegment(sketch, "E1412", {"start": v(16.11, -28.23) * mm, "end": v(16.13, -28.03) * mm});
            skLineSegment(sketch, "E1413", {"start": v(16.13, -28.03) * mm, "end": v(16.14, -27.82) * mm});
            skLineSegment(sketch, "E1414", {"start": v(16.14, -27.82) * mm, "end": v(16.14, -27.62) * mm});
            skLineSegment(sketch, "E1415", {"start": v(16.14, -27.62) * mm, "end": v(16.15, -27.43) * mm});
            skLineSegment(sketch, "E1416", {"start": v(16.15, -27.43) * mm, "end": v(16.15, -27.24) * mm});
            skLineSegment(sketch, "E1417", {"start": v(16.15, -27.24) * mm, "end": v(16.15, -27.05) * mm});
            skLineSegment(sketch, "E1418", {"start": v(16.15, -27.05) * mm, "end": v(16.15, -26.86) * mm});
            skLineSegment(sketch, "E1419", {"start": v(16.15, -26.86) * mm, "end": v(16.15, -26.68) * mm});
            skLineSegment(sketch, "E1420", {"start": v(16.15, -26.68) * mm, "end": v(16.14, -26.5) * mm});
            skLineSegment(sketch, "E1421", {"start": v(16.14, -26.5) * mm, "end": v(16.13, -26.33) * mm});
            skLineSegment(sketch, "E1422", {"start": v(16.13, -26.33) * mm, "end": v(16.12, -26.16) * mm});
            skLineSegment(sketch, "E1423", {"start": v(16.12, -26.16) * mm, "end": v(16.11, -26) * mm});
            skLineSegment(sketch, "E1424", {"start": v(16.11, -26) * mm, "end": v(16.22, -25.87) * mm});
            skLineSegment(sketch, "E1425", {"start": v(16.22, -25.87) * mm, "end": v(16.37, -25.83) * mm});
            skLineSegment(sketch, "E1426", {"start": v(16.37, -25.83) * mm, "end": v(16.51, -25.91) * mm});
            skLineSegment(sketch, "E1427", {"start": v(16.51, -25.91) * mm, "end": v(16.66, -26) * mm});
            skLineSegment(sketch, "E1428", {"start": v(16.66, -26) * mm, "end": v(16.82, -26.08) * mm});
            skLineSegment(sketch, "E1429", {"start": v(16.82, -26.08) * mm, "end": v(16.97, -26.16) * mm});
            skLineSegment(sketch, "E1430", {"start": v(16.97, -26.16) * mm, "end": v(17.14, -26.24) * mm});
            skLineSegment(sketch, "E1431", {"start": v(17.14, -26.24) * mm, "end": v(17.3, -26.33) * mm});
            skLineSegment(sketch, "E1432", {"start": v(17.3, -26.33) * mm, "end": v(17.47, -26.4) * mm});
            skLineSegment(sketch, "E1433", {"start": v(17.47, -26.4) * mm, "end": v(17.65, -26.49) * mm});
            skLineSegment(sketch, "E1434", {"start": v(17.65, -26.49) * mm, "end": v(17.83, -26.57) * mm});
            skLineSegment(sketch, "E1435", {"start": v(17.83, -26.57) * mm, "end": v(18, -26.65) * mm});
            skLineSegment(sketch, "E1436", {"start": v(18, -26.65) * mm, "end": v(18.2, -26.73) * mm});
            skLineSegment(sketch, "E1437", {"start": v(18.2, -26.73) * mm, "end": v(18.39, -26.8) * mm});
            skLineSegment(sketch, "E1438", {"start": v(18.39, -26.8) * mm, "end": v(18.58, -26.89) * mm});
            skLineSegment(sketch, "E1439", {"start": v(18.58, -26.89) * mm, "end": v(18.78, -26.96) * mm});
            skLineSegment(sketch, "E1440", {"start": v(18.78, -26.96) * mm, "end": v(18.99, -27.04) * mm});
            skLineSegment(sketch, "E1441", {"start": v(18.99, -27.04) * mm, "end": v(19.2, -27.11) * mm});
            skLineSegment(sketch, "E1442", {"start": v(19.2, -27.11) * mm, "end": v(19.41, -27.19) * mm});
            skLineSegment(sketch, "E1443", {"start": v(19.41, -27.19) * mm, "end": v(19.63, -27.26) * mm});
            skLineSegment(sketch, "E1444", {"start": v(19.63, -27.26) * mm, "end": v(19.85, -27.33) * mm});
            skLineSegment(sketch, "E1445", {"start": v(19.85, -27.33) * mm, "end": v(20.08, -27.4) * mm});
            skLineSegment(sketch, "E1446", {"start": v(20.08, -27.4) * mm, "end": v(20.3, -27.47) * mm});
            skLineSegment(sketch, "E1447", {"start": v(20.3, -27.47) * mm, "end": v(20.54, -27.53) * mm});
            skLineSegment(sketch, "E1448", {"start": v(20.54, -27.53) * mm, "end": v(20.78, -27.6) * mm});
            skLineSegment(sketch, "E1449", {"start": v(20.78, -27.6) * mm, "end": v(21.02, -27.66) * mm});
            skLineSegment(sketch, "E1450", {"start": v(21.02, -27.66) * mm, "end": v(21.27, -27.72) * mm});
            skLineSegment(sketch, "E1451", {"start": v(21.27, -27.72) * mm, "end": v(21.53, -27.78) * mm});
            skLineSegment(sketch, "E1452", {"start": v(21.53, -27.78) * mm, "end": v(21.74, -27.78) * mm});
            skLineSegment(sketch, "E1453", {"start": v(21.74, -27.78) * mm, "end": v(21.77, -27.76) * mm});
            skLineSegment(sketch, "E1454", {"start": v(21.77, -27.76) * mm, "end": v(21.82, -27.54) * mm});
            skLineSegment(sketch, "E1455", {"start": v(21.82, -27.54) * mm, "end": v(21.83, -27.29) * mm});
            skLineSegment(sketch, "E1456", {"start": v(21.83, -27.29) * mm, "end": v(21.83, -27.03) * mm});
            skLineSegment(sketch, "E1457", {"start": v(21.83, -27.03) * mm, "end": v(21.82, -26.78) * mm});
            skLineSegment(sketch, "E1458", {"start": v(21.82, -26.78) * mm, "end": v(21.82, -26.53) * mm});
            skLineSegment(sketch, "E1459", {"start": v(21.82, -26.53) * mm, "end": v(21.81, -26.29) * mm});
            skLineSegment(sketch, "E1460", {"start": v(21.81, -26.29) * mm, "end": v(21.8, -26.05) * mm});
            skLineSegment(sketch, "E1461", {"start": v(21.8, -26.05) * mm, "end": v(21.79, -25.81) * mm});
            skLineSegment(sketch, "E1462", {"start": v(21.79, -25.81) * mm, "end": v(21.77, -25.58) * mm});
            skLineSegment(sketch, "E1463", {"start": v(21.77, -25.58) * mm, "end": v(21.75, -25.35) * mm});
            skLineSegment(sketch, "E1464", {"start": v(21.75, -25.35) * mm, "end": v(21.73, -25.13) * mm});
            skLineSegment(sketch, "E1465", {"start": v(21.73, -25.13) * mm, "end": v(21.71, -24.9) * mm});
            skLineSegment(sketch, "E1466", {"start": v(21.71, -24.9) * mm, "end": v(21.69, -24.69) * mm});
            skLineSegment(sketch, "E1467", {"start": v(21.69, -24.69) * mm, "end": v(21.66, -24.48) * mm});
            skLineSegment(sketch, "E1468", {"start": v(21.66, -24.48) * mm, "end": v(21.63, -24.27) * mm});
            skLineSegment(sketch, "E1469", {"start": v(21.63, -24.27) * mm, "end": v(21.6, -24.06) * mm});
            skLineSegment(sketch, "E1470", {"start": v(21.6, -24.06) * mm, "end": v(21.57, -23.86) * mm});
            skLineSegment(sketch, "E1471", {"start": v(21.57, -23.86) * mm, "end": v(21.53, -23.66) * mm});
            skLineSegment(sketch, "E1472", {"start": v(21.53, -23.66) * mm, "end": v(21.5, -23.47) * mm});
            skLineSegment(sketch, "E1473", {"start": v(21.5, -23.47) * mm, "end": v(21.46, -23.28) * mm});
            skLineSegment(sketch, "E1474", {"start": v(21.46, -23.28) * mm, "end": v(21.42, -23.1) * mm});
            skLineSegment(sketch, "E1475", {"start": v(21.42, -23.1) * mm, "end": v(21.38, -22.92) * mm});
            skLineSegment(sketch, "E1476", {"start": v(21.38, -22.92) * mm, "end": v(21.34, -22.74) * mm});
            skLineSegment(sketch, "E1477", {"start": v(21.34, -22.74) * mm, "end": v(21.3, -22.57) * mm});
            skLineSegment(sketch, "E1478", {"start": v(21.3, -22.57) * mm, "end": v(21.25, -22.4) * mm});
            skLineSegment(sketch, "E1479", {"start": v(21.25, -22.4) * mm, "end": v(21.21, -22.23) * mm});
            skLineSegment(sketch, "E1480", {"start": v(21.21, -22.23) * mm, "end": v(21.17, -22.07) * mm});
            skLineSegment(sketch, "E1481", {"start": v(21.17, -22.07) * mm, "end": v(21.24, -21.94) * mm});
            skLineSegment(sketch, "E1482", {"start": v(21.24, -21.94) * mm, "end": v(21.38, -21.86) * mm});
            skLineSegment(sketch, "E1483", {"start": v(21.38, -21.86) * mm, "end": v(21.54, -21.91) * mm});
            skLineSegment(sketch, "E1484", {"start": v(21.54, -21.91) * mm, "end": v(21.7, -21.96) * mm});
            skLineSegment(sketch, "E1485", {"start": v(21.7, -21.96) * mm, "end": v(21.87, -22.01) * mm});
            skLineSegment(sketch, "E1486", {"start": v(21.87, -22.01) * mm, "end": v(22.04, -22.06) * mm});
            skLineSegment(sketch, "E1487", {"start": v(22.04, -22.06) * mm, "end": v(22.22, -22.1) * mm});
            skLineSegment(sketch, "E1488", {"start": v(22.22, -22.1) * mm, "end": v(22.4, -22.15) * mm});
            skLineSegment(sketch, "E1489", {"start": v(22.4, -22.15) * mm, "end": v(22.58, -22.2) * mm});
            skLineSegment(sketch, "E1490", {"start": v(22.58, -22.2) * mm, "end": v(22.77, -22.24) * mm});
            skLineSegment(sketch, "E1491", {"start": v(22.77, -22.24) * mm, "end": v(22.96, -22.28) * mm});
            skLineSegment(sketch, "E1492", {"start": v(22.96, -22.28) * mm, "end": v(23.16, -22.32) * mm});
            skLineSegment(sketch, "E1493", {"start": v(23.16, -22.32) * mm, "end": v(23.36, -22.36) * mm});
            skLineSegment(sketch, "E1494", {"start": v(23.36, -22.36) * mm, "end": v(23.56, -22.4) * mm});
            skLineSegment(sketch, "E1495", {"start": v(23.56, -22.4) * mm, "end": v(23.77, -22.43) * mm});
            skLineSegment(sketch, "E1496", {"start": v(23.77, -22.43) * mm, "end": v(23.98, -22.47) * mm});
            skLineSegment(sketch, "E1497", {"start": v(23.98, -22.47) * mm, "end": v(24.2, -22.5) * mm});
            skLineSegment(sketch, "E1498", {"start": v(24.2, -22.5) * mm, "end": v(24.42, -22.53) * mm});
            skLineSegment(sketch, "E1499", {"start": v(24.42, -22.53) * mm, "end": v(24.64, -22.56) * mm});
            skLineSegment(sketch, "E1500", {"start": v(24.64, -22.56) * mm, "end": v(24.87, -22.58) * mm});
            skLineSegment(sketch, "E1501", {"start": v(24.87, -22.58) * mm, "end": v(25.1, -22.6) * mm});
            skLineSegment(sketch, "E1502", {"start": v(25.1, -22.6) * mm, "end": v(25.34, -22.63) * mm});
            skLineSegment(sketch, "E1503", {"start": v(25.34, -22.63) * mm, "end": v(25.57, -22.64) * mm});
            skLineSegment(sketch, "E1504", {"start": v(25.57, -22.64) * mm, "end": v(25.82, -22.66) * mm});
            skLineSegment(sketch, "E1505", {"start": v(25.82, -22.66) * mm, "end": v(26.07, -22.67) * mm});
            skLineSegment(sketch, "E1506", {"start": v(26.07, -22.67) * mm, "end": v(26.32, -22.68) * mm});
            skLineSegment(sketch, "E1507", {"start": v(26.32, -22.68) * mm, "end": v(26.57, -22.7) * mm});
            skLineSegment(sketch, "E1508", {"start": v(26.57, -22.7) * mm, "end": v(26.83, -22.7) * mm});
            skLineSegment(sketch, "E1509", {"start": v(26.83, -22.7) * mm, "end": v(27.04, -22.66) * mm});
            skLineSegment(sketch, "E1510", {"start": v(27.04, -22.66) * mm, "end": v(27.07, -22.62) * mm});
            skLineSegment(sketch, "E1511", {"start": v(27.07, -22.62) * mm, "end": v(27.07, -22.4) * mm});
            skLineSegment(sketch, "E1512", {"start": v(27.07, -22.4) * mm, "end": v(27.02, -22.15) * mm});
            skLineSegment(sketch, "E1513", {"start": v(27.02, -22.15) * mm, "end": v(26.97, -21.9) * mm});
            skLineSegment(sketch, "E1514", {"start": v(26.97, -21.9) * mm, "end": v(26.91, -21.66) * mm});
            skLineSegment(sketch, "E1515", {"start": v(26.91, -21.66) * mm, "end": v(26.86, -21.42) * mm});
            skLineSegment(sketch, "E1516", {"start": v(26.86, -21.42) * mm, "end": v(26.8, -21.18) * mm});
            skLineSegment(sketch, "E1517", {"start": v(26.8, -21.18) * mm, "end": v(26.74, -20.95) * mm});
            skLineSegment(sketch, "E1518", {"start": v(26.74, -20.95) * mm, "end": v(26.68, -20.72) * mm});
            skLineSegment(sketch, "E1519", {"start": v(26.68, -20.72) * mm, "end": v(26.61, -20.5) * mm});
            skLineSegment(sketch, "E1520", {"start": v(26.61, -20.5) * mm, "end": v(26.55, -20.27) * mm});
            skLineSegment(sketch, "E1521", {"start": v(26.55, -20.27) * mm, "end": v(26.48, -20.06) * mm});
            skLineSegment(sketch, "E1522", {"start": v(26.48, -20.06) * mm, "end": v(26.42, -19.85) * mm});
            skLineSegment(sketch, "E1523", {"start": v(26.42, -19.85) * mm, "end": v(26.35, -19.64) * mm});
            skLineSegment(sketch, "E1524", {"start": v(26.35, -19.64) * mm, "end": v(26.27, -19.44) * mm});
            skLineSegment(sketch, "E1525", {"start": v(26.27, -19.44) * mm, "end": v(26.2, -19.24) * mm});
            skLineSegment(sketch, "E1526", {"start": v(26.2, -19.24) * mm, "end": v(26.13, -19.05) * mm});
            skLineSegment(sketch, "E1527", {"start": v(26.13, -19.05) * mm, "end": v(26.06, -18.86) * mm});
            skLineSegment(sketch, "E1528", {"start": v(26.06, -18.86) * mm, "end": v(25.98, -18.67) * mm});
            skLineSegment(sketch, "E1529", {"start": v(25.98, -18.67) * mm, "end": v(25.9, -18.49) * mm});
            skLineSegment(sketch, "E1530", {"start": v(25.9, -18.49) * mm, "end": v(25.83, -18.31) * mm});
            skLineSegment(sketch, "E1531", {"start": v(25.83, -18.31) * mm, "end": v(25.76, -18.14) * mm});
            skLineSegment(sketch, "E1532", {"start": v(25.76, -18.14) * mm, "end": v(25.68, -17.97) * mm});
            skLineSegment(sketch, "E1533", {"start": v(25.68, -17.97) * mm, "end": v(25.6, -17.8) * mm});
            skLineSegment(sketch, "E1534", {"start": v(25.6, -17.8) * mm, "end": v(25.53, -17.65) * mm});
            skLineSegment(sketch, "E1535", {"start": v(25.53, -17.65) * mm, "end": v(25.45, -17.5) * mm});
            skLineSegment(sketch, "E1536", {"start": v(25.45, -17.5) * mm, "end": v(25.37, -17.34) * mm});
            skLineSegment(sketch, "E1537", {"start": v(25.37, -17.34) * mm, "end": v(25.3, -17.2) * mm});
            skLineSegment(sketch, "E1538", {"start": v(25.3, -17.2) * mm, "end": v(25.34, -17.04) * mm});
            skLineSegment(sketch, "E1539", {"start": v(25.34, -17.04) * mm, "end": v(25.46, -16.94) * mm});
            skLineSegment(sketch, "E1540", {"start": v(25.46, -16.94) * mm, "end": v(25.63, -16.96) * mm});
            skLineSegment(sketch, "E1541", {"start": v(25.63, -16.96) * mm, "end": v(25.8, -16.97) * mm});
            skLineSegment(sketch, "E1542", {"start": v(25.8, -16.97) * mm, "end": v(25.97, -16.98) * mm});
            skLineSegment(sketch, "E1543", {"start": v(25.97, -16.98) * mm, "end": v(26.15, -17) * mm});
            skLineSegment(sketch, "E1544", {"start": v(26.15, -17) * mm, "end": v(26.33, -17) * mm});
            skLineSegment(sketch, "E1545", {"start": v(26.33, -17) * mm, "end": v(26.51, -17.01) * mm});
            skLineSegment(sketch, "E1546", {"start": v(26.51, -17.01) * mm, "end": v(26.7, -17.02) * mm});
            skLineSegment(sketch, "E1547", {"start": v(26.7, -17.02) * mm, "end": v(26.9, -17.02) * mm});
            skLineSegment(sketch, "E1548", {"start": v(26.9, -17.02) * mm, "end": v(27.1, -17.02) * mm});
            skLineSegment(sketch, "E1549", {"start": v(27.1, -17.02) * mm, "end": v(27.3, -17.02) * mm});
            skLineSegment(sketch, "E1550", {"start": v(27.3, -17.02) * mm, "end": v(27.5, -17.02) * mm});
            skLineSegment(sketch, "E1551", {"start": v(27.5, -17.02) * mm, "end": v(27.7, -17.01) * mm});
            skLineSegment(sketch, "E1552", {"start": v(27.7, -17.01) * mm, "end": v(27.91, -17) * mm});
            skLineSegment(sketch, "E1553", {"start": v(27.91, -17) * mm, "end": v(28.13, -17) * mm});
            skLineSegment(sketch, "E1554", {"start": v(28.13, -17) * mm, "end": v(28.34, -16.98) * mm});
            skLineSegment(sketch, "E1555", {"start": v(28.34, -16.98) * mm, "end": v(28.57, -16.96) * mm});
            skLineSegment(sketch, "E1556", {"start": v(28.57, -16.96) * mm, "end": v(28.8, -16.94) * mm});
            skLineSegment(sketch, "E1557", {"start": v(28.8, -16.94) * mm, "end": v(29.02, -16.92) * mm});
            skLineSegment(sketch, "E1558", {"start": v(29.02, -16.92) * mm, "end": v(29.25, -16.9) * mm});
            skLineSegment(sketch, "E1559", {"start": v(29.25, -16.9) * mm, "end": v(29.49, -16.86) * mm});
            skLineSegment(sketch, "E1560", {"start": v(29.49, -16.86) * mm, "end": v(29.72, -16.83) * mm});
            skLineSegment(sketch, "E1561", {"start": v(29.72, -16.83) * mm, "end": v(29.97, -16.8) * mm});
            skLineSegment(sketch, "E1562", {"start": v(29.97, -16.8) * mm, "end": v(30.2, -16.76) * mm});
            skLineSegment(sketch, "E1563", {"start": v(30.2, -16.76) * mm, "end": v(30.46, -16.72) * mm});
            skLineSegment(sketch, "E1564", {"start": v(30.46, -16.72) * mm, "end": v(30.7, -16.67) * mm});
            skLineSegment(sketch, "E1565", {"start": v(30.7, -16.67) * mm, "end": v(30.96, -16.62) * mm});
            skLineSegment(sketch, "E1566", {"start": v(30.96, -16.62) * mm, "end": v(31.16, -16.54) * mm});
            skLineSegment(sketch, "E1567", {"start": v(31.16, -16.54) * mm, "end": v(31.18, -16.5) * mm});
            skLineSegment(sketch, "E1568", {"start": v(31.18, -16.5) * mm, "end": v(31.14, -16.29) * mm});
            skLineSegment(sketch, "E1569", {"start": v(31.14, -16.29) * mm, "end": v(31.04, -16.05) * mm});
            skLineSegment(sketch, "E1570", {"start": v(31.04, -16.05) * mm, "end": v(30.93, -15.82) * mm});
            skLineSegment(sketch, "E1571", {"start": v(30.93, -15.82) * mm, "end": v(30.83, -15.59) * mm});
            skLineSegment(sketch, "E1572", {"start": v(30.83, -15.59) * mm, "end": v(30.72, -15.36) * mm});
            skLineSegment(sketch, "E1573", {"start": v(30.72, -15.36) * mm, "end": v(30.62, -15.14) * mm});
            skLineSegment(sketch, "E1574", {"start": v(30.62, -15.14) * mm, "end": v(30.51, -14.93) * mm});
            skLineSegment(sketch, "E1575", {"start": v(30.51, -14.93) * mm, "end": v(30.4, -14.72) * mm});
            skLineSegment(sketch, "E1576", {"start": v(30.4, -14.72) * mm, "end": v(30.3, -14.51) * mm});
            skLineSegment(sketch, "E1577", {"start": v(30.3, -14.51) * mm, "end": v(30.18, -14.31) * mm});
            skLineSegment(sketch, "E1578", {"start": v(30.18, -14.31) * mm, "end": v(30.07, -14.11) * mm});
            skLineSegment(sketch, "E1579", {"start": v(30.07, -14.11) * mm, "end": v(29.96, -13.92) * mm});
            skLineSegment(sketch, "E1580", {"start": v(29.96, -13.92) * mm, "end": v(29.85, -13.73) * mm});
            skLineSegment(sketch, "E1581", {"start": v(29.85, -13.73) * mm, "end": v(29.74, -13.55) * mm});
            skLineSegment(sketch, "E1582", {"start": v(29.74, -13.55) * mm, "end": v(29.63, -13.37) * mm});
            skLineSegment(sketch, "E1583", {"start": v(29.63, -13.37) * mm, "end": v(29.52, -13.2) * mm});
            skLineSegment(sketch, "E1584", {"start": v(29.52, -13.2) * mm, "end": v(29.4, -13.03) * mm});
            skLineSegment(sketch, "E1585", {"start": v(29.4, -13.03) * mm, "end": v(29.3, -12.86) * mm});
            skLineSegment(sketch, "E1586", {"start": v(29.3, -12.86) * mm, "end": v(29.19, -12.7) * mm});
            skLineSegment(sketch, "E1587", {"start": v(29.19, -12.7) * mm, "end": v(29.08, -12.54) * mm});
            skLineSegment(sketch, "E1588", {"start": v(29.08, -12.54) * mm, "end": v(28.96, -12.39) * mm});
            skLineSegment(sketch, "E1589", {"start": v(28.96, -12.39) * mm, "end": v(28.85, -12.24) * mm});
            skLineSegment(sketch, "E1590", {"start": v(28.85, -12.24) * mm, "end": v(28.74, -12.1) * mm});
            skLineSegment(sketch, "E1591", {"start": v(28.74, -12.1) * mm, "end": v(28.64, -11.95) * mm});
            skLineSegment(sketch, "E1592", {"start": v(28.64, -11.95) * mm, "end": v(28.53, -11.82) * mm});
            skLineSegment(sketch, "E1593", {"start": v(28.53, -11.82) * mm, "end": v(28.42, -11.68) * mm});
            skLineSegment(sketch, "E1594", {"start": v(28.42, -11.68) * mm, "end": v(28.31, -11.56) * mm});
            skLineSegment(sketch, "E1595", {"start": v(28.31, -11.56) * mm, "end": v(28.33, -11.4) * mm});
            skLineSegment(sketch, "E1596", {"start": v(28.33, -11.4) * mm, "end": v(28.43, -11.28) * mm});
            skLineSegment(sketch, "E1597", {"start": v(28.43, -11.28) * mm, "end": v(28.6, -11.26) * mm});
            skLineSegment(sketch, "E1598", {"start": v(28.6, -11.26) * mm, "end": v(28.76, -11.24) * mm});
            skLineSegment(sketch, "E1599", {"start": v(28.76, -11.24) * mm, "end": v(28.93, -11.21) * mm});
            skLineSegment(sketch, "E1600", {"start": v(28.93, -11.21) * mm, "end": v(29.1, -11.19) * mm});
            skLineSegment(sketch, "E1601", {"start": v(29.1, -11.19) * mm, "end": v(29.29, -11.16) * mm});
            skLineSegment(sketch, "E1602", {"start": v(29.29, -11.16) * mm, "end": v(29.47, -11.13) * mm});
            skLineSegment(sketch, "E1603", {"start": v(29.47, -11.13) * mm, "end": v(29.66, -11.1) * mm});
            skLineSegment(sketch, "E1604", {"start": v(29.66, -11.1) * mm, "end": v(29.85, -11.06) * mm});
            skLineSegment(sketch, "E1605", {"start": v(29.85, -11.06) * mm, "end": v(30.04, -11.02) * mm});
            skLineSegment(sketch, "E1606", {"start": v(30.04, -11.02) * mm, "end": v(30.23, -10.97) * mm});
            skLineSegment(sketch, "E1607", {"start": v(30.23, -10.97) * mm, "end": v(30.43, -10.93) * mm});
            skLineSegment(sketch, "E1608", {"start": v(30.43, -10.93) * mm, "end": v(30.63, -10.88) * mm});
            skLineSegment(sketch, "E1609", {"start": v(30.63, -10.88) * mm, "end": v(30.84, -10.83) * mm});
            skLineSegment(sketch, "E1610", {"start": v(30.84, -10.83) * mm, "end": v(31.05, -10.77) * mm});
            skLineSegment(sketch, "E1611", {"start": v(31.05, -10.77) * mm, "end": v(31.26, -10.71) * mm});
            skLineSegment(sketch, "E1612", {"start": v(31.26, -10.71) * mm, "end": v(31.47, -10.65) * mm});
            skLineSegment(sketch, "E1613", {"start": v(31.47, -10.65) * mm, "end": v(31.68, -10.58) * mm});
            skLineSegment(sketch, "E1614", {"start": v(31.68, -10.58) * mm, "end": v(31.9, -10.52) * mm});
            skLineSegment(sketch, "E1615", {"start": v(31.9, -10.52) * mm, "end": v(32.12, -10.44) * mm});
            skLineSegment(sketch, "E1616", {"start": v(32.12, -10.44) * mm, "end": v(32.35, -10.37) * mm});
            skLineSegment(sketch, "E1617", {"start": v(32.35, -10.37) * mm, "end": v(32.57, -10.28) * mm});
            skLineSegment(sketch, "E1618", {"start": v(32.57, -10.28) * mm, "end": v(32.8, -10.2) * mm});
            skLineSegment(sketch, "E1619", {"start": v(32.8, -10.2) * mm, "end": v(33.03, -10.11) * mm});
            skLineSegment(sketch, "E1620", {"start": v(33.03, -10.11) * mm, "end": v(33.27, -10.02) * mm});
            skLineSegment(sketch, "E1621", {"start": v(33.27, -10.02) * mm, "end": v(33.5, -9.92) * mm});
            skLineSegment(sketch, "E1622", {"start": v(33.5, -9.92) * mm, "end": v(33.74, -9.82) * mm});
            skLineSegment(sketch, "E1623", {"start": v(33.74, -9.82) * mm, "end": v(33.92, -9.7) * mm});
            skLineSegment(sketch, "E1624", {"start": v(33.92, -9.7) * mm, "end": v(33.93, -9.66) * mm});
            skLineSegment(sketch, "E1625", {"start": v(33.93, -9.66) * mm, "end": v(33.84, -9.46) * mm});
            skLineSegment(sketch, "E1626", {"start": v(33.84, -9.46) * mm, "end": v(33.7, -9.25) * mm});
            skLineSegment(sketch, "E1627", {"start": v(33.7, -9.25) * mm, "end": v(33.55, -9.04) * mm});
            skLineSegment(sketch, "E1628", {"start": v(33.55, -9.04) * mm, "end": v(33.4, -8.84) * mm});
            skLineSegment(sketch, "E1629", {"start": v(33.4, -8.84) * mm, "end": v(33.25, -8.64) * mm});
            skLineSegment(sketch, "E1630", {"start": v(33.25, -8.64) * mm, "end": v(33.1, -8.45) * mm});
            skLineSegment(sketch, "E1631", {"start": v(33.1, -8.45) * mm, "end": v(32.95, -8.26) * mm});
            skLineSegment(sketch, "E1632", {"start": v(32.95, -8.26) * mm, "end": v(32.8, -8.08) * mm});
            skLineSegment(sketch, "E1633", {"start": v(32.8, -8.08) * mm, "end": v(32.65, -7.9) * mm});
            skLineSegment(sketch, "E1634", {"start": v(32.65, -7.9) * mm, "end": v(32.5, -7.72) * mm});
            skLineSegment(sketch, "E1635", {"start": v(32.5, -7.72) * mm, "end": v(32.35, -7.55) * mm});
            skLineSegment(sketch, "E1636", {"start": v(32.35, -7.55) * mm, "end": v(32.2, -7.39) * mm});
            skLineSegment(sketch, "E1637", {"start": v(32.2, -7.39) * mm, "end": v(32.06, -7.23) * mm});
            skLineSegment(sketch, "E1638", {"start": v(32.06, -7.23) * mm, "end": v(31.9, -7.07) * mm});
            skLineSegment(sketch, "E1639", {"start": v(31.9, -7.07) * mm, "end": v(31.76, -6.92) * mm});
            skLineSegment(sketch, "E1640", {"start": v(31.76, -6.92) * mm, "end": v(31.62, -6.77) * mm});
            skLineSegment(sketch, "E1641", {"start": v(31.62, -6.77) * mm, "end": v(31.47, -6.63) * mm});
            skLineSegment(sketch, "E1642", {"start": v(31.47, -6.63) * mm, "end": v(31.33, -6.49) * mm});
            skLineSegment(sketch, "E1643", {"start": v(31.33, -6.49) * mm, "end": v(31.19, -6.35) * mm});
            skLineSegment(sketch, "E1644", {"start": v(31.19, -6.35) * mm, "end": v(31.05, -6.22) * mm});
            skLineSegment(sketch, "E1645", {"start": v(31.05, -6.22) * mm, "end": v(30.9, -6.1) * mm});
            skLineSegment(sketch, "E1646", {"start": v(30.9, -6.1) * mm, "end": v(30.77, -5.97) * mm});
            skLineSegment(sketch, "E1647", {"start": v(30.77, -5.97) * mm, "end": v(30.63, -5.85) * mm});
            skLineSegment(sketch, "E1648", {"start": v(30.63, -5.85) * mm, "end": v(30.5, -5.74) * mm});
            skLineSegment(sketch, "E1649", {"start": v(30.5, -5.74) * mm, "end": v(30.36, -5.63) * mm});
            skLineSegment(sketch, "E1650", {"start": v(30.36, -5.63) * mm, "end": v(30.23, -5.52) * mm});
            skLineSegment(sketch, "E1651", {"start": v(30.23, -5.52) * mm, "end": v(30.1, -5.42) * mm});
            skLineSegment(sketch, "E1652", {"start": v(30.1, -5.42) * mm, "end": v(30.08, -5.26) * mm});
            skLineSegment(sketch, "E1653", {"start": v(30.08, -5.26) * mm, "end": v(30.15, -5.12) * mm});
            skLineSegment(sketch, "E1654", {"start": v(30.15, -5.12) * mm, "end": v(30.3, -5.07) * mm});
            skLineSegment(sketch, "E1655", {"start": v(30.3, -5.07) * mm, "end": v(30.47, -5.01) * mm});
            skLineSegment(sketch, "E1656", {"start": v(30.47, -5.01) * mm, "end": v(30.63, -4.95) * mm});
            skLineSegment(sketch, "E1657", {"start": v(30.63, -4.95) * mm, "end": v(30.8, -4.9) * mm});
            skLineSegment(sketch, "E1658", {"start": v(30.8, -4.9) * mm, "end": v(30.97, -4.83) * mm});
            skLineSegment(sketch, "E1659", {"start": v(30.97, -4.83) * mm, "end": v(31.14, -4.76) * mm});
            skLineSegment(sketch, "E1660", {"start": v(31.14, -4.76) * mm, "end": v(31.32, -4.69) * mm});
            skLineSegment(sketch, "E1661", {"start": v(31.32, -4.69) * mm, "end": v(31.5, -4.6) * mm});
            skLineSegment(sketch, "E1662", {"start": v(31.5, -4.6) * mm, "end": v(31.67, -4.53) * mm});
            skLineSegment(sketch, "E1663", {"start": v(31.67, -4.53) * mm, "end": v(31.85, -4.45) * mm});
            skLineSegment(sketch, "E1664", {"start": v(31.85, -4.45) * mm, "end": v(32.04, -4.36) * mm});
            skLineSegment(sketch, "E1665", {"start": v(32.04, -4.36) * mm, "end": v(32.23, -4.27) * mm});
            skLineSegment(sketch, "E1666", {"start": v(32.23, -4.27) * mm, "end": v(32.42, -4.18) * mm});
            skLineSegment(sketch, "E1667", {"start": v(32.42, -4.18) * mm, "end": v(32.6, -4.08) * mm});
            skLineSegment(sketch, "E1668", {"start": v(32.6, -4.08) * mm, "end": v(32.8, -3.98) * mm});
            skLineSegment(sketch, "E1669", {"start": v(32.8, -3.98) * mm, "end": v(33, -3.88) * mm});
            skLineSegment(sketch, "E1670", {"start": v(33, -3.88) * mm, "end": v(33.2, -3.77) * mm});
            skLineSegment(sketch, "E1671", {"start": v(33.2, -3.77) * mm, "end": v(33.4, -3.65) * mm});
            skLineSegment(sketch, "E1672", {"start": v(33.4, -3.65) * mm, "end": v(33.6, -3.53) * mm});
            skLineSegment(sketch, "E1673", {"start": v(33.6, -3.53) * mm, "end": v(33.8, -3.41) * mm});
            skLineSegment(sketch, "E1674", {"start": v(33.8, -3.41) * mm, "end": v(34, -3.29) * mm});
            skLineSegment(sketch, "E1675", {"start": v(34, -3.29) * mm, "end": v(34.2, -3.16) * mm});
            skLineSegment(sketch, "E1676", {"start": v(34.2, -3.16) * mm, "end": v(34.41, -3.02) * mm});
            skLineSegment(sketch, "E1677", {"start": v(34.41, -3.02) * mm, "end": v(34.62, -2.88) * mm});
            skLineSegment(sketch, "E1678", {"start": v(34.62, -2.88) * mm, "end": v(34.83, -2.74) * mm});
            skLineSegment(sketch, "E1679", {"start": v(34.83, -2.74) * mm, "end": v(35.04, -2.6) * mm});
            skLineSegment(sketch, "E1680", {"start": v(35.04, -2.6) * mm, "end": v(35.2, -2.43) * mm});
            skLineSegment(sketch, "E1681", {"start": v(35.2, -2.43) * mm, "end": v(35.2, -2.4) * mm});
            skLineSegment(sketch, "E1682", {"start": v(35.2, -2.4) * mm, "end": v(35.07, -2.21) * mm});
            skLineSegment(sketch, "E1683", {"start": v(35.07, -2.21) * mm, "end": v(34.88, -2.04) * mm});
            skLineSegment(sketch, "E1684", {"start": v(34.88, -2.04) * mm, "end": v(34.7, -1.87) * mm});
            skLineSegment(sketch, "E1685", {"start": v(34.7, -1.87) * mm, "end": v(34.5, -1.7) * mm});
            skLineSegment(sketch, "E1686", {"start": v(34.5, -1.7) * mm, "end": v(34.32, -1.54) * mm});
            skLineSegment(sketch, "E1687", {"start": v(34.32, -1.54) * mm, "end": v(34.13, -1.38) * mm});
            skLineSegment(sketch, "E1688", {"start": v(34.13, -1.38) * mm, "end": v(33.95, -1.23) * mm});
            skLineSegment(sketch, "E1689", {"start": v(33.95, -1.23) * mm, "end": v(33.76, -1.08) * mm});
            skLineSegment(sketch, "E1690", {"start": v(33.76, -1.08) * mm, "end": v(33.58, -0.94) * mm});
            skLineSegment(sketch, "E1691", {"start": v(33.58, -0.94) * mm, "end": v(33.4, -0.8) * mm});
            skLineSegment(sketch, "E1692", {"start": v(33.4, -0.8) * mm, "end": v(33.22, -0.66) * mm});
            skLineSegment(sketch, "E1693", {"start": v(33.22, -0.66) * mm, "end": v(33.04, -0.53) * mm});
            skLineSegment(sketch, "E1694", {"start": v(33.04, -0.53) * mm, "end": v(32.86, -0.4) * mm});
            skLineSegment(sketch, "E1695", {"start": v(32.86, -0.4) * mm, "end": v(32.68, -0.28) * mm});
            skLineSegment(sketch, "E1696", {"start": v(32.68, -0.28) * mm, "end": v(32.5, -0.16) * mm});
            skLineSegment(sketch, "E1697", {"start": v(32.5, -0.16) * mm, "end": v(32.34, -0.05) * mm});
            skLineSegment(sketch, "E1698", {"start": v(32.34, -0.05) * mm, "end": v(32.16, 0.06) * mm});
            skLineSegment(sketch, "E1699", {"start": v(32.16, 0.06) * mm, "end": v(32, 0.17) * mm});
            skLineSegment(sketch, "E1700", {"start": v(32, 0.17) * mm, "end": v(31.83, 0.27) * mm});
            skLineSegment(sketch, "E1701", {"start": v(31.83, 0.27) * mm, "end": v(31.66, 0.37) * mm});
            skLineSegment(sketch, "E1702", {"start": v(31.66, 0.37) * mm, "end": v(31.5, 0.46) * mm});
            skLineSegment(sketch, "E1703", {"start": v(31.5, 0.46) * mm, "end": v(31.34, 0.56) * mm});
            skLineSegment(sketch, "E1704", {"start": v(31.34, 0.56) * mm, "end": v(31.18, 0.64) * mm});
            skLineSegment(sketch, "E1705", {"start": v(31.18, 0.64) * mm, "end": v(31.02, 0.73) * mm});
            skLineSegment(sketch, "E1706", {"start": v(31.02, 0.73) * mm, "end": v(30.87, 0.8) * mm});
            skLineSegment(sketch, "E1707", {"start": v(30.87, 0.8) * mm, "end": v(30.71, 0.88) * mm});
            skLineSegment(sketch, "E1708", {"start": v(30.71, 0.88) * mm, "end": v(30.57, 0.96) * mm});
            skLineSegment(sketch, "E1709", {"start": v(30.57, 0.96) * mm, "end": v(30.52, 1.1) * mm});
            skLineSegment(sketch, "E1710", {"start": v(2.65, 0) * mm, "end": v(-2.65, 0) * mm});
            skLineSegment(sketch, "E1711", {"start": v(0, -2.65) * mm, "end": v(0, 2.65) * mm});
            skLineSegment(sketch, "E1712", {"start": v(33.61, 4.65) * mm, "end": v(33.36, 4.04) * mm});
            skLineSegment(sketch, "E1713", {"start": v(33.36, 4.04) * mm, "end": v(32.74, 3.78) * mm});
            skLineSegment(sketch, "E1714", {"start": v(32.74, 3.78) * mm, "end": v(32.13, 4.04) * mm});
            skLineSegment(sketch, "E1715", {"start": v(32.13, 4.04) * mm, "end": v(31.88, 4.65) * mm});
            skLineSegment(sketch, "E1716", {"start": v(31.88, 4.65) * mm, "end": v(32.13, 5.26) * mm});
            skLineSegment(sketch, "E1717", {"start": v(32.13, 5.26) * mm, "end": v(32.74, 5.51) * mm});
            skLineSegment(sketch, "E1718", {"start": v(32.74, 5.51) * mm, "end": v(33.36, 5.26) * mm});
            skLineSegment(sketch, "E1719", {"start": v(33.36, 5.26) * mm, "end": v(33.61, 4.65) * mm});
            skLineSegment(sketch, "E1720", {"start": v(-17.25, 15.6) * mm, "end": v(-17.74, 15.06) * mm});
            skLineSegment(sketch, "E1721", {"start": v(-17.74, 15.06) * mm, "end": v(-18.2, 14.5) * mm});
            skLineSegment(sketch, "E1722", {"start": v(-18.2, 14.5) * mm, "end": v(-18.64, 13.93) * mm});
            skLineSegment(sketch, "E1723", {"start": v(-18.64, 13.93) * mm, "end": v(-19.07, 13.34) * mm});
            skLineSegment(sketch, "E1724", {"start": v(-17.06, 13.6) * mm, "end": v(-19.33, 15.4) * mm});
            skLineSegment(sketch, "E1725", {"start": v(-18.33, 16.58) * mm, "end": v(-18.29, 15.53) * mm});
            skLineSegment(sketch, "E1726", {"start": v(-18.29, 15.53) * mm, "end": v(-18.2, 14.5) * mm});
            skLineSegment(sketch, "E1727", {"start": v(-18.2, 14.5) * mm, "end": v(-18.06, 13.49) * mm});
            skLineSegment(sketch, "E1728", {"start": v(-18.06, 13.49) * mm, "end": v(-17.88, 12.5) * mm});
            skLineSegment(sketch, "E1729", {"start": v(-16.18, 14.63) * mm, "end": v(-17.18, 14.6) * mm});
            skLineSegment(sketch, "E1730", {"start": v(-17.18, 14.6) * mm, "end": v(-18.2, 14.5) * mm});
            skLineSegment(sketch, "E1731", {"start": v(-18.2, 14.5) * mm, "end": v(-19.22, 14.36) * mm});
            skLineSegment(sketch, "E1732", {"start": v(-19.22, 14.36) * mm, "end": v(-20.26, 14.17) * mm});
            skLineSegment(sketch, "E1733", {"start": v(-13.7, 16.97) * mm, "end": v(-13.75, 15.98) * mm});
            skLineSegment(sketch, "E1734", {"start": v(-13.75, 15.98) * mm, "end": v(-14.24, 15.55) * mm});
            skLineSegment(sketch, "E1735", {"start": v(-14.24, 15.55) * mm, "end": v(-15.23, 15.62) * mm});
            skLineSegment(sketch, "E1736", {"start": v(-15.23, 15.62) * mm, "end": v(-17.26, 17.7) * mm});
            skLineSegment(sketch, "E1737", {"start": v(-17.26, 17.7) * mm, "end": v(-17.19, 18.76) * mm});
            skLineSegment(sketch, "E1738", {"start": v(-17.19, 18.76) * mm, "end": v(-16.6, 19.3) * mm});
            skLineSegment(sketch, "E1739", {"start": v(-16.6, 19.3) * mm, "end": v(-15.53, 19.23) * mm});
            skLineSegment(sketch, "E1740", {"start": v(-15.53, 19.23) * mm, "end": v(-13.7, 16.97) * mm});
            skLineSegment(sketch, "E1741", {"start": v(-8.38, 24.03) * mm, "end": v(-6.94, 19.9) * mm});
            skLineSegment(sketch, "E1742", {"start": v(-6.94, 19.9) * mm, "end": v(-7.95, 20.7) * mm});
            skLineSegment(sketch, "E1743", {"start": v(-7.95, 20.7) * mm, "end": v(-9.02, 21.45) * mm});
            skLineSegment(sketch, "E1744", {"start": v(-9.02, 21.45) * mm, "end": v(-10.14, 22.15) * mm});
            skLineSegment(sketch, "E1745", {"start": v(-10.14, 22.15) * mm, "end": v(-11.3, 22.8) * mm});
            skLineSegment(sketch, "E1746", {"start": v(-11.3, 22.8) * mm, "end": v(-9.37, 18.89) * mm});
            skLineSegment(sketch, "E1747", {"start": v(-3.54, 23.73) * mm, "end": v(-4.28, 23.6) * mm});
            skLineSegment(sketch, "E1748", {"start": v(-4.28, 23.6) * mm, "end": v(-5.01, 23.46) * mm});
            skLineSegment(sketch, "E1749", {"start": v(-5.01, 23.46) * mm, "end": v(-5.74, 23.3) * mm});
            skLineSegment(sketch, "E1750", {"start": v(-5.74, 23.3) * mm, "end": v(-6.47, 23.1) * mm});
            skLineSegment(sketch, "E1751", {"start": v(-3.32, 22.3) * mm, "end": v(-4.02, 22.18) * mm});
            skLineSegment(sketch, "E1752", {"start": v(-4.02, 22.18) * mm, "end": v(-4.71, 22.04) * mm});
            skLineSegment(sketch, "E1753", {"start": v(-4.71, 22.04) * mm, "end": v(-5.4, 21.88) * mm});
            skLineSegment(sketch, "E1754", {"start": v(-5.4, 21.88) * mm, "end": v(-6.07, 21.7) * mm});
            skLineSegment(sketch, "E1755", {"start": v(-2.1, 24.63) * mm, "end": v(-1.38, 25.41) * mm});
            skLineSegment(sketch, "E1756", {"start": v(-1.38, 25.41) * mm, "end": v(-0.58, 25.44) * mm});
            skLineSegment(sketch, "E1757", {"start": v(-0.58, 25.44) * mm, "end": v(0.21, 25.45) * mm});
            skLineSegment(sketch, "E1758", {"start": v(0.21, 25.45) * mm, "end": v(0.98, 24.7) * mm});
            skLineSegment(sketch, "E1759", {"start": v(0.98, 24.7) * mm, "end": v(0.95, 23.97) * mm});
            skLineSegment(sketch, "E1760", {"start": v(0.95, 23.97) * mm, "end": v(0.2, 23.27) * mm});
            skLineSegment(sketch, "E1761", {"start": v(0.2, 23.27) * mm, "end": v(0.9, 22.52) * mm});
            skLineSegment(sketch, "E1762", {"start": v(0.9, 22.52) * mm, "end": v(0.86, 21.8) * mm});
            skLineSegment(sketch, "E1763", {"start": v(0.86, 21.8) * mm, "end": v(0.17, 21.08) * mm});
            skLineSegment(sketch, "E1764", {"start": v(0.17, 21.08) * mm, "end": v(-0.48, 21.08) * mm});
            skLineSegment(sketch, "E1765", {"start": v(-0.48, 21.08) * mm, "end": v(-1.14, 21.06) * mm});
            skLineSegment(sketch, "E1766", {"start": v(-1.14, 21.06) * mm, "end": v(-1.86, 21.73) * mm});
            skLineSegment(sketch, "E1767", {"start": v(-0.53, 23.26) * mm, "end": v(0.2, 23.27) * mm});
            skLineSegment(sketch, "E1768", {"start": v(4.24, 21.4) * mm, "end": v(3.45, 20.8) * mm});
            skLineSegment(sketch, "E1769", {"start": v(3.45, 20.8) * mm, "end": v(2.8, 20.9) * mm});
            skLineSegment(sketch, "E1770", {"start": v(2.8, 20.9) * mm, "end": v(2.22, 21.7) * mm});
            skLineSegment(sketch, "E1771", {"start": v(2.22, 21.7) * mm, "end": v(2.52, 24.6) * mm});
            skLineSegment(sketch, "E1772", {"start": v(2.52, 24.6) * mm, "end": v(3.38, 25.22) * mm});
            skLineSegment(sketch, "E1773", {"start": v(3.38, 25.22) * mm, "end": v(4.17, 25.1) * mm});
            skLineSegment(sketch, "E1774", {"start": v(4.17, 25.1) * mm, "end": v(4.81, 24.25) * mm});
            skLineSegment(sketch, "E1775", {"start": v(4.81, 24.25) * mm, "end": v(4.24, 21.4) * mm});
            skLineSegment(sketch, "E1776", {"start": v(9.37, 21.3) * mm, "end": v(10.03, 21) * mm});
            skLineSegment(sketch, "E1777", {"start": v(10.03, 21) * mm, "end": v(10.68, 20.67) * mm});
            skLineSegment(sketch, "E1778", {"start": v(10.68, 20.67) * mm, "end": v(11.32, 20.32) * mm});
            skLineSegment(sketch, "E1779", {"start": v(11.32, 20.32) * mm, "end": v(12.33, 20.59) * mm});
            skLineSegment(sketch, "E1780", {"start": v(12.33, 20.59) * mm, "end": v(12.7, 21.2) * mm});
            skLineSegment(sketch, "E1781", {"start": v(12.7, 21.2) * mm, "end": v(12.39, 22.23) * mm});
            skLineSegment(sketch, "E1782", {"start": v(12.39, 22.23) * mm, "end": v(11.68, 22.6) * mm});
            skLineSegment(sketch, "E1783", {"start": v(11.68, 22.6) * mm, "end": v(10.97, 22.96) * mm});
            skLineSegment(sketch, "E1784", {"start": v(10.97, 22.96) * mm, "end": v(10.25, 23.3) * mm});
            skLineSegment(sketch, "E1785", {"start": v(10.25, 23.3) * mm, "end": v(8.5, 19.3) * mm});
            skLineSegment(sketch, "E1786", {"start": v(11.94, 17.38) * mm, "end": v(13.59, 19.77) * mm});
            skLineSegment(sketch, "E1787", {"start": v(14, 20.38) * mm, "end": v(14.41, 20.97) * mm});
            skLineSegment(sketch, "E1788", {"start": v(15.49, 15.36) * mm, "end": v(14.5, 15.3) * mm});
            skLineSegment(sketch, "E1789", {"start": v(14.5, 15.3) * mm, "end": v(14.5, 16.3) * mm});
            skLineSegment(sketch, "E1790", {"start": v(14.5, 16.3) * mm, "end": v(16.92, 19.01) * mm});
            skLineSegment(sketch, "E1791", {"start": v(17.04, 16.9) * mm, "end": v(16.5, 17.42) * mm});
            skLineSegment(sketch, "E1792", {"start": v(16.5, 17.42) * mm, "end": v(15.95, 17.93) * mm});
            skLineSegment(sketch, "E1793", {"start": v(15.95, 17.93) * mm, "end": v(15.38, 18.41) * mm});
            skLineSegment(sketch, "E1794", {"start": v(15.38, 18.41) * mm, "end": v(14.8, 18.89) * mm});
            skLineSegment(sketch, "E1795", {"start": v(17.48, 11.8) * mm, "end": v(17.1, 12.34) * mm});
            skLineSegment(sketch, "E1796", {"start": v(17.1, 12.34) * mm, "end": v(16.7, 12.86) * mm});
            skLineSegment(sketch, "E1797", {"start": v(16.7, 12.86) * mm, "end": v(16.3, 13.38) * mm});
            skLineSegment(sketch, "E1798", {"start": v(16.3, 13.38) * mm, "end": v(16.42, 14.36) * mm});
            skLineSegment(sketch, "E1799", {"start": v(16.42, 14.36) * mm, "end": v(17.51, 15.32) * mm});
            skLineSegment(sketch, "E1800", {"start": v(17.51, 15.32) * mm, "end": v(18.54, 15.23) * mm});
            skLineSegment(sketch, "E1801", {"start": v(18.54, 15.23) * mm, "end": v(19, 14.64) * mm});
            skLineSegment(sketch, "E1802", {"start": v(19, 14.64) * mm, "end": v(19.46, 14.04) * mm});
            skLineSegment(sketch, "E1803", {"start": v(19.46, 14.04) * mm, "end": v(19.89, 13.42) * mm});
            skLineSegment(sketch, "E1804", {"start": v(19.43, 11.42) * mm, "end": v(20.42, 11.16) * mm});
            skLineSegment(sketch, "E1805", {"start": v(20.42, 11.16) * mm, "end": v(21.4, 10.84) * mm});
            skLineSegment(sketch, "E1806", {"start": v(21.4, 10.84) * mm, "end": v(21.73, 10.17) * mm});
            skLineSegment(sketch, "E1807", {"start": v(21.73, 10.17) * mm, "end": v(21.37, 9.2) * mm});
            skLineSegment(sketch, "E1808", {"start": v(21.37, 9.2) * mm, "end": v(19.37, 8.33) * mm});
            skLineSegment(sketch, "E1809", {"start": v(18.18, 10.68) * mm, "end": v(21.94, 12.9) * mm});
            skLineSegment(sketch, "E1810", {"start": v(20.72, 3.93) * mm, "end": v(20.83, 3.28) * mm});
            skLineSegment(sketch, "E1811", {"start": v(20.83, 3.28) * mm, "end": v(20.92, 2.63) * mm});
            skLineSegment(sketch, "E1812", {"start": v(20.92, 2.63) * mm, "end": v(21, 1.97) * mm});
            skLineSegment(sketch, "E1813", {"start": v(21, 1.97) * mm, "end": v(21.77, 1.36) * mm});
            skLineSegment(sketch, "E1814", {"start": v(21.77, 1.36) * mm, "end": v(24.67, 1.54) * mm});
            skLineSegment(sketch, "E1815", {"start": v(24.67, 1.54) * mm, "end": v(25.34, 2.38) * mm});
            skLineSegment(sketch, "E1816", {"start": v(25.34, 2.38) * mm, "end": v(25.25, 3.17) * mm});
            skLineSegment(sketch, "E1817", {"start": v(25.25, 3.17) * mm, "end": v(25.14, 3.96) * mm});
            skLineSegment(sketch, "E1818", {"start": v(25.14, 3.96) * mm, "end": v(25, 4.74) * mm});
            skLineSegment(sketch, "E1819", {"start": v(25.14, 3.96) * mm, "end": v(20.83, 3.28) * mm});
            skLineSegment(sketch, "E1820", {"start": v(23.8, -3) * mm, "end": v(23.89, -2.25) * mm});
            skLineSegment(sketch, "E1821", {"start": v(23.89, -2.25) * mm, "end": v(23.95, -1.5) * mm});
            skLineSegment(sketch, "E1822", {"start": v(23.95, -1.5) * mm, "end": v(23.98, -0.75) * mm});
            skLineSegment(sketch, "E1823", {"start": v(23.98, -0.75) * mm, "end": v(24, 0) * mm});
            skLineSegment(sketch, "E1824", {"start": v(22.36, -2.8) * mm, "end": v(22.44, -2.1) * mm});
            skLineSegment(sketch, "E1825", {"start": v(22.44, -2.1) * mm, "end": v(22.5, -1.4) * mm});
            skLineSegment(sketch, "E1826", {"start": v(22.5, -1.4) * mm, "end": v(22.53, -0.7) * mm});
            skLineSegment(sketch, "E1827", {"start": v(22.53, -0.7) * mm, "end": v(22.54, 0) * mm});
            skLineSegment(sketch, "E1828", {"start": v(20.06, -6.48) * mm, "end": v(20.26, -5.85) * mm});
            skLineSegment(sketch, "E1829", {"start": v(20.26, -5.85) * mm, "end": v(20.43, -5.22) * mm});
            skLineSegment(sketch, "E1830", {"start": v(20.43, -5.22) * mm, "end": v(20.58, -4.58) * mm});
            skLineSegment(sketch, "E1831", {"start": v(20.58, -4.58) * mm, "end": v(20.72, -3.93) * mm});
            skLineSegment(sketch, "E1832", {"start": v(20.72, -3.93) * mm, "end": v(22.14, -4.2) * mm});
            skLineSegment(sketch, "E1833", {"start": v(22.14, -4.2) * mm, "end": v(22.71, -5.05) * mm});
            skLineSegment(sketch, "E1834", {"start": v(22.71, -5.05) * mm, "end": v(22.54, -5.76) * mm});
            skLineSegment(sketch, "E1835", {"start": v(22.54, -5.76) * mm, "end": v(22.35, -6.46) * mm});
            skLineSegment(sketch, "E1836", {"start": v(22.35, -6.46) * mm, "end": v(22.83, -7.38) * mm});
            skLineSegment(sketch, "E1837", {"start": v(22.83, -7.38) * mm, "end": v(23.52, -7.6) * mm});
            skLineSegment(sketch, "E1838", {"start": v(23.52, -7.6) * mm, "end": v(24.45, -7.06) * mm});
            skLineSegment(sketch, "E1839", {"start": v(24.45, -7.06) * mm, "end": v(24.66, -6.3) * mm});
            skLineSegment(sketch, "E1840", {"start": v(24.66, -6.3) * mm, "end": v(24.84, -5.52) * mm});
            skLineSegment(sketch, "E1841", {"start": v(24.84, -5.52) * mm, "end": v(24.29, -4.6) * mm});
            skLineSegment(sketch, "E1842", {"start": v(20.3, -7.99) * mm, "end": v(19.62, -7.72) * mm});
            skLineSegment(sketch, "E1843", {"start": v(21.53, -13.57) * mm, "end": v(21.94, -12.9) * mm});
            skLineSegment(sketch, "E1844", {"start": v(21.94, -12.9) * mm, "end": v(22.33, -12.2) * mm});
            skLineSegment(sketch, "E1845", {"start": v(22.33, -12.2) * mm, "end": v(22.7, -11.5) * mm});
            skLineSegment(sketch, "E1846", {"start": v(22.7, -11.5) * mm, "end": v(23.05, -10.78) * mm});
            skLineSegment(sketch, "E1847", {"start": v(23.05, -10.78) * mm, "end": v(21.73, -10.17) * mm});
            skLineSegment(sketch, "E1848", {"start": v(21.73, -10.17) * mm, "end": v(21.4, -10.84) * mm});
            skLineSegment(sketch, "E1849", {"start": v(21.4, -10.84) * mm, "end": v(21.06, -11.5) * mm});
            skLineSegment(sketch, "E1850", {"start": v(21.06, -11.5) * mm, "end": v(20.69, -12.15) * mm});
            skLineSegment(sketch, "E1851", {"start": v(20.69, -12.15) * mm, "end": v(19.68, -12.4) * mm});
            skLineSegment(sketch, "E1852", {"start": v(19.68, -12.4) * mm, "end": v(18.45, -11.63) * mm});
            skLineSegment(sketch, "E1853", {"start": v(18.45, -11.63) * mm, "end": v(18.18, -10.68) * mm});
            skLineSegment(sketch, "E1854", {"start": v(18.18, -10.68) * mm, "end": v(18.5, -10.1) * mm});
            skLineSegment(sketch, "E1855", {"start": v(18.5, -10.1) * mm, "end": v(18.81, -9.53) * mm});
            skLineSegment(sketch, "E1856", {"start": v(18.81, -9.53) * mm, "end": v(19.76, -9.24) * mm});
            skLineSegment(sketch, "E1857", {"start": v(16.52, -16.38) * mm, "end": v(16, -16.9) * mm});
            skLineSegment(sketch, "E1858", {"start": v(16, -16.9) * mm, "end": v(15.46, -17.38) * mm});
            skLineSegment(sketch, "E1859", {"start": v(15.46, -17.38) * mm, "end": v(14.91, -17.86) * mm});
            skLineSegment(sketch, "E1860", {"start": v(14.91, -17.86) * mm, "end": v(14.8, -18.89) * mm});
            skLineSegment(sketch, "E1861", {"start": v(14.8, -18.89) * mm, "end": v(15.25, -19.46) * mm});
            skLineSegment(sketch, "E1862", {"start": v(15.25, -19.46) * mm, "end": v(16.31, -19.53) * mm});
            skLineSegment(sketch, "E1863", {"start": v(16.31, -19.53) * mm, "end": v(16.92, -19.01) * mm});
            skLineSegment(sketch, "E1864", {"start": v(16.92, -19.01) * mm, "end": v(17.5, -18.48) * mm});
            skLineSegment(sketch, "E1865", {"start": v(17.5, -18.48) * mm, "end": v(18.07, -17.92) * mm});
            skLineSegment(sketch, "E1866", {"start": v(18.07, -17.92) * mm, "end": v(14.97, -14.85) * mm});
            skLineSegment(sketch, "E1867", {"start": v(11.02, -21.32) * mm, "end": v(11.68, -20.96) * mm});
            skLineSegment(sketch, "E1868", {"start": v(11.68, -20.96) * mm, "end": v(12.33, -20.59) * mm});
            skLineSegment(sketch, "E1869", {"start": v(12.33, -20.59) * mm, "end": v(12.96, -20.2) * mm});
            skLineSegment(sketch, "E1870", {"start": v(12.96, -20.2) * mm, "end": v(13.59, -19.77) * mm});
            skLineSegment(sketch, "E1871", {"start": v(10.35, -20.02) * mm, "end": v(10.97, -19.7) * mm});
            skLineSegment(sketch, "E1872", {"start": v(10.97, -19.7) * mm, "end": v(11.58, -19.34) * mm});
            skLineSegment(sketch, "E1873", {"start": v(11.58, -19.34) * mm, "end": v(12.18, -18.97) * mm});
            skLineSegment(sketch, "E1874", {"start": v(12.18, -18.97) * mm, "end": v(12.76, -18.58) * mm});
            skLineSegment(sketch, "E1875", {"start": v(9.96, -22.63) * mm, "end": v(9.52, -23.6) * mm});
            skLineSegment(sketch, "E1876", {"start": v(9.52, -23.6) * mm, "end": v(7.89, -19.56) * mm});
            skLineSegment(sketch, "E1877", {"start": v(7.27, -19.8) * mm, "end": v(7.89, -19.56) * mm});
            skLineSegment(sketch, "E1878", {"start": v(7.89, -19.56) * mm, "end": v(8.5, -19.3) * mm});
            skLineSegment(sketch, "E1879", {"start": v(3.45, -20.8) * mm, "end": v(4.1, -20.68) * mm});
            skLineSegment(sketch, "E1880", {"start": v(4.1, -20.68) * mm, "end": v(4.75, -20.55) * mm});
            skLineSegment(sketch, "E1881", {"start": v(4.75, -20.55) * mm, "end": v(5.39, -20.39) * mm});
            skLineSegment(sketch, "E1882", {"start": v(5.39, -20.39) * mm, "end": v(6.02, -20.2) * mm});
            skLineSegment(sketch, "E1883", {"start": v(6.02, -20.2) * mm, "end": v(6.43, -21.6) * mm});
            skLineSegment(sketch, "E1884", {"start": v(6.43, -21.6) * mm, "end": v(5.94, -22.5) * mm});
            skLineSegment(sketch, "E1885", {"start": v(5.94, -22.5) * mm, "end": v(5.24, -22.67) * mm});
            skLineSegment(sketch, "E1886", {"start": v(5.24, -22.67) * mm, "end": v(4.53, -22.82) * mm});
            skLineSegment(sketch, "E1887", {"start": v(4.53, -22.82) * mm, "end": v(3.93, -23.67) * mm});
            skLineSegment(sketch, "E1888", {"start": v(3.93, -23.67) * mm, "end": v(4.05, -24.39) * mm});
            skLineSegment(sketch, "E1889", {"start": v(4.05, -24.39) * mm, "end": v(4.95, -24.96) * mm});
            skLineSegment(sketch, "E1890", {"start": v(4.95, -24.96) * mm, "end": v(5.73, -24.8) * mm});
            skLineSegment(sketch, "E1891", {"start": v(5.73, -24.8) * mm, "end": v(6.5, -24.6) * mm});
            skLineSegment(sketch, "E1892", {"start": v(6.5, -24.6) * mm, "end": v(7.06, -23.7) * mm});
            skLineSegment(sketch, "E1893", {"start": v(-1.26, -23.23) * mm, "end": v(-1.99, -23.18) * mm});
            skLineSegment(sketch, "E1894", {"start": v(-1.99, -23.18) * mm, "end": v(-2.7, -23.1) * mm});
            skLineSegment(sketch, "E1895", {"start": v(-2.7, -23.1) * mm, "end": v(-3.43, -23.01) * mm});
            skLineSegment(sketch, "E1896", {"start": v(-3.43, -23.01) * mm, "end": v(-4.28, -23.6) * mm});
            skLineSegment(sketch, "E1897", {"start": v(-4.28, -23.6) * mm, "end": v(-4.4, -24.33) * mm});
            skLineSegment(sketch, "E1898", {"start": v(-4.4, -24.33) * mm, "end": v(-3.75, -25.17) * mm});
            skLineSegment(sketch, "E1899", {"start": v(-3.75, -25.17) * mm, "end": v(-2.96, -25.28) * mm});
            skLineSegment(sketch, "E1900", {"start": v(-2.96, -25.28) * mm, "end": v(-2.17, -25.35) * mm});
            skLineSegment(sketch, "E1901", {"start": v(-2.17, -25.35) * mm, "end": v(-1.38, -25.41) * mm});
            skLineSegment(sketch, "E1902", {"start": v(-1.38, -25.41) * mm, "end": v(-1.14, -21.06) * mm});
            skLineSegment(sketch, "E1903", {"start": v(-5.05, -20.47) * mm, "end": v(-5.4, -21.88) * mm});
            skLineSegment(sketch, "E1904", {"start": v(-5.4, -21.88) * mm, "end": v(-6.47, -23.1) * mm});
            skLineSegment(sketch, "E1905", {"start": v(-6.47, -23.1) * mm, "end": v(-7.62, -24.28) * mm});
            skLineSegment(sketch, "E1906", {"start": v(-7.62, -24.28) * mm, "end": v(-7.9, -22.66) * mm});
            skLineSegment(sketch, "E1907", {"start": v(-7.9, -22.66) * mm, "end": v(-8.08, -21.04) * mm});
            skLineSegment(sketch, "E1908", {"start": v(-8.08, -21.04) * mm, "end": v(-7.56, -19.68) * mm});
            skLineSegment(sketch, "E1909", {"start": v(-5.4, -21.88) * mm, "end": v(-6.07, -21.7) * mm});
            skLineSegment(sketch, "E1910", {"start": v(-6.07, -21.7) * mm, "end": v(-6.75, -21.5) * mm});
            skLineSegment(sketch, "E1911", {"start": v(-6.75, -21.5) * mm, "end": v(-7.42, -21.28) * mm});
            skLineSegment(sketch, "E1912", {"start": v(-7.42, -21.28) * mm, "end": v(-8.08, -21.04) * mm});
            skLineSegment(sketch, "E1913", {"start": v(-12.63, -20.4) * mm, "end": v(-11.98, -20.79) * mm});
            skLineSegment(sketch, "E1914", {"start": v(-11.98, -20.79) * mm, "end": v(-11.33, -21.15) * mm});
            skLineSegment(sketch, "E1915", {"start": v(-11.33, -21.15) * mm, "end": v(-10.66, -21.5) * mm});
            skLineSegment(sketch, "E1916", {"start": v(-10.66, -21.5) * mm, "end": v(-9.99, -21.82) * mm});
            skLineSegment(sketch, "E1917", {"start": v(-11.86, -19.17) * mm, "end": v(-11.26, -19.53) * mm});
            skLineSegment(sketch, "E1918", {"start": v(-11.26, -19.53) * mm, "end": v(-10.64, -19.87) * mm});
            skLineSegment(sketch, "E1919", {"start": v(-10.64, -19.87) * mm, "end": v(-10.01, -20.2) * mm});
            skLineSegment(sketch, "E1920", {"start": v(-10.01, -20.2) * mm, "end": v(-9.38, -20.5) * mm});
            skLineSegment(sketch, "E1921", {"start": v(-14.3, -20.17) * mm, "end": v(-15.36, -20.3) * mm});
            skLineSegment(sketch, "E1922", {"start": v(-15.36, -20.3) * mm, "end": v(-15.99, -19.8) * mm});
            skLineSegment(sketch, "E1923", {"start": v(-15.99, -19.8) * mm, "end": v(-16.6, -19.3) * mm});
            skLineSegment(sketch, "E1924", {"start": v(-16.6, -19.3) * mm, "end": v(-16.7, -18.23) * mm});
            skLineSegment(sketch, "E1925", {"start": v(-16.7, -18.23) * mm, "end": v(-16.2, -17.69) * mm});
            skLineSegment(sketch, "E1926", {"start": v(-16.2, -17.69) * mm, "end": v(-15.17, -17.64) * mm});
            skLineSegment(sketch, "E1927", {"start": v(-15.17, -17.64) * mm, "end": v(-15.23, -16.62) * mm});
            skLineSegment(sketch, "E1928", {"start": v(-15.23, -16.62) * mm, "end": v(-14.73, -16.08) * mm});
            skLineSegment(sketch, "E1929", {"start": v(-14.73, -16.08) * mm, "end": v(-13.75, -15.98) * mm});
            skLineSegment(sketch, "E1930", {"start": v(-13.75, -15.98) * mm, "end": v(-13.25, -16.4) * mm});
            skLineSegment(sketch, "E1931", {"start": v(-13.25, -16.4) * mm, "end": v(-12.73, -16.81) * mm});
            skLineSegment(sketch, "E1932", {"start": v(-12.73, -16.81) * mm, "end": v(-12.62, -17.8) * mm});
            skLineSegment(sketch, "E1933", {"start": v(-14.62, -18.1) * mm, "end": v(-15.17, -17.64) * mm});
            skLineSegment(sketch, "E1934", {"start": v(-20.39, -15.23) * mm, "end": v(-19.9, -15.86) * mm});
            skLineSegment(sketch, "E1935", {"start": v(-19.9, -15.86) * mm, "end": v(-19.4, -16.47) * mm});
            skLineSegment(sketch, "E1936", {"start": v(-19.4, -16.47) * mm, "end": v(-18.87, -17.07) * mm});
            skLineSegment(sketch, "E1937", {"start": v(-18.87, -17.07) * mm, "end": v(-18.33, -17.65) * mm});
            skLineSegment(sketch, "E1938", {"start": v(-18.33, -17.65) * mm, "end": v(-17.28, -16.65) * mm});
            skLineSegment(sketch, "E1939", {"start": v(-17.28, -16.65) * mm, "end": v(-17.8, -16.1) * mm});
            skLineSegment(sketch, "E1940", {"start": v(-17.8, -16.1) * mm, "end": v(-18.29, -15.53) * mm});
            skLineSegment(sketch, "E1941", {"start": v(-18.29, -15.53) * mm, "end": v(-18.76, -14.95) * mm});
            skLineSegment(sketch, "E1942", {"start": v(-18.76, -14.95) * mm, "end": v(-18.64, -13.93) * mm});
            skLineSegment(sketch, "E1943", {"start": v(-18.64, -13.93) * mm, "end": v(-17.48, -13.05) * mm});
            skLineSegment(sketch, "E1944", {"start": v(-17.48, -13.05) * mm, "end": v(-16.49, -13.14) * mm});
            skLineSegment(sketch, "E1945", {"start": v(-16.49, -13.14) * mm, "end": v(-16.07, -13.65) * mm});
            skLineSegment(sketch, "E1946", {"start": v(-16.07, -13.65) * mm, "end": v(-15.64, -14.14) * mm});
            skLineSegment(sketch, "E1947", {"start": v(-15.64, -14.14) * mm, "end": v(-15.71, -15.13) * mm});
            skCircle(sketch, "E1948", {"center": v(0, 0) * mm, "radius": 10.83 * mm});
            skLineSegment(sketch, "E1949", {"start": v(-33.84, 9.46) * mm, "end": v(-30.7, 16.67) * mm});
            skSolve(sketch);
        }
        {
            var Q0;
            Q0=makeQuery(id+"F0.imprint","IMPRINT",FACE,{"disambiguationData":[TD([[makeQuery(id+"F0.imprint","IMPRINT",EDGE,{"derivedFrom":sQuery(id+"F0.wireOp",EDGE,"E0")}),1.0]])]});
            extrude(context, id + "F1", {"entities" : qUnion([Q0]), "depth" : 12.7 * mm});
        }
        {
            var Q0;
            Q0=makeQuery(id+"F1.opExtrude","SWEPT_EDGE",EDGE,{"disambiguationData":[OSD([sQuery(id+"F0.wireOp",EDGE,"E325"),sQuery(id+"F0.wireOp",EDGE,"E326")])]});
            fillet(context, id + "F2", {"entities" : qUnion([Q0]), "radius" : 316.58 * mm, "tangentPropagation" : true, "allowEdgeOverflow" : false});
        }
    });
